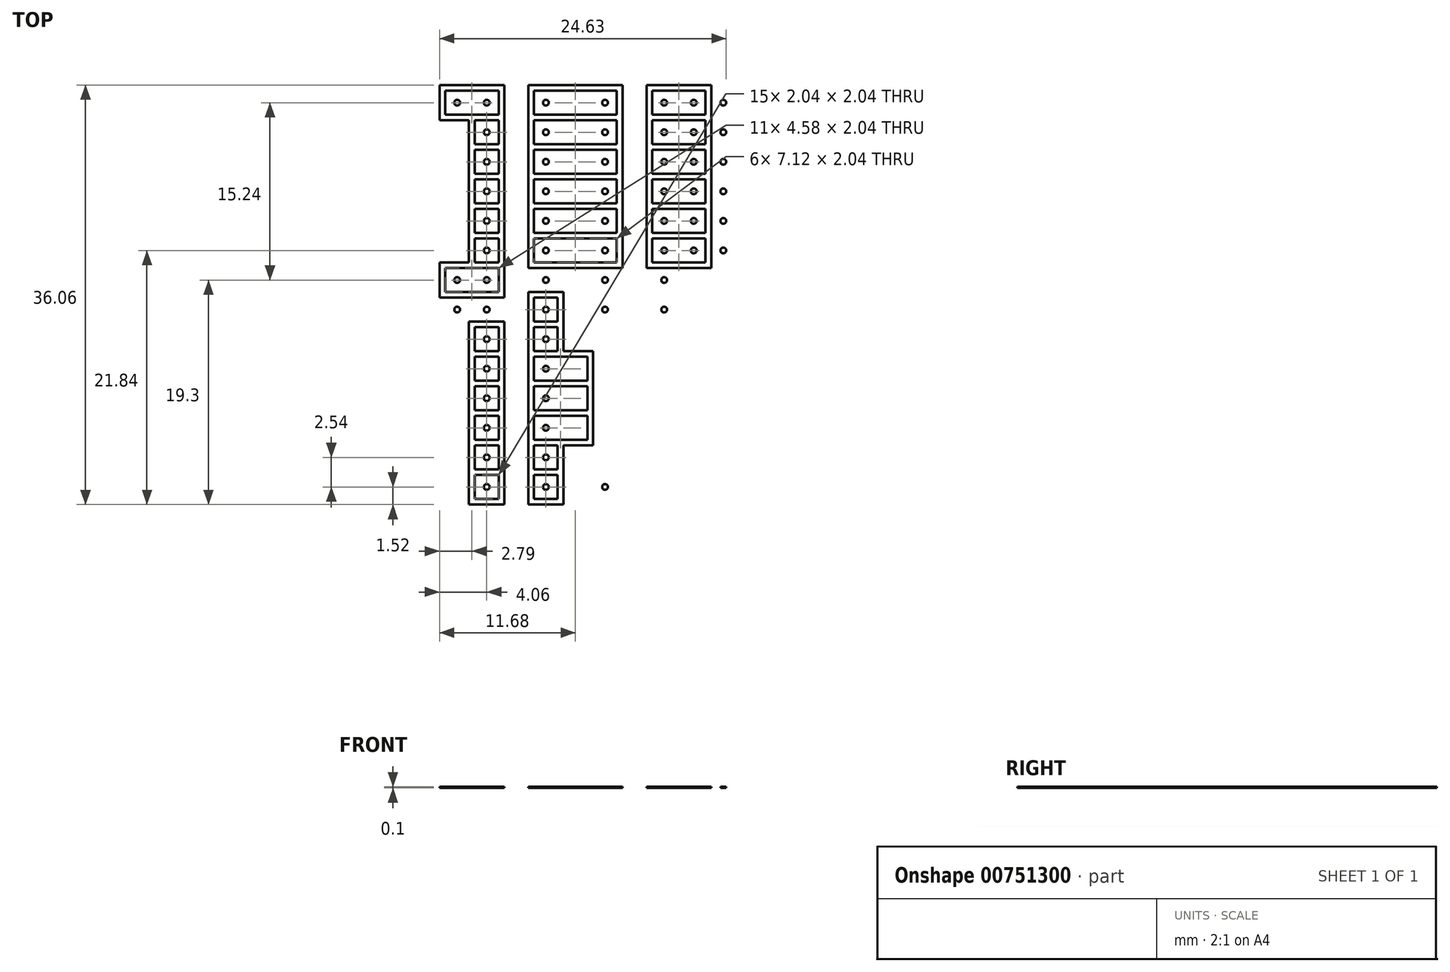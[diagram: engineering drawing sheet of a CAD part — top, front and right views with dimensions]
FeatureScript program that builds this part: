
annotation { "Feature Type Name" : "Feature", "Feature Type Description" : "" }
export const myFeature = defineFeature(function(context is Context, id is Id, definition is map)
    precondition{}
    {
        {
            var Q0;
            Q0=qCreatedBy(makeId("Top.planeOp"),FACE);
            var sketch = newSketch(context, id + "F0", { "sketchPlane" : qUnion([Q0])});
            skLineSegment(sketch, "E0.bottom", {"start": v(0, 0) * mm, "end": v(70, 0) * mm});
            skLineSegment(sketch, "E0.top", {"start": v(0, 100) * mm, "end": v(70, 100) * mm});
            skLineSegment(sketch, "E0.left", {"start": v(0, 0) * mm, "end": v(0, 100) * mm});
            skLineSegment(sketch, "E0.right", {"start": v(70, 0) * mm, "end": v(70, 100) * mm});
            skLineSegment(sketch, "E1", {"start": v(0.46, 100) * mm, "end": v(0.46, 0) * mm});
            skLineSegment(sketch, "E2", {"start": v(0.96, 100) * mm, "end": v(0.96, 0) * mm});
            skLineSegment(sketch, "E3.1.0.0", {"start": v(3, 100) * mm, "end": v(3, 0) * mm});
            skLineSegment(sketch, "E3.1.0.1", {"start": v(3.5, 100) * mm, "end": v(3.5, 0) * mm});
            skLineSegment(sketch, "E3.2.0.0", {"start": v(5.54, 100) * mm, "end": v(5.54, 0) * mm});
            skLineSegment(sketch, "E3.2.0.1", {"start": v(6.04, 100) * mm, "end": v(6.04, 0) * mm});
            skLineSegment(sketch, "E3.3.0.0", {"start": v(8.08, 100) * mm, "end": v(8.08, 0) * mm});
            skLineSegment(sketch, "E3.3.0.1", {"start": v(8.58, 100) * mm, "end": v(8.58, 0) * mm});
            skLineSegment(sketch, "E3.4.0.0", {"start": v(10.62, 100) * mm, "end": v(10.62, 0) * mm});
            skLineSegment(sketch, "E3.4.0.1", {"start": v(11.12, 100) * mm, "end": v(11.12, 0) * mm});
            skLineSegment(sketch, "E3.5.0.0", {"start": v(13.16, 100) * mm, "end": v(13.16, 0) * mm});
            skLineSegment(sketch, "E3.5.0.1", {"start": v(13.66, 100) * mm, "end": v(13.66, 0) * mm});
            skLineSegment(sketch, "E3.6.0.0", {"start": v(15.7, 100) * mm, "end": v(15.7, 0) * mm});
            skLineSegment(sketch, "E3.6.0.1", {"start": v(16.2, 100) * mm, "end": v(16.2, 0) * mm});
            skLineSegment(sketch, "E3.7.0.0", {"start": v(18.24, 100) * mm, "end": v(18.24, 0) * mm});
            skLineSegment(sketch, "E3.7.0.1", {"start": v(18.74, 100) * mm, "end": v(18.74, 0) * mm});
            skLineSegment(sketch, "E3.8.0.0", {"start": v(20.78, 100) * mm, "end": v(20.78, 0) * mm});
            skLineSegment(sketch, "E3.8.0.1", {"start": v(21.28, 100) * mm, "end": v(21.28, 0) * mm});
            skLineSegment(sketch, "E3.9.0.0", {"start": v(23.32, 100) * mm, "end": v(23.32, 0) * mm});
            skLineSegment(sketch, "E3.9.0.1", {"start": v(23.82, 100) * mm, "end": v(23.82, 0) * mm});
            skLineSegment(sketch, "E3.10.0.0", {"start": v(25.86, 100) * mm, "end": v(25.86, 0) * mm});
            skLineSegment(sketch, "E3.10.0.1", {"start": v(26.36, 100) * mm, "end": v(26.36, 0) * mm});
            skLineSegment(sketch, "E3.11.0.0", {"start": v(28.4, 100) * mm, "end": v(28.4, 0) * mm});
            skLineSegment(sketch, "E3.11.0.1", {"start": v(28.9, 100) * mm, "end": v(28.9, 0) * mm});
            skLineSegment(sketch, "E3.12.0.0", {"start": v(30.94, 100) * mm, "end": v(30.94, 0) * mm});
            skLineSegment(sketch, "E3.12.0.1", {"start": v(31.44, 100) * mm, "end": v(31.44, 0) * mm});
            skLineSegment(sketch, "E3.13.0.0", {"start": v(33.48, 100) * mm, "end": v(33.48, 0) * mm});
            skLineSegment(sketch, "E3.13.0.1", {"start": v(33.98, 100) * mm, "end": v(33.98, 0) * mm});
            skLineSegment(sketch, "E3.14.0.0", {"start": v(36.02, 100) * mm, "end": v(36.02, 0) * mm});
            skLineSegment(sketch, "E3.14.0.1", {"start": v(36.52, 100) * mm, "end": v(36.52, 0) * mm});
            skLineSegment(sketch, "E3.15.0.0", {"start": v(38.56, 100) * mm, "end": v(38.56, 0) * mm});
            skLineSegment(sketch, "E3.15.0.1", {"start": v(39.06, 100) * mm, "end": v(39.06, 0) * mm});
            skLineSegment(sketch, "E3.16.0.0", {"start": v(41.1, 100) * mm, "end": v(41.1, 0) * mm});
            skLineSegment(sketch, "E3.16.0.1", {"start": v(41.6, 100) * mm, "end": v(41.6, 0) * mm});
            skLineSegment(sketch, "E3.17.0.0", {"start": v(43.64, 100) * mm, "end": v(43.64, 0) * mm});
            skLineSegment(sketch, "E3.17.0.1", {"start": v(44.14, 100) * mm, "end": v(44.14, 0) * mm});
            skLineSegment(sketch, "E3.18.0.0", {"start": v(46.18, 100) * mm, "end": v(46.18, 0) * mm});
            skLineSegment(sketch, "E3.18.0.1", {"start": v(46.68, 100) * mm, "end": v(46.68, 0) * mm});
            skLineSegment(sketch, "E3.19.0.0", {"start": v(48.72, 100) * mm, "end": v(48.72, 0) * mm});
            skLineSegment(sketch, "E3.19.0.1", {"start": v(49.22, 100) * mm, "end": v(49.22, 0) * mm});
            skLineSegment(sketch, "E3.20.0.0", {"start": v(51.26, 100) * mm, "end": v(51.26, 0) * mm});
            skLineSegment(sketch, "E3.20.0.1", {"start": v(51.76, 100) * mm, "end": v(51.76, 0) * mm});
            skLineSegment(sketch, "E3.21.0.0", {"start": v(53.8, 100) * mm, "end": v(53.8, 0) * mm});
            skLineSegment(sketch, "E3.21.0.1", {"start": v(54.3, 100) * mm, "end": v(54.3, 0) * mm});
            skLineSegment(sketch, "E3.22.0.0", {"start": v(56.34, 100) * mm, "end": v(56.34, 0) * mm});
            skLineSegment(sketch, "E3.22.0.1", {"start": v(56.84, 100) * mm, "end": v(56.84, 0) * mm});
            skLineSegment(sketch, "E3.23.0.0", {"start": v(58.88, 100) * mm, "end": v(58.88, 0) * mm});
            skLineSegment(sketch, "E3.23.0.1", {"start": v(59.38, 100) * mm, "end": v(59.38, 0) * mm});
            skLineSegment(sketch, "E3.24.0.0", {"start": v(61.42, 100) * mm, "end": v(61.42, 0) * mm});
            skLineSegment(sketch, "E3.24.0.1", {"start": v(61.92, 100) * mm, "end": v(61.92, 0) * mm});
            skLineSegment(sketch, "E3.25.0.0", {"start": v(63.96, 100) * mm, "end": v(63.96, 0) * mm});
            skLineSegment(sketch, "E3.25.0.1", {"start": v(64.46, 100) * mm, "end": v(64.46, 0) * mm});
            skLineSegment(sketch, "E3.26.0.0", {"start": v(66.5, 100) * mm, "end": v(66.5, 0) * mm});
            skLineSegment(sketch, "E3.26.0.1", {"start": v(67, 100) * mm, "end": v(67, 0) * mm});
            skLineSegment(sketch, "E3.27.0.0", {"start": v(69.04, 100) * mm, "end": v(69.04, 0) * mm});
            skLineSegment(sketch, "E3.27.0.1", {"start": v(69.54, 100) * mm, "end": v(69.54, 0) * mm});
            skLineSegment(sketch, "E3.direction1", {"start": v(0.46, 0) * mm, "end": v(3, 0) * mm, "construction": true});
            skLineSegment(sketch, "E4", {"start": v(0, 50) * mm, "end": v(0.46, 50) * mm, "construction": true});
            skLineSegment(sketch, "E5", {"start": v(69.54, 50) * mm, "end": v(70, 50) * mm, "construction": true});
            skLineSegment(sketch, "E6", {"start": v(0, 99.28) * mm, "end": v(70, 99.28) * mm});
            skLineSegment(sketch, "E7", {"start": v(70, 99.28) * mm, "end": v(70, 99.78) * mm});
            skLineSegment(sketch, "E8", {"start": v(70, 99.78) * mm, "end": v(0, 99.78) * mm});
            skLineSegment(sketch, "E9.1.0.0", {"start": v(70, 97.24) * mm, "end": v(0, 97.24) * mm});
            skLineSegment(sketch, "E9.1.0.1", {"start": v(0, 96.74) * mm, "end": v(70, 96.74) * mm});
            skLineSegment(sketch, "E9.2.0.0", {"start": v(70, 94.7) * mm, "end": v(0, 94.7) * mm});
            skLineSegment(sketch, "E9.2.0.1", {"start": v(0, 94.2) * mm, "end": v(70, 94.2) * mm});
            skLineSegment(sketch, "E9.direction1", {"start": v(0, 99.28) * mm, "end": v(0, 96.74) * mm, "construction": true});
            skLineSegment(sketch, "E10.0.3.0", {"start": v(70, 92.16) * mm, "end": v(0, 92.16) * mm});
            skLineSegment(sketch, "E10.3.3.0", {"start": v(0, 91.66) * mm, "end": v(70, 91.66) * mm});
            skLineSegment(sketch, "E10.0.4.0", {"start": v(70, 89.62) * mm, "end": v(0, 89.62) * mm});
            skLineSegment(sketch, "E10.3.4.0", {"start": v(0, 89.12) * mm, "end": v(70, 89.12) * mm});
            skLineSegment(sketch, "E10.0.5.0", {"start": v(70, 87.08) * mm, "end": v(0, 87.08) * mm});
            skLineSegment(sketch, "E10.3.5.0", {"start": v(0, 86.58) * mm, "end": v(70, 86.58) * mm});
            skLineSegment(sketch, "E10.0.6.0", {"start": v(70, 84.54) * mm, "end": v(0, 84.54) * mm});
            skLineSegment(sketch, "E10.3.6.0", {"start": v(0, 84.04) * mm, "end": v(70, 84.04) * mm});
            skLineSegment(sketch, "E10.0.7.0", {"start": v(70, 82) * mm, "end": v(0, 82) * mm});
            skLineSegment(sketch, "E10.3.7.0", {"start": v(0, 81.5) * mm, "end": v(70, 81.5) * mm});
            skLineSegment(sketch, "E10.0.8.0", {"start": v(70, 79.46) * mm, "end": v(0, 79.46) * mm});
            skLineSegment(sketch, "E10.3.8.0", {"start": v(0, 78.96) * mm, "end": v(70, 78.96) * mm});
            skLineSegment(sketch, "E10.0.9.0", {"start": v(70, 76.92) * mm, "end": v(0, 76.92) * mm});
            skLineSegment(sketch, "E10.3.9.0", {"start": v(0, 76.42) * mm, "end": v(70, 76.42) * mm});
            skLineSegment(sketch, "E10.0.10.0", {"start": v(70, 74.38) * mm, "end": v(0, 74.38) * mm});
            skLineSegment(sketch, "E10.3.10.0", {"start": v(0, 73.88) * mm, "end": v(70, 73.88) * mm});
            skLineSegment(sketch, "E10.0.11.0", {"start": v(70, 71.84) * mm, "end": v(0, 71.84) * mm});
            skLineSegment(sketch, "E10.3.11.0", {"start": v(0, 71.34) * mm, "end": v(70, 71.34) * mm});
            skLineSegment(sketch, "E10.0.12.0", {"start": v(70, 69.3) * mm, "end": v(0, 69.3) * mm});
            skLineSegment(sketch, "E10.3.12.0", {"start": v(0, 68.8) * mm, "end": v(70, 68.8) * mm});
            skLineSegment(sketch, "E10.0.13.0", {"start": v(70, 66.76) * mm, "end": v(0, 66.76) * mm});
            skLineSegment(sketch, "E10.3.13.0", {"start": v(0, 66.26) * mm, "end": v(70, 66.26) * mm});
            skLineSegment(sketch, "E10.0.14.0", {"start": v(70, 64.22) * mm, "end": v(0, 64.22) * mm});
            skLineSegment(sketch, "E10.3.14.0", {"start": v(0, 63.72) * mm, "end": v(70, 63.72) * mm});
            skLineSegment(sketch, "E10.0.15.0", {"start": v(70, 61.68) * mm, "end": v(0, 61.68) * mm});
            skLineSegment(sketch, "E10.3.15.0", {"start": v(0, 61.18) * mm, "end": v(70, 61.18) * mm});
            skLineSegment(sketch, "E10.0.16.0", {"start": v(70, 59.14) * mm, "end": v(0, 59.14) * mm});
            skLineSegment(sketch, "E10.3.16.0", {"start": v(0, 58.64) * mm, "end": v(70, 58.64) * mm});
            skLineSegment(sketch, "E10.0.17.0", {"start": v(70, 56.6) * mm, "end": v(0, 56.6) * mm});
            skLineSegment(sketch, "E10.3.17.0", {"start": v(0, 56.1) * mm, "end": v(70, 56.1) * mm});
            skLineSegment(sketch, "E10.0.18.0", {"start": v(70, 54.06) * mm, "end": v(0, 54.06) * mm});
            skLineSegment(sketch, "E10.3.18.0", {"start": v(0, 53.56) * mm, "end": v(70, 53.56) * mm});
            skLineSegment(sketch, "E10.0.19.0", {"start": v(70, 51.52) * mm, "end": v(0, 51.52) * mm});
            skLineSegment(sketch, "E10.3.19.0", {"start": v(0, 51.02) * mm, "end": v(70, 51.02) * mm});
            skLineSegment(sketch, "E10.0.20.0", {"start": v(70, 48.98) * mm, "end": v(0, 48.98) * mm});
            skLineSegment(sketch, "E10.3.20.0", {"start": v(0, 48.48) * mm, "end": v(70, 48.48) * mm});
            skLineSegment(sketch, "E10.0.21.0", {"start": v(70, 46.44) * mm, "end": v(0, 46.44) * mm});
            skLineSegment(sketch, "E10.3.21.0", {"start": v(0, 45.94) * mm, "end": v(70, 45.94) * mm});
            skLineSegment(sketch, "E10.0.22.0", {"start": v(70, 43.9) * mm, "end": v(0, 43.9) * mm});
            skLineSegment(sketch, "E10.3.22.0", {"start": v(0, 43.4) * mm, "end": v(70, 43.4) * mm});
            skLineSegment(sketch, "E10.0.23.0", {"start": v(70, 41.36) * mm, "end": v(0, 41.36) * mm});
            skLineSegment(sketch, "E10.3.23.0", {"start": v(0, 40.86) * mm, "end": v(70, 40.86) * mm});
            skLineSegment(sketch, "E10.0.24.0", {"start": v(70, 38.82) * mm, "end": v(0, 38.82) * mm});
            skLineSegment(sketch, "E10.3.24.0", {"start": v(0, 38.32) * mm, "end": v(70, 38.32) * mm});
            skLineSegment(sketch, "E10.0.25.0", {"start": v(70, 36.28) * mm, "end": v(0, 36.28) * mm});
            skLineSegment(sketch, "E10.3.25.0", {"start": v(0, 35.78) * mm, "end": v(70, 35.78) * mm});
            skLineSegment(sketch, "E10.0.26.0", {"start": v(70, 33.74) * mm, "end": v(0, 33.74) * mm});
            skLineSegment(sketch, "E10.3.26.0", {"start": v(0, 33.24) * mm, "end": v(70, 33.24) * mm});
            skLineSegment(sketch, "E10.0.27.0", {"start": v(70, 31.2) * mm, "end": v(0, 31.2) * mm});
            skLineSegment(sketch, "E10.3.27.0", {"start": v(0, 30.7) * mm, "end": v(70, 30.7) * mm});
            skLineSegment(sketch, "E10.0.28.0", {"start": v(70, 28.66) * mm, "end": v(0, 28.66) * mm});
            skLineSegment(sketch, "E10.3.28.0", {"start": v(0, 28.16) * mm, "end": v(70, 28.16) * mm});
            skLineSegment(sketch, "E10.0.29.0", {"start": v(70, 26.12) * mm, "end": v(0, 26.12) * mm});
            skLineSegment(sketch, "E10.3.29.0", {"start": v(0, 25.62) * mm, "end": v(70, 25.62) * mm});
            skLineSegment(sketch, "E10.0.30.0", {"start": v(70, 23.58) * mm, "end": v(0, 23.58) * mm});
            skLineSegment(sketch, "E10.3.30.0", {"start": v(0, 23.08) * mm, "end": v(70, 23.08) * mm});
            skLineSegment(sketch, "E10.0.31.0", {"start": v(70, 21.04) * mm, "end": v(0, 21.04) * mm});
            skLineSegment(sketch, "E10.3.31.0", {"start": v(0, 20.54) * mm, "end": v(70, 20.54) * mm});
            skLineSegment(sketch, "E10.0.32.0", {"start": v(70, 18.5) * mm, "end": v(0, 18.5) * mm});
            skLineSegment(sketch, "E10.3.32.0", {"start": v(0, 18) * mm, "end": v(70, 18) * mm});
            skLineSegment(sketch, "E10.0.33.0", {"start": v(70, 15.96) * mm, "end": v(0, 15.96) * mm});
            skLineSegment(sketch, "E10.3.33.0", {"start": v(0, 15.46) * mm, "end": v(70, 15.46) * mm});
            skLineSegment(sketch, "E10.0.34.0", {"start": v(70, 13.42) * mm, "end": v(0, 13.42) * mm});
            skLineSegment(sketch, "E10.3.34.0", {"start": v(0, 12.92) * mm, "end": v(70, 12.92) * mm});
            skLineSegment(sketch, "E10.0.35.0", {"start": v(70, 10.88) * mm, "end": v(0, 10.88) * mm});
            skLineSegment(sketch, "E10.3.35.0", {"start": v(0, 10.38) * mm, "end": v(70, 10.38) * mm});
            skLineSegment(sketch, "E10.0.36.0", {"start": v(70, 8.34) * mm, "end": v(0, 8.34) * mm});
            skLineSegment(sketch, "E10.3.36.0", {"start": v(0, 7.84) * mm, "end": v(70, 7.84) * mm});
            skLineSegment(sketch, "E10.0.37.0", {"start": v(70, 5.8) * mm, "end": v(0, 5.8) * mm});
            skLineSegment(sketch, "E10.3.37.0", {"start": v(0, 5.3) * mm, "end": v(70, 5.3) * mm});
            skLineSegment(sketch, "E10.0.38.0", {"start": v(70, 3.26) * mm, "end": v(0, 3.26) * mm});
            skLineSegment(sketch, "E10.3.38.0", {"start": v(0, 2.76) * mm, "end": v(70, 2.76) * mm});
            skLineSegment(sketch, "E10.0.39.0", {"start": v(70, 0.72) * mm, "end": v(0, 0.72) * mm});
            skLineSegment(sketch, "E10.3.39.0", {"start": v(0, 0.22) * mm, "end": v(70, 0.22) * mm});
            skLineSegment(sketch, "E11", {"start": v(35, 100) * mm, "end": v(35, 99.78) * mm, "construction": true});
            skLineSegment(sketch, "E12", {"start": v(35, 0) * mm, "end": v(35, 0.22) * mm, "construction": true});
            skCircle(sketch, "E13", {"center": v(1.98, 1.74) * mm, "radius": 0.25 * mm});
            skLineSegment(sketch, "E14", {"start": v(1.98, 2.76) * mm, "end": v(1.98, 0.72) * mm, "construction": true});
            skLineSegment(sketch, "E15", {"start": v(3, 1.74) * mm, "end": v(0.96, 1.74) * mm, "construction": true});
            skCircle(sketch, "E16.1.0.0", {"center": v(4.52, 1.74) * mm, "radius": 0.25 * mm});
            skCircle(sketch, "E16.2.0.0", {"center": v(7.06, 1.74) * mm, "radius": 0.25 * mm});
            skCircle(sketch, "E16.3.0.0", {"center": v(9.6, 1.74) * mm, "radius": 0.25 * mm});
            skCircle(sketch, "E16.4.0.0", {"center": v(12.14, 1.74) * mm, "radius": 0.25 * mm});
            skCircle(sketch, "E16.5.0.0", {"center": v(14.68, 1.74) * mm, "radius": 0.25 * mm});
            skCircle(sketch, "E16.6.0.0", {"center": v(17.22, 1.74) * mm, "radius": 0.25 * mm});
            skCircle(sketch, "E16.7.0.0", {"center": v(19.76, 1.74) * mm, "radius": 0.25 * mm});
            skCircle(sketch, "E16.8.0.0", {"center": v(22.3, 1.74) * mm, "radius": 0.25 * mm});
            skCircle(sketch, "E16.9.0.0", {"center": v(24.84, 1.74) * mm, "radius": 0.25 * mm});
            skCircle(sketch, "E16.10.0.0", {"center": v(27.38, 1.74) * mm, "radius": 0.25 * mm});
            skCircle(sketch, "E16.11.0.0", {"center": v(29.92, 1.74) * mm, "radius": 0.25 * mm});
            skCircle(sketch, "E16.12.0.0", {"center": v(32.46, 1.74) * mm, "radius": 0.25 * mm});
            skCircle(sketch, "E16.13.0.0", {"center": v(35, 1.74) * mm, "radius": 0.25 * mm});
            skCircle(sketch, "E16.14.0.0", {"center": v(37.54, 1.74) * mm, "radius": 0.25 * mm});
            skCircle(sketch, "E16.15.0.0", {"center": v(40.08, 1.74) * mm, "radius": 0.25 * mm});
            skCircle(sketch, "E16.16.0.0", {"center": v(42.62, 1.74) * mm, "radius": 0.25 * mm});
            skCircle(sketch, "E16.17.0.0", {"center": v(45.16, 1.74) * mm, "radius": 0.25 * mm});
            skCircle(sketch, "E16.18.0.0", {"center": v(47.7, 1.74) * mm, "radius": 0.25 * mm});
            skCircle(sketch, "E16.19.0.0", {"center": v(50.24, 1.74) * mm, "radius": 0.25 * mm});
            skCircle(sketch, "E16.20.0.0", {"center": v(52.78, 1.74) * mm, "radius": 0.25 * mm});
            skCircle(sketch, "E16.21.0.0", {"center": v(55.32, 1.74) * mm, "radius": 0.25 * mm});
            skCircle(sketch, "E16.22.0.0", {"center": v(57.86, 1.74) * mm, "radius": 0.25 * mm});
            skCircle(sketch, "E16.23.0.0", {"center": v(60.4, 1.74) * mm, "radius": 0.25 * mm});
            skCircle(sketch, "E16.24.0.0", {"center": v(62.94, 1.74) * mm, "radius": 0.25 * mm});
            skCircle(sketch, "E16.25.0.0", {"center": v(65.48, 1.74) * mm, "radius": 0.25 * mm});
            skCircle(sketch, "E16.26.0.0", {"center": v(68.02, 1.74) * mm, "radius": 0.25 * mm});
            skLineSegment(sketch, "E16.direction1", {"start": v(1.98, 1.74) * mm, "end": v(4.52, 1.74) * mm, "construction": true});
            skCircle(sketch, "E17.1.0.0", {"center": v(1.98, 4.28) * mm, "radius": 0.25 * mm});
            skCircle(sketch, "E17.1.0.1", {"center": v(4.52, 4.28) * mm, "radius": 0.25 * mm});
            skCircle(sketch, "E17.1.0.2", {"center": v(7.06, 4.28) * mm, "radius": 0.25 * mm});
            skCircle(sketch, "E17.1.0.3", {"center": v(9.6, 4.28) * mm, "radius": 0.25 * mm});
            skCircle(sketch, "E17.1.0.4", {"center": v(12.14, 4.28) * mm, "radius": 0.25 * mm});
            skCircle(sketch, "E17.1.0.5", {"center": v(14.68, 4.28) * mm, "radius": 0.25 * mm});
            skCircle(sketch, "E17.1.0.6", {"center": v(17.22, 4.28) * mm, "radius": 0.25 * mm});
            skCircle(sketch, "E17.1.0.7", {"center": v(19.76, 4.28) * mm, "radius": 0.25 * mm});
            skCircle(sketch, "E17.1.0.8", {"center": v(22.3, 4.28) * mm, "radius": 0.25 * mm});
            skCircle(sketch, "E17.1.0.9", {"center": v(24.84, 4.28) * mm, "radius": 0.25 * mm});
            skCircle(sketch, "E17.1.0.10", {"center": v(27.38, 4.28) * mm, "radius": 0.25 * mm});
            skCircle(sketch, "E17.1.0.11", {"center": v(29.92, 4.28) * mm, "radius": 0.25 * mm});
            skCircle(sketch, "E17.1.0.12", {"center": v(32.46, 4.28) * mm, "radius": 0.25 * mm});
            skCircle(sketch, "E17.1.0.13", {"center": v(35, 4.28) * mm, "radius": 0.25 * mm});
            skCircle(sketch, "E17.1.0.14", {"center": v(37.54, 4.28) * mm, "radius": 0.25 * mm});
            skCircle(sketch, "E17.1.0.15", {"center": v(40.08, 4.28) * mm, "radius": 0.25 * mm});
            skCircle(sketch, "E17.1.0.16", {"center": v(42.62, 4.28) * mm, "radius": 0.25 * mm});
            skCircle(sketch, "E17.1.0.17", {"center": v(45.16, 4.28) * mm, "radius": 0.25 * mm});
            skCircle(sketch, "E17.1.0.18", {"center": v(47.7, 4.28) * mm, "radius": 0.25 * mm});
            skCircle(sketch, "E17.1.0.19", {"center": v(50.24, 4.28) * mm, "radius": 0.25 * mm});
            skCircle(sketch, "E17.1.0.20", {"center": v(52.78, 4.28) * mm, "radius": 0.25 * mm});
            skCircle(sketch, "E17.1.0.21", {"center": v(55.32, 4.28) * mm, "radius": 0.25 * mm});
            skCircle(sketch, "E17.1.0.22", {"center": v(57.86, 4.28) * mm, "radius": 0.25 * mm});
            skCircle(sketch, "E17.1.0.23", {"center": v(60.4, 4.28) * mm, "radius": 0.25 * mm});
            skCircle(sketch, "E17.1.0.24", {"center": v(62.94, 4.28) * mm, "radius": 0.25 * mm});
            skCircle(sketch, "E17.1.0.25", {"center": v(65.48, 4.28) * mm, "radius": 0.25 * mm});
            skCircle(sketch, "E17.1.0.26", {"center": v(68.02, 4.28) * mm, "radius": 0.25 * mm});
            skCircle(sketch, "E17.2.0.0", {"center": v(1.98, 6.82) * mm, "radius": 0.25 * mm});
            skCircle(sketch, "E17.2.0.1", {"center": v(4.52, 6.82) * mm, "radius": 0.25 * mm});
            skCircle(sketch, "E17.2.0.2", {"center": v(7.06, 6.82) * mm, "radius": 0.25 * mm});
            skCircle(sketch, "E17.2.0.3", {"center": v(9.6, 6.82) * mm, "radius": 0.25 * mm});
            skCircle(sketch, "E17.2.0.4", {"center": v(12.14, 6.82) * mm, "radius": 0.25 * mm});
            skCircle(sketch, "E17.2.0.5", {"center": v(14.68, 6.82) * mm, "radius": 0.25 * mm});
            skCircle(sketch, "E17.2.0.6", {"center": v(17.22, 6.82) * mm, "radius": 0.25 * mm});
            skCircle(sketch, "E17.2.0.7", {"center": v(19.76, 6.82) * mm, "radius": 0.25 * mm});
            skCircle(sketch, "E17.2.0.8", {"center": v(22.3, 6.82) * mm, "radius": 0.25 * mm});
            skCircle(sketch, "E17.2.0.9", {"center": v(24.84, 6.82) * mm, "radius": 0.25 * mm});
            skCircle(sketch, "E17.2.0.10", {"center": v(27.38, 6.82) * mm, "radius": 0.25 * mm});
            skCircle(sketch, "E17.2.0.11", {"center": v(29.92, 6.82) * mm, "radius": 0.25 * mm});
            skCircle(sketch, "E17.2.0.12", {"center": v(32.46, 6.82) * mm, "radius": 0.25 * mm});
            skCircle(sketch, "E17.2.0.13", {"center": v(35, 6.82) * mm, "radius": 0.25 * mm});
            skCircle(sketch, "E17.2.0.14", {"center": v(37.54, 6.82) * mm, "radius": 0.25 * mm});
            skCircle(sketch, "E17.2.0.15", {"center": v(40.08, 6.82) * mm, "radius": 0.25 * mm});
            skCircle(sketch, "E17.2.0.16", {"center": v(42.62, 6.82) * mm, "radius": 0.25 * mm});
            skCircle(sketch, "E17.2.0.17", {"center": v(45.16, 6.82) * mm, "radius": 0.25 * mm});
            skCircle(sketch, "E17.2.0.18", {"center": v(47.7, 6.82) * mm, "radius": 0.25 * mm});
            skCircle(sketch, "E17.2.0.19", {"center": v(50.24, 6.82) * mm, "radius": 0.25 * mm});
            skCircle(sketch, "E17.2.0.20", {"center": v(52.78, 6.82) * mm, "radius": 0.25 * mm});
            skCircle(sketch, "E17.2.0.21", {"center": v(55.32, 6.82) * mm, "radius": 0.25 * mm});
            skCircle(sketch, "E17.2.0.22", {"center": v(57.86, 6.82) * mm, "radius": 0.25 * mm});
            skCircle(sketch, "E17.2.0.23", {"center": v(60.4, 6.82) * mm, "radius": 0.25 * mm});
            skCircle(sketch, "E17.2.0.24", {"center": v(62.94, 6.82) * mm, "radius": 0.25 * mm});
            skCircle(sketch, "E17.2.0.25", {"center": v(65.48, 6.82) * mm, "radius": 0.25 * mm});
            skCircle(sketch, "E17.2.0.26", {"center": v(68.02, 6.82) * mm, "radius": 0.25 * mm});
            skLineSegment(sketch, "E17.direction1", {"start": v(1.98, 1.74) * mm, "end": v(1.98, 4.28) * mm, "construction": true});
            skCircle(sketch, "E18.0.3.0", {"center": v(1.98, 9.36) * mm, "radius": 0.25 * mm});
            skCircle(sketch, "E18.2.3.0", {"center": v(4.52, 9.36) * mm, "radius": 0.25 * mm});
            skCircle(sketch, "E18.4.3.0", {"center": v(7.06, 9.36) * mm, "radius": 0.25 * mm});
            skCircle(sketch, "E18.6.3.0", {"center": v(9.6, 9.36) * mm, "radius": 0.25 * mm});
            skCircle(sketch, "E18.8.3.0", {"center": v(12.14, 9.36) * mm, "radius": 0.25 * mm});
            skCircle(sketch, "E18.10.3.0", {"center": v(14.68, 9.36) * mm, "radius": 0.25 * mm});
            skCircle(sketch, "E18.12.3.0", {"center": v(17.22, 9.36) * mm, "radius": 0.25 * mm});
            skCircle(sketch, "E18.14.3.0", {"center": v(19.76, 9.36) * mm, "radius": 0.25 * mm});
            skCircle(sketch, "E18.16.3.0", {"center": v(22.3, 9.36) * mm, "radius": 0.25 * mm});
            skCircle(sketch, "E18.18.3.0", {"center": v(24.84, 9.36) * mm, "radius": 0.25 * mm});
            skCircle(sketch, "E18.20.3.0", {"center": v(27.38, 9.36) * mm, "radius": 0.25 * mm});
            skCircle(sketch, "E18.22.3.0", {"center": v(29.92, 9.36) * mm, "radius": 0.25 * mm});
            skCircle(sketch, "E18.24.3.0", {"center": v(32.46, 9.36) * mm, "radius": 0.25 * mm});
            skCircle(sketch, "E18.26.3.0", {"center": v(35, 9.36) * mm, "radius": 0.25 * mm});
            skCircle(sketch, "E18.28.3.0", {"center": v(37.54, 9.36) * mm, "radius": 0.25 * mm});
            skCircle(sketch, "E18.30.3.0", {"center": v(40.08, 9.36) * mm, "radius": 0.25 * mm});
            skCircle(sketch, "E18.32.3.0", {"center": v(42.62, 9.36) * mm, "radius": 0.25 * mm});
            skCircle(sketch, "E18.34.3.0", {"center": v(45.16, 9.36) * mm, "radius": 0.25 * mm});
            skCircle(sketch, "E18.36.3.0", {"center": v(47.7, 9.36) * mm, "radius": 0.25 * mm});
            skCircle(sketch, "E18.38.3.0", {"center": v(50.24, 9.36) * mm, "radius": 0.25 * mm});
            skCircle(sketch, "E18.40.3.0", {"center": v(52.78, 9.36) * mm, "radius": 0.25 * mm});
            skCircle(sketch, "E18.42.3.0", {"center": v(55.32, 9.36) * mm, "radius": 0.25 * mm});
            skCircle(sketch, "E18.44.3.0", {"center": v(57.86, 9.36) * mm, "radius": 0.25 * mm});
            skCircle(sketch, "E18.46.3.0", {"center": v(60.4, 9.36) * mm, "radius": 0.25 * mm});
            skCircle(sketch, "E18.48.3.0", {"center": v(62.94, 9.36) * mm, "radius": 0.25 * mm});
            skCircle(sketch, "E18.50.3.0", {"center": v(65.48, 9.36) * mm, "radius": 0.25 * mm});
            skCircle(sketch, "E18.52.3.0", {"center": v(68.02, 9.36) * mm, "radius": 0.25 * mm});
            skCircle(sketch, "E18.0.4.0", {"center": v(1.98, 11.9) * mm, "radius": 0.25 * mm});
            skCircle(sketch, "E18.2.4.0", {"center": v(4.52, 11.9) * mm, "radius": 0.25 * mm});
            skCircle(sketch, "E18.4.4.0", {"center": v(7.06, 11.9) * mm, "radius": 0.25 * mm});
            skCircle(sketch, "E18.6.4.0", {"center": v(9.6, 11.9) * mm, "radius": 0.25 * mm});
            skCircle(sketch, "E18.8.4.0", {"center": v(12.14, 11.9) * mm, "radius": 0.25 * mm});
            skCircle(sketch, "E18.10.4.0", {"center": v(14.68, 11.9) * mm, "radius": 0.25 * mm});
            skCircle(sketch, "E18.12.4.0", {"center": v(17.22, 11.9) * mm, "radius": 0.25 * mm});
            skCircle(sketch, "E18.14.4.0", {"center": v(19.76, 11.9) * mm, "radius": 0.25 * mm});
            skCircle(sketch, "E18.16.4.0", {"center": v(22.3, 11.9) * mm, "radius": 0.25 * mm});
            skCircle(sketch, "E18.18.4.0", {"center": v(24.84, 11.9) * mm, "radius": 0.25 * mm});
            skCircle(sketch, "E18.20.4.0", {"center": v(27.38, 11.9) * mm, "radius": 0.25 * mm});
            skCircle(sketch, "E18.22.4.0", {"center": v(29.92, 11.9) * mm, "radius": 0.25 * mm});
            skCircle(sketch, "E18.24.4.0", {"center": v(32.46, 11.9) * mm, "radius": 0.25 * mm});
            skCircle(sketch, "E18.26.4.0", {"center": v(35, 11.9) * mm, "radius": 0.25 * mm});
            skCircle(sketch, "E18.28.4.0", {"center": v(37.54, 11.9) * mm, "radius": 0.25 * mm});
            skCircle(sketch, "E18.30.4.0", {"center": v(40.08, 11.9) * mm, "radius": 0.25 * mm});
            skCircle(sketch, "E18.32.4.0", {"center": v(42.62, 11.9) * mm, "radius": 0.25 * mm});
            skCircle(sketch, "E18.34.4.0", {"center": v(45.16, 11.9) * mm, "radius": 0.25 * mm});
            skCircle(sketch, "E18.36.4.0", {"center": v(47.7, 11.9) * mm, "radius": 0.25 * mm});
            skCircle(sketch, "E18.38.4.0", {"center": v(50.24, 11.9) * mm, "radius": 0.25 * mm});
            skCircle(sketch, "E18.40.4.0", {"center": v(52.78, 11.9) * mm, "radius": 0.25 * mm});
            skCircle(sketch, "E18.42.4.0", {"center": v(55.32, 11.9) * mm, "radius": 0.25 * mm});
            skCircle(sketch, "E18.44.4.0", {"center": v(57.86, 11.9) * mm, "radius": 0.25 * mm});
            skCircle(sketch, "E18.46.4.0", {"center": v(60.4, 11.9) * mm, "radius": 0.25 * mm});
            skCircle(sketch, "E18.48.4.0", {"center": v(62.94, 11.9) * mm, "radius": 0.25 * mm});
            skCircle(sketch, "E18.50.4.0", {"center": v(65.48, 11.9) * mm, "radius": 0.25 * mm});
            skCircle(sketch, "E18.52.4.0", {"center": v(68.02, 11.9) * mm, "radius": 0.25 * mm});
            skCircle(sketch, "E18.0.5.0", {"center": v(1.98, 14.44) * mm, "radius": 0.25 * mm});
            skCircle(sketch, "E18.2.5.0", {"center": v(4.52, 14.44) * mm, "radius": 0.25 * mm});
            skCircle(sketch, "E18.4.5.0", {"center": v(7.06, 14.44) * mm, "radius": 0.25 * mm});
            skCircle(sketch, "E18.6.5.0", {"center": v(9.6, 14.44) * mm, "radius": 0.25 * mm});
            skCircle(sketch, "E18.8.5.0", {"center": v(12.14, 14.44) * mm, "radius": 0.25 * mm});
            skCircle(sketch, "E18.10.5.0", {"center": v(14.68, 14.44) * mm, "radius": 0.25 * mm});
            skCircle(sketch, "E18.12.5.0", {"center": v(17.22, 14.44) * mm, "radius": 0.25 * mm});
            skCircle(sketch, "E18.14.5.0", {"center": v(19.76, 14.44) * mm, "radius": 0.25 * mm});
            skCircle(sketch, "E18.16.5.0", {"center": v(22.3, 14.44) * mm, "radius": 0.25 * mm});
            skCircle(sketch, "E18.18.5.0", {"center": v(24.84, 14.44) * mm, "radius": 0.25 * mm});
            skCircle(sketch, "E18.20.5.0", {"center": v(27.38, 14.44) * mm, "radius": 0.25 * mm});
            skCircle(sketch, "E18.22.5.0", {"center": v(29.92, 14.44) * mm, "radius": 0.25 * mm});
            skCircle(sketch, "E18.24.5.0", {"center": v(32.46, 14.44) * mm, "radius": 0.25 * mm});
            skCircle(sketch, "E18.26.5.0", {"center": v(35, 14.44) * mm, "radius": 0.25 * mm});
            skCircle(sketch, "E18.28.5.0", {"center": v(37.54, 14.44) * mm, "radius": 0.25 * mm});
            skCircle(sketch, "E18.30.5.0", {"center": v(40.08, 14.44) * mm, "radius": 0.25 * mm});
            skCircle(sketch, "E18.32.5.0", {"center": v(42.62, 14.44) * mm, "radius": 0.25 * mm});
            skCircle(sketch, "E18.34.5.0", {"center": v(45.16, 14.44) * mm, "radius": 0.25 * mm});
            skCircle(sketch, "E18.36.5.0", {"center": v(47.7, 14.44) * mm, "radius": 0.25 * mm});
            skCircle(sketch, "E18.38.5.0", {"center": v(50.24, 14.44) * mm, "radius": 0.25 * mm});
            skCircle(sketch, "E18.40.5.0", {"center": v(52.78, 14.44) * mm, "radius": 0.25 * mm});
            skCircle(sketch, "E18.42.5.0", {"center": v(55.32, 14.44) * mm, "radius": 0.25 * mm});
            skCircle(sketch, "E18.44.5.0", {"center": v(57.86, 14.44) * mm, "radius": 0.25 * mm});
            skCircle(sketch, "E18.46.5.0", {"center": v(60.4, 14.44) * mm, "radius": 0.25 * mm});
            skCircle(sketch, "E18.48.5.0", {"center": v(62.94, 14.44) * mm, "radius": 0.25 * mm});
            skCircle(sketch, "E18.50.5.0", {"center": v(65.48, 14.44) * mm, "radius": 0.25 * mm});
            skCircle(sketch, "E18.52.5.0", {"center": v(68.02, 14.44) * mm, "radius": 0.25 * mm});
            skCircle(sketch, "E18.0.6.0", {"center": v(1.98, 16.98) * mm, "radius": 0.25 * mm});
            skCircle(sketch, "E18.2.6.0", {"center": v(4.52, 16.98) * mm, "radius": 0.25 * mm});
            skCircle(sketch, "E18.4.6.0", {"center": v(7.06, 16.98) * mm, "radius": 0.25 * mm});
            skCircle(sketch, "E18.6.6.0", {"center": v(9.6, 16.98) * mm, "radius": 0.25 * mm});
            skCircle(sketch, "E18.8.6.0", {"center": v(12.14, 16.98) * mm, "radius": 0.25 * mm});
            skCircle(sketch, "E18.10.6.0", {"center": v(14.68, 16.98) * mm, "radius": 0.25 * mm});
            skCircle(sketch, "E18.12.6.0", {"center": v(17.22, 16.98) * mm, "radius": 0.25 * mm});
            skCircle(sketch, "E18.14.6.0", {"center": v(19.76, 16.98) * mm, "radius": 0.25 * mm});
            skCircle(sketch, "E18.16.6.0", {"center": v(22.3, 16.98) * mm, "radius": 0.25 * mm});
            skCircle(sketch, "E18.18.6.0", {"center": v(24.84, 16.98) * mm, "radius": 0.25 * mm});
            skCircle(sketch, "E18.20.6.0", {"center": v(27.38, 16.98) * mm, "radius": 0.25 * mm});
            skCircle(sketch, "E18.22.6.0", {"center": v(29.92, 16.98) * mm, "radius": 0.25 * mm});
            skCircle(sketch, "E18.24.6.0", {"center": v(32.46, 16.98) * mm, "radius": 0.25 * mm});
            skCircle(sketch, "E18.26.6.0", {"center": v(35, 16.98) * mm, "radius": 0.25 * mm});
            skCircle(sketch, "E18.28.6.0", {"center": v(37.54, 16.98) * mm, "radius": 0.25 * mm});
            skCircle(sketch, "E18.30.6.0", {"center": v(40.08, 16.98) * mm, "radius": 0.25 * mm});
            skCircle(sketch, "E18.32.6.0", {"center": v(42.62, 16.98) * mm, "radius": 0.25 * mm});
            skCircle(sketch, "E18.34.6.0", {"center": v(45.16, 16.98) * mm, "radius": 0.25 * mm});
            skCircle(sketch, "E18.36.6.0", {"center": v(47.7, 16.98) * mm, "radius": 0.25 * mm});
            skCircle(sketch, "E18.38.6.0", {"center": v(50.24, 16.98) * mm, "radius": 0.25 * mm});
            skCircle(sketch, "E18.40.6.0", {"center": v(52.78, 16.98) * mm, "radius": 0.25 * mm});
            skCircle(sketch, "E18.42.6.0", {"center": v(55.32, 16.98) * mm, "radius": 0.25 * mm});
            skCircle(sketch, "E18.44.6.0", {"center": v(57.86, 16.98) * mm, "radius": 0.25 * mm});
            skCircle(sketch, "E18.46.6.0", {"center": v(60.4, 16.98) * mm, "radius": 0.25 * mm});
            skCircle(sketch, "E18.48.6.0", {"center": v(62.94, 16.98) * mm, "radius": 0.25 * mm});
            skCircle(sketch, "E18.50.6.0", {"center": v(65.48, 16.98) * mm, "radius": 0.25 * mm});
            skCircle(sketch, "E18.52.6.0", {"center": v(68.02, 16.98) * mm, "radius": 0.25 * mm});
            skCircle(sketch, "E18.0.7.0", {"center": v(1.98, 19.52) * mm, "radius": 0.25 * mm});
            skCircle(sketch, "E18.2.7.0", {"center": v(4.52, 19.52) * mm, "radius": 0.25 * mm});
            skCircle(sketch, "E18.4.7.0", {"center": v(7.06, 19.52) * mm, "radius": 0.25 * mm});
            skCircle(sketch, "E18.6.7.0", {"center": v(9.6, 19.52) * mm, "radius": 0.25 * mm});
            skCircle(sketch, "E18.8.7.0", {"center": v(12.14, 19.52) * mm, "radius": 0.25 * mm});
            skCircle(sketch, "E18.10.7.0", {"center": v(14.68, 19.52) * mm, "radius": 0.25 * mm});
            skCircle(sketch, "E18.12.7.0", {"center": v(17.22, 19.52) * mm, "radius": 0.25 * mm});
            skCircle(sketch, "E18.14.7.0", {"center": v(19.76, 19.52) * mm, "radius": 0.25 * mm});
            skCircle(sketch, "E18.16.7.0", {"center": v(22.3, 19.52) * mm, "radius": 0.25 * mm});
            skCircle(sketch, "E18.18.7.0", {"center": v(24.84, 19.52) * mm, "radius": 0.25 * mm});
            skCircle(sketch, "E18.20.7.0", {"center": v(27.38, 19.52) * mm, "radius": 0.25 * mm});
            skCircle(sketch, "E18.22.7.0", {"center": v(29.92, 19.52) * mm, "radius": 0.25 * mm});
            skCircle(sketch, "E18.24.7.0", {"center": v(32.46, 19.52) * mm, "radius": 0.25 * mm});
            skCircle(sketch, "E18.26.7.0", {"center": v(35, 19.52) * mm, "radius": 0.25 * mm});
            skCircle(sketch, "E18.28.7.0", {"center": v(37.54, 19.52) * mm, "radius": 0.25 * mm});
            skCircle(sketch, "E18.30.7.0", {"center": v(40.08, 19.52) * mm, "radius": 0.25 * mm});
            skCircle(sketch, "E18.32.7.0", {"center": v(42.62, 19.52) * mm, "radius": 0.25 * mm});
            skCircle(sketch, "E18.34.7.0", {"center": v(45.16, 19.52) * mm, "radius": 0.25 * mm});
            skCircle(sketch, "E18.36.7.0", {"center": v(47.7, 19.52) * mm, "radius": 0.25 * mm});
            skCircle(sketch, "E18.38.7.0", {"center": v(50.24, 19.52) * mm, "radius": 0.25 * mm});
            skCircle(sketch, "E18.40.7.0", {"center": v(52.78, 19.52) * mm, "radius": 0.25 * mm});
            skCircle(sketch, "E18.42.7.0", {"center": v(55.32, 19.52) * mm, "radius": 0.25 * mm});
            skCircle(sketch, "E18.44.7.0", {"center": v(57.86, 19.52) * mm, "radius": 0.25 * mm});
            skCircle(sketch, "E18.46.7.0", {"center": v(60.4, 19.52) * mm, "radius": 0.25 * mm});
            skCircle(sketch, "E18.48.7.0", {"center": v(62.94, 19.52) * mm, "radius": 0.25 * mm});
            skCircle(sketch, "E18.50.7.0", {"center": v(65.48, 19.52) * mm, "radius": 0.25 * mm});
            skCircle(sketch, "E18.52.7.0", {"center": v(68.02, 19.52) * mm, "radius": 0.25 * mm});
            skCircle(sketch, "E18.0.8.0", {"center": v(1.98, 22.06) * mm, "radius": 0.25 * mm});
            skCircle(sketch, "E18.2.8.0", {"center": v(4.52, 22.06) * mm, "radius": 0.25 * mm});
            skCircle(sketch, "E18.4.8.0", {"center": v(7.06, 22.06) * mm, "radius": 0.25 * mm});
            skCircle(sketch, "E18.6.8.0", {"center": v(9.6, 22.06) * mm, "radius": 0.25 * mm});
            skCircle(sketch, "E18.8.8.0", {"center": v(12.14, 22.06) * mm, "radius": 0.25 * mm});
            skCircle(sketch, "E18.10.8.0", {"center": v(14.68, 22.06) * mm, "radius": 0.25 * mm});
            skCircle(sketch, "E18.12.8.0", {"center": v(17.22, 22.06) * mm, "radius": 0.25 * mm});
            skCircle(sketch, "E18.14.8.0", {"center": v(19.76, 22.06) * mm, "radius": 0.25 * mm});
            skCircle(sketch, "E18.16.8.0", {"center": v(22.3, 22.06) * mm, "radius": 0.25 * mm});
            skCircle(sketch, "E18.18.8.0", {"center": v(24.84, 22.06) * mm, "radius": 0.25 * mm});
            skCircle(sketch, "E18.20.8.0", {"center": v(27.38, 22.06) * mm, "radius": 0.25 * mm});
            skCircle(sketch, "E18.22.8.0", {"center": v(29.92, 22.06) * mm, "radius": 0.25 * mm});
            skCircle(sketch, "E18.24.8.0", {"center": v(32.46, 22.06) * mm, "radius": 0.25 * mm});
            skCircle(sketch, "E18.26.8.0", {"center": v(35, 22.06) * mm, "radius": 0.25 * mm});
            skCircle(sketch, "E18.28.8.0", {"center": v(37.54, 22.06) * mm, "radius": 0.25 * mm});
            skCircle(sketch, "E18.30.8.0", {"center": v(40.08, 22.06) * mm, "radius": 0.25 * mm});
            skCircle(sketch, "E18.32.8.0", {"center": v(42.62, 22.06) * mm, "radius": 0.25 * mm});
            skCircle(sketch, "E18.34.8.0", {"center": v(45.16, 22.06) * mm, "radius": 0.25 * mm});
            skCircle(sketch, "E18.36.8.0", {"center": v(47.7, 22.06) * mm, "radius": 0.25 * mm});
            skCircle(sketch, "E18.38.8.0", {"center": v(50.24, 22.06) * mm, "radius": 0.25 * mm});
            skCircle(sketch, "E18.40.8.0", {"center": v(52.78, 22.06) * mm, "radius": 0.25 * mm});
            skCircle(sketch, "E18.42.8.0", {"center": v(55.32, 22.06) * mm, "radius": 0.25 * mm});
            skCircle(sketch, "E18.44.8.0", {"center": v(57.86, 22.06) * mm, "radius": 0.25 * mm});
            skCircle(sketch, "E18.46.8.0", {"center": v(60.4, 22.06) * mm, "radius": 0.25 * mm});
            skCircle(sketch, "E18.48.8.0", {"center": v(62.94, 22.06) * mm, "radius": 0.25 * mm});
            skCircle(sketch, "E18.50.8.0", {"center": v(65.48, 22.06) * mm, "radius": 0.25 * mm});
            skCircle(sketch, "E18.52.8.0", {"center": v(68.02, 22.06) * mm, "radius": 0.25 * mm});
            skCircle(sketch, "E18.0.9.0", {"center": v(1.98, 24.6) * mm, "radius": 0.25 * mm});
            skCircle(sketch, "E18.2.9.0", {"center": v(4.52, 24.6) * mm, "radius": 0.25 * mm});
            skCircle(sketch, "E18.4.9.0", {"center": v(7.06, 24.6) * mm, "radius": 0.25 * mm});
            skCircle(sketch, "E18.6.9.0", {"center": v(9.6, 24.6) * mm, "radius": 0.25 * mm});
            skCircle(sketch, "E18.8.9.0", {"center": v(12.14, 24.6) * mm, "radius": 0.25 * mm});
            skCircle(sketch, "E18.10.9.0", {"center": v(14.68, 24.6) * mm, "radius": 0.25 * mm});
            skCircle(sketch, "E18.12.9.0", {"center": v(17.22, 24.6) * mm, "radius": 0.25 * mm});
            skCircle(sketch, "E18.14.9.0", {"center": v(19.76, 24.6) * mm, "radius": 0.25 * mm});
            skCircle(sketch, "E18.16.9.0", {"center": v(22.3, 24.6) * mm, "radius": 0.25 * mm});
            skCircle(sketch, "E18.18.9.0", {"center": v(24.84, 24.6) * mm, "radius": 0.25 * mm});
            skCircle(sketch, "E18.20.9.0", {"center": v(27.38, 24.6) * mm, "radius": 0.25 * mm});
            skCircle(sketch, "E18.22.9.0", {"center": v(29.92, 24.6) * mm, "radius": 0.25 * mm});
            skCircle(sketch, "E18.24.9.0", {"center": v(32.46, 24.6) * mm, "radius": 0.25 * mm});
            skCircle(sketch, "E18.26.9.0", {"center": v(35, 24.6) * mm, "radius": 0.25 * mm});
            skCircle(sketch, "E18.28.9.0", {"center": v(37.54, 24.6) * mm, "radius": 0.25 * mm});
            skCircle(sketch, "E18.30.9.0", {"center": v(40.08, 24.6) * mm, "radius": 0.25 * mm});
            skCircle(sketch, "E18.32.9.0", {"center": v(42.62, 24.6) * mm, "radius": 0.25 * mm});
            skCircle(sketch, "E18.34.9.0", {"center": v(45.16, 24.6) * mm, "radius": 0.25 * mm});
            skCircle(sketch, "E18.36.9.0", {"center": v(47.7, 24.6) * mm, "radius": 0.25 * mm});
            skCircle(sketch, "E18.38.9.0", {"center": v(50.24, 24.6) * mm, "radius": 0.25 * mm});
            skCircle(sketch, "E18.40.9.0", {"center": v(52.78, 24.6) * mm, "radius": 0.25 * mm});
            skCircle(sketch, "E18.42.9.0", {"center": v(55.32, 24.6) * mm, "radius": 0.25 * mm});
            skCircle(sketch, "E18.44.9.0", {"center": v(57.86, 24.6) * mm, "radius": 0.25 * mm});
            skCircle(sketch, "E18.46.9.0", {"center": v(60.4, 24.6) * mm, "radius": 0.25 * mm});
            skCircle(sketch, "E18.48.9.0", {"center": v(62.94, 24.6) * mm, "radius": 0.25 * mm});
            skCircle(sketch, "E18.50.9.0", {"center": v(65.48, 24.6) * mm, "radius": 0.25 * mm});
            skCircle(sketch, "E18.52.9.0", {"center": v(68.02, 24.6) * mm, "radius": 0.25 * mm});
            skCircle(sketch, "E18.0.10.0", {"center": v(1.98, 27.14) * mm, "radius": 0.25 * mm});
            skCircle(sketch, "E18.2.10.0", {"center": v(4.52, 27.14) * mm, "radius": 0.25 * mm});
            skCircle(sketch, "E18.4.10.0", {"center": v(7.06, 27.14) * mm, "radius": 0.25 * mm});
            skCircle(sketch, "E18.6.10.0", {"center": v(9.6, 27.14) * mm, "radius": 0.25 * mm});
            skCircle(sketch, "E18.8.10.0", {"center": v(12.14, 27.14) * mm, "radius": 0.25 * mm});
            skCircle(sketch, "E18.10.10.0", {"center": v(14.68, 27.14) * mm, "radius": 0.25 * mm});
            skCircle(sketch, "E18.12.10.0", {"center": v(17.22, 27.14) * mm, "radius": 0.25 * mm});
            skCircle(sketch, "E18.14.10.0", {"center": v(19.76, 27.14) * mm, "radius": 0.25 * mm});
            skCircle(sketch, "E18.16.10.0", {"center": v(22.3, 27.14) * mm, "radius": 0.25 * mm});
            skCircle(sketch, "E18.18.10.0", {"center": v(24.84, 27.14) * mm, "radius": 0.25 * mm});
            skCircle(sketch, "E18.20.10.0", {"center": v(27.38, 27.14) * mm, "radius": 0.25 * mm});
            skCircle(sketch, "E18.22.10.0", {"center": v(29.92, 27.14) * mm, "radius": 0.25 * mm});
            skCircle(sketch, "E18.24.10.0", {"center": v(32.46, 27.14) * mm, "radius": 0.25 * mm});
            skCircle(sketch, "E18.26.10.0", {"center": v(35, 27.14) * mm, "radius": 0.25 * mm});
            skCircle(sketch, "E18.28.10.0", {"center": v(37.54, 27.14) * mm, "radius": 0.25 * mm});
            skCircle(sketch, "E18.30.10.0", {"center": v(40.08, 27.14) * mm, "radius": 0.25 * mm});
            skCircle(sketch, "E18.32.10.0", {"center": v(42.62, 27.14) * mm, "radius": 0.25 * mm});
            skCircle(sketch, "E18.34.10.0", {"center": v(45.16, 27.14) * mm, "radius": 0.25 * mm});
            skCircle(sketch, "E18.36.10.0", {"center": v(47.7, 27.14) * mm, "radius": 0.25 * mm});
            skCircle(sketch, "E18.38.10.0", {"center": v(50.24, 27.14) * mm, "radius": 0.25 * mm});
            skCircle(sketch, "E18.40.10.0", {"center": v(52.78, 27.14) * mm, "radius": 0.25 * mm});
            skCircle(sketch, "E18.42.10.0", {"center": v(55.32, 27.14) * mm, "radius": 0.25 * mm});
            skCircle(sketch, "E18.44.10.0", {"center": v(57.86, 27.14) * mm, "radius": 0.25 * mm});
            skCircle(sketch, "E18.46.10.0", {"center": v(60.4, 27.14) * mm, "radius": 0.25 * mm});
            skCircle(sketch, "E18.48.10.0", {"center": v(62.94, 27.14) * mm, "radius": 0.25 * mm});
            skCircle(sketch, "E18.50.10.0", {"center": v(65.48, 27.14) * mm, "radius": 0.25 * mm});
            skCircle(sketch, "E18.52.10.0", {"center": v(68.02, 27.14) * mm, "radius": 0.25 * mm});
            skCircle(sketch, "E18.0.11.0", {"center": v(1.98, 29.68) * mm, "radius": 0.25 * mm});
            skCircle(sketch, "E18.2.11.0", {"center": v(4.52, 29.68) * mm, "radius": 0.25 * mm});
            skCircle(sketch, "E18.4.11.0", {"center": v(7.06, 29.68) * mm, "radius": 0.25 * mm});
            skCircle(sketch, "E18.6.11.0", {"center": v(9.6, 29.68) * mm, "radius": 0.25 * mm});
            skCircle(sketch, "E18.8.11.0", {"center": v(12.14, 29.68) * mm, "radius": 0.25 * mm});
            skCircle(sketch, "E18.10.11.0", {"center": v(14.68, 29.68) * mm, "radius": 0.25 * mm});
            skCircle(sketch, "E18.12.11.0", {"center": v(17.22, 29.68) * mm, "radius": 0.25 * mm});
            skCircle(sketch, "E18.14.11.0", {"center": v(19.76, 29.68) * mm, "radius": 0.25 * mm});
            skCircle(sketch, "E18.16.11.0", {"center": v(22.3, 29.68) * mm, "radius": 0.25 * mm});
            skCircle(sketch, "E18.18.11.0", {"center": v(24.84, 29.68) * mm, "radius": 0.25 * mm});
            skCircle(sketch, "E18.20.11.0", {"center": v(27.38, 29.68) * mm, "radius": 0.25 * mm});
            skCircle(sketch, "E18.22.11.0", {"center": v(29.92, 29.68) * mm, "radius": 0.25 * mm});
            skCircle(sketch, "E18.24.11.0", {"center": v(32.46, 29.68) * mm, "radius": 0.25 * mm});
            skCircle(sketch, "E18.26.11.0", {"center": v(35, 29.68) * mm, "radius": 0.25 * mm});
            skCircle(sketch, "E18.28.11.0", {"center": v(37.54, 29.68) * mm, "radius": 0.25 * mm});
            skCircle(sketch, "E18.30.11.0", {"center": v(40.08, 29.68) * mm, "radius": 0.25 * mm});
            skCircle(sketch, "E18.32.11.0", {"center": v(42.62, 29.68) * mm, "radius": 0.25 * mm});
            skCircle(sketch, "E18.34.11.0", {"center": v(45.16, 29.68) * mm, "radius": 0.25 * mm});
            skCircle(sketch, "E18.36.11.0", {"center": v(47.7, 29.68) * mm, "radius": 0.25 * mm});
            skCircle(sketch, "E18.38.11.0", {"center": v(50.24, 29.68) * mm, "radius": 0.25 * mm});
            skCircle(sketch, "E18.40.11.0", {"center": v(52.78, 29.68) * mm, "radius": 0.25 * mm});
            skCircle(sketch, "E18.42.11.0", {"center": v(55.32, 29.68) * mm, "radius": 0.25 * mm});
            skCircle(sketch, "E18.44.11.0", {"center": v(57.86, 29.68) * mm, "radius": 0.25 * mm});
            skCircle(sketch, "E18.46.11.0", {"center": v(60.4, 29.68) * mm, "radius": 0.25 * mm});
            skCircle(sketch, "E18.48.11.0", {"center": v(62.94, 29.68) * mm, "radius": 0.25 * mm});
            skCircle(sketch, "E18.50.11.0", {"center": v(65.48, 29.68) * mm, "radius": 0.25 * mm});
            skCircle(sketch, "E18.52.11.0", {"center": v(68.02, 29.68) * mm, "radius": 0.25 * mm});
            skCircle(sketch, "E18.0.12.0", {"center": v(1.98, 32.22) * mm, "radius": 0.25 * mm});
            skCircle(sketch, "E18.2.12.0", {"center": v(4.52, 32.22) * mm, "radius": 0.25 * mm});
            skCircle(sketch, "E18.4.12.0", {"center": v(7.06, 32.22) * mm, "radius": 0.25 * mm});
            skCircle(sketch, "E18.6.12.0", {"center": v(9.6, 32.22) * mm, "radius": 0.25 * mm});
            skCircle(sketch, "E18.8.12.0", {"center": v(12.14, 32.22) * mm, "radius": 0.25 * mm});
            skCircle(sketch, "E18.10.12.0", {"center": v(14.68, 32.22) * mm, "radius": 0.25 * mm});
            skCircle(sketch, "E18.12.12.0", {"center": v(17.22, 32.22) * mm, "radius": 0.25 * mm});
            skCircle(sketch, "E18.14.12.0", {"center": v(19.76, 32.22) * mm, "radius": 0.25 * mm});
            skCircle(sketch, "E18.16.12.0", {"center": v(22.3, 32.22) * mm, "radius": 0.25 * mm});
            skCircle(sketch, "E18.18.12.0", {"center": v(24.84, 32.22) * mm, "radius": 0.25 * mm});
            skCircle(sketch, "E18.20.12.0", {"center": v(27.38, 32.22) * mm, "radius": 0.25 * mm});
            skCircle(sketch, "E18.22.12.0", {"center": v(29.92, 32.22) * mm, "radius": 0.25 * mm});
            skCircle(sketch, "E18.24.12.0", {"center": v(32.46, 32.22) * mm, "radius": 0.25 * mm});
            skCircle(sketch, "E18.26.12.0", {"center": v(35, 32.22) * mm, "radius": 0.25 * mm});
            skCircle(sketch, "E18.28.12.0", {"center": v(37.54, 32.22) * mm, "radius": 0.25 * mm});
            skCircle(sketch, "E18.30.12.0", {"center": v(40.08, 32.22) * mm, "radius": 0.25 * mm});
            skCircle(sketch, "E18.32.12.0", {"center": v(42.62, 32.22) * mm, "radius": 0.25 * mm});
            skCircle(sketch, "E18.34.12.0", {"center": v(45.16, 32.22) * mm, "radius": 0.25 * mm});
            skCircle(sketch, "E18.36.12.0", {"center": v(47.7, 32.22) * mm, "radius": 0.25 * mm});
            skCircle(sketch, "E18.38.12.0", {"center": v(50.24, 32.22) * mm, "radius": 0.25 * mm});
            skCircle(sketch, "E18.40.12.0", {"center": v(52.78, 32.22) * mm, "radius": 0.25 * mm});
            skCircle(sketch, "E18.42.12.0", {"center": v(55.32, 32.22) * mm, "radius": 0.25 * mm});
            skCircle(sketch, "E18.44.12.0", {"center": v(57.86, 32.22) * mm, "radius": 0.25 * mm});
            skCircle(sketch, "E18.46.12.0", {"center": v(60.4, 32.22) * mm, "radius": 0.25 * mm});
            skCircle(sketch, "E18.48.12.0", {"center": v(62.94, 32.22) * mm, "radius": 0.25 * mm});
            skCircle(sketch, "E18.50.12.0", {"center": v(65.48, 32.22) * mm, "radius": 0.25 * mm});
            skCircle(sketch, "E18.52.12.0", {"center": v(68.02, 32.22) * mm, "radius": 0.25 * mm});
            skCircle(sketch, "E18.0.13.0", {"center": v(1.98, 34.76) * mm, "radius": 0.25 * mm});
            skCircle(sketch, "E18.2.13.0", {"center": v(4.52, 34.76) * mm, "radius": 0.25 * mm});
            skCircle(sketch, "E18.4.13.0", {"center": v(7.06, 34.76) * mm, "radius": 0.25 * mm});
            skCircle(sketch, "E18.6.13.0", {"center": v(9.6, 34.76) * mm, "radius": 0.25 * mm});
            skCircle(sketch, "E18.8.13.0", {"center": v(12.14, 34.76) * mm, "radius": 0.25 * mm});
            skCircle(sketch, "E18.10.13.0", {"center": v(14.68, 34.76) * mm, "radius": 0.25 * mm});
            skCircle(sketch, "E18.12.13.0", {"center": v(17.22, 34.76) * mm, "radius": 0.25 * mm});
            skCircle(sketch, "E18.14.13.0", {"center": v(19.76, 34.76) * mm, "radius": 0.25 * mm});
            skCircle(sketch, "E18.16.13.0", {"center": v(22.3, 34.76) * mm, "radius": 0.25 * mm});
            skCircle(sketch, "E18.18.13.0", {"center": v(24.84, 34.76) * mm, "radius": 0.25 * mm});
            skCircle(sketch, "E18.20.13.0", {"center": v(27.38, 34.76) * mm, "radius": 0.25 * mm});
            skCircle(sketch, "E18.22.13.0", {"center": v(29.92, 34.76) * mm, "radius": 0.25 * mm});
            skCircle(sketch, "E18.24.13.0", {"center": v(32.46, 34.76) * mm, "radius": 0.25 * mm});
            skCircle(sketch, "E18.26.13.0", {"center": v(35, 34.76) * mm, "radius": 0.25 * mm});
            skCircle(sketch, "E18.28.13.0", {"center": v(37.54, 34.76) * mm, "radius": 0.25 * mm});
            skCircle(sketch, "E18.30.13.0", {"center": v(40.08, 34.76) * mm, "radius": 0.25 * mm});
            skCircle(sketch, "E18.32.13.0", {"center": v(42.62, 34.76) * mm, "radius": 0.25 * mm});
            skCircle(sketch, "E18.34.13.0", {"center": v(45.16, 34.76) * mm, "radius": 0.25 * mm});
            skCircle(sketch, "E18.36.13.0", {"center": v(47.7, 34.76) * mm, "radius": 0.25 * mm});
            skCircle(sketch, "E18.38.13.0", {"center": v(50.24, 34.76) * mm, "radius": 0.25 * mm});
            skCircle(sketch, "E18.40.13.0", {"center": v(52.78, 34.76) * mm, "radius": 0.25 * mm});
            skCircle(sketch, "E18.42.13.0", {"center": v(55.32, 34.76) * mm, "radius": 0.25 * mm});
            skCircle(sketch, "E18.44.13.0", {"center": v(57.86, 34.76) * mm, "radius": 0.25 * mm});
            skCircle(sketch, "E18.46.13.0", {"center": v(60.4, 34.76) * mm, "radius": 0.25 * mm});
            skCircle(sketch, "E18.48.13.0", {"center": v(62.94, 34.76) * mm, "radius": 0.25 * mm});
            skCircle(sketch, "E18.50.13.0", {"center": v(65.48, 34.76) * mm, "radius": 0.25 * mm});
            skCircle(sketch, "E18.52.13.0", {"center": v(68.02, 34.76) * mm, "radius": 0.25 * mm});
            skCircle(sketch, "E18.0.14.0", {"center": v(1.98, 37.3) * mm, "radius": 0.25 * mm});
            skCircle(sketch, "E18.2.14.0", {"center": v(4.52, 37.3) * mm, "radius": 0.25 * mm});
            skCircle(sketch, "E18.4.14.0", {"center": v(7.06, 37.3) * mm, "radius": 0.25 * mm});
            skCircle(sketch, "E18.6.14.0", {"center": v(9.6, 37.3) * mm, "radius": 0.25 * mm});
            skCircle(sketch, "E18.8.14.0", {"center": v(12.14, 37.3) * mm, "radius": 0.25 * mm});
            skCircle(sketch, "E18.10.14.0", {"center": v(14.68, 37.3) * mm, "radius": 0.25 * mm});
            skCircle(sketch, "E18.12.14.0", {"center": v(17.22, 37.3) * mm, "radius": 0.25 * mm});
            skCircle(sketch, "E18.14.14.0", {"center": v(19.76, 37.3) * mm, "radius": 0.25 * mm});
            skCircle(sketch, "E18.16.14.0", {"center": v(22.3, 37.3) * mm, "radius": 0.25 * mm});
            skCircle(sketch, "E18.18.14.0", {"center": v(24.84, 37.3) * mm, "radius": 0.25 * mm});
            skCircle(sketch, "E18.20.14.0", {"center": v(27.38, 37.3) * mm, "radius": 0.25 * mm});
            skCircle(sketch, "E18.22.14.0", {"center": v(29.92, 37.3) * mm, "radius": 0.25 * mm});
            skCircle(sketch, "E18.24.14.0", {"center": v(32.46, 37.3) * mm, "radius": 0.25 * mm});
            skCircle(sketch, "E18.26.14.0", {"center": v(35, 37.3) * mm, "radius": 0.25 * mm});
            skCircle(sketch, "E18.28.14.0", {"center": v(37.54, 37.3) * mm, "radius": 0.25 * mm});
            skCircle(sketch, "E18.30.14.0", {"center": v(40.08, 37.3) * mm, "radius": 0.25 * mm});
            skCircle(sketch, "E18.32.14.0", {"center": v(42.62, 37.3) * mm, "radius": 0.25 * mm});
            skCircle(sketch, "E18.34.14.0", {"center": v(45.16, 37.3) * mm, "radius": 0.25 * mm});
            skCircle(sketch, "E18.36.14.0", {"center": v(47.7, 37.3) * mm, "radius": 0.25 * mm});
            skCircle(sketch, "E18.38.14.0", {"center": v(50.24, 37.3) * mm, "radius": 0.25 * mm});
            skCircle(sketch, "E18.40.14.0", {"center": v(52.78, 37.3) * mm, "radius": 0.25 * mm});
            skCircle(sketch, "E18.42.14.0", {"center": v(55.32, 37.3) * mm, "radius": 0.25 * mm});
            skCircle(sketch, "E18.44.14.0", {"center": v(57.86, 37.3) * mm, "radius": 0.25 * mm});
            skCircle(sketch, "E18.46.14.0", {"center": v(60.4, 37.3) * mm, "radius": 0.25 * mm});
            skCircle(sketch, "E18.48.14.0", {"center": v(62.94, 37.3) * mm, "radius": 0.25 * mm});
            skCircle(sketch, "E18.50.14.0", {"center": v(65.48, 37.3) * mm, "radius": 0.25 * mm});
            skCircle(sketch, "E18.52.14.0", {"center": v(68.02, 37.3) * mm, "radius": 0.25 * mm});
            skCircle(sketch, "E18.0.15.0", {"center": v(1.98, 39.84) * mm, "radius": 0.25 * mm});
            skCircle(sketch, "E18.2.15.0", {"center": v(4.52, 39.84) * mm, "radius": 0.25 * mm});
            skCircle(sketch, "E18.4.15.0", {"center": v(7.06, 39.84) * mm, "radius": 0.25 * mm});
            skCircle(sketch, "E18.6.15.0", {"center": v(9.6, 39.84) * mm, "radius": 0.25 * mm});
            skCircle(sketch, "E18.8.15.0", {"center": v(12.14, 39.84) * mm, "radius": 0.25 * mm});
            skCircle(sketch, "E18.10.15.0", {"center": v(14.68, 39.84) * mm, "radius": 0.25 * mm});
            skCircle(sketch, "E18.12.15.0", {"center": v(17.22, 39.84) * mm, "radius": 0.25 * mm});
            skCircle(sketch, "E18.14.15.0", {"center": v(19.76, 39.84) * mm, "radius": 0.25 * mm});
            skCircle(sketch, "E18.16.15.0", {"center": v(22.3, 39.84) * mm, "radius": 0.25 * mm});
            skCircle(sketch, "E18.18.15.0", {"center": v(24.84, 39.84) * mm, "radius": 0.25 * mm});
            skCircle(sketch, "E18.20.15.0", {"center": v(27.38, 39.84) * mm, "radius": 0.25 * mm});
            skCircle(sketch, "E18.22.15.0", {"center": v(29.92, 39.84) * mm, "radius": 0.25 * mm});
            skCircle(sketch, "E18.24.15.0", {"center": v(32.46, 39.84) * mm, "radius": 0.25 * mm});
            skCircle(sketch, "E18.26.15.0", {"center": v(35, 39.84) * mm, "radius": 0.25 * mm});
            skCircle(sketch, "E18.28.15.0", {"center": v(37.54, 39.84) * mm, "radius": 0.25 * mm});
            skCircle(sketch, "E18.30.15.0", {"center": v(40.08, 39.84) * mm, "radius": 0.25 * mm});
            skCircle(sketch, "E18.32.15.0", {"center": v(42.62, 39.84) * mm, "radius": 0.25 * mm});
            skCircle(sketch, "E18.34.15.0", {"center": v(45.16, 39.84) * mm, "radius": 0.25 * mm});
            skCircle(sketch, "E18.36.15.0", {"center": v(47.7, 39.84) * mm, "radius": 0.25 * mm});
            skCircle(sketch, "E18.38.15.0", {"center": v(50.24, 39.84) * mm, "radius": 0.25 * mm});
            skCircle(sketch, "E18.40.15.0", {"center": v(52.78, 39.84) * mm, "radius": 0.25 * mm});
            skCircle(sketch, "E18.42.15.0", {"center": v(55.32, 39.84) * mm, "radius": 0.25 * mm});
            skCircle(sketch, "E18.44.15.0", {"center": v(57.86, 39.84) * mm, "radius": 0.25 * mm});
            skCircle(sketch, "E18.46.15.0", {"center": v(60.4, 39.84) * mm, "radius": 0.25 * mm});
            skCircle(sketch, "E18.48.15.0", {"center": v(62.94, 39.84) * mm, "radius": 0.25 * mm});
            skCircle(sketch, "E18.50.15.0", {"center": v(65.48, 39.84) * mm, "radius": 0.25 * mm});
            skCircle(sketch, "E18.52.15.0", {"center": v(68.02, 39.84) * mm, "radius": 0.25 * mm});
            skCircle(sketch, "E18.0.16.0", {"center": v(1.98, 42.38) * mm, "radius": 0.25 * mm});
            skCircle(sketch, "E18.2.16.0", {"center": v(4.52, 42.38) * mm, "radius": 0.25 * mm});
            skCircle(sketch, "E18.4.16.0", {"center": v(7.06, 42.38) * mm, "radius": 0.25 * mm});
            skCircle(sketch, "E18.6.16.0", {"center": v(9.6, 42.38) * mm, "radius": 0.25 * mm});
            skCircle(sketch, "E18.8.16.0", {"center": v(12.14, 42.38) * mm, "radius": 0.25 * mm});
            skCircle(sketch, "E18.10.16.0", {"center": v(14.68, 42.38) * mm, "radius": 0.25 * mm});
            skCircle(sketch, "E18.12.16.0", {"center": v(17.22, 42.38) * mm, "radius": 0.25 * mm});
            skCircle(sketch, "E18.14.16.0", {"center": v(19.76, 42.38) * mm, "radius": 0.25 * mm});
            skCircle(sketch, "E18.16.16.0", {"center": v(22.3, 42.38) * mm, "radius": 0.25 * mm});
            skCircle(sketch, "E18.18.16.0", {"center": v(24.84, 42.38) * mm, "radius": 0.25 * mm});
            skCircle(sketch, "E18.20.16.0", {"center": v(27.38, 42.38) * mm, "radius": 0.25 * mm});
            skCircle(sketch, "E18.22.16.0", {"center": v(29.92, 42.38) * mm, "radius": 0.25 * mm});
            skCircle(sketch, "E18.24.16.0", {"center": v(32.46, 42.38) * mm, "radius": 0.25 * mm});
            skCircle(sketch, "E18.26.16.0", {"center": v(35, 42.38) * mm, "radius": 0.25 * mm});
            skCircle(sketch, "E18.28.16.0", {"center": v(37.54, 42.38) * mm, "radius": 0.25 * mm});
            skCircle(sketch, "E18.30.16.0", {"center": v(40.08, 42.38) * mm, "radius": 0.25 * mm});
            skCircle(sketch, "E18.32.16.0", {"center": v(42.62, 42.38) * mm, "radius": 0.25 * mm});
            skCircle(sketch, "E18.34.16.0", {"center": v(45.16, 42.38) * mm, "radius": 0.25 * mm});
            skCircle(sketch, "E18.36.16.0", {"center": v(47.7, 42.38) * mm, "radius": 0.25 * mm});
            skCircle(sketch, "E18.38.16.0", {"center": v(50.24, 42.38) * mm, "radius": 0.25 * mm});
            skCircle(sketch, "E18.40.16.0", {"center": v(52.78, 42.38) * mm, "radius": 0.25 * mm});
            skCircle(sketch, "E18.42.16.0", {"center": v(55.32, 42.38) * mm, "radius": 0.25 * mm});
            skCircle(sketch, "E18.44.16.0", {"center": v(57.86, 42.38) * mm, "radius": 0.25 * mm});
            skCircle(sketch, "E18.46.16.0", {"center": v(60.4, 42.38) * mm, "radius": 0.25 * mm});
            skCircle(sketch, "E18.48.16.0", {"center": v(62.94, 42.38) * mm, "radius": 0.25 * mm});
            skCircle(sketch, "E18.50.16.0", {"center": v(65.48, 42.38) * mm, "radius": 0.25 * mm});
            skCircle(sketch, "E18.52.16.0", {"center": v(68.02, 42.38) * mm, "radius": 0.25 * mm});
            skCircle(sketch, "E18.0.17.0", {"center": v(1.98, 44.92) * mm, "radius": 0.25 * mm});
            skCircle(sketch, "E18.2.17.0", {"center": v(4.52, 44.92) * mm, "radius": 0.25 * mm});
            skCircle(sketch, "E18.4.17.0", {"center": v(7.06, 44.92) * mm, "radius": 0.25 * mm});
            skCircle(sketch, "E18.6.17.0", {"center": v(9.6, 44.92) * mm, "radius": 0.25 * mm});
            skCircle(sketch, "E18.8.17.0", {"center": v(12.14, 44.92) * mm, "radius": 0.25 * mm});
            skCircle(sketch, "E18.10.17.0", {"center": v(14.68, 44.92) * mm, "radius": 0.25 * mm});
            skCircle(sketch, "E18.12.17.0", {"center": v(17.22, 44.92) * mm, "radius": 0.25 * mm});
            skCircle(sketch, "E18.14.17.0", {"center": v(19.76, 44.92) * mm, "radius": 0.25 * mm});
            skCircle(sketch, "E18.16.17.0", {"center": v(22.3, 44.92) * mm, "radius": 0.25 * mm});
            skCircle(sketch, "E18.18.17.0", {"center": v(24.84, 44.92) * mm, "radius": 0.25 * mm});
            skCircle(sketch, "E18.20.17.0", {"center": v(27.38, 44.92) * mm, "radius": 0.25 * mm});
            skCircle(sketch, "E18.22.17.0", {"center": v(29.92, 44.92) * mm, "radius": 0.25 * mm});
            skCircle(sketch, "E18.24.17.0", {"center": v(32.46, 44.92) * mm, "radius": 0.25 * mm});
            skCircle(sketch, "E18.26.17.0", {"center": v(35, 44.92) * mm, "radius": 0.25 * mm});
            skCircle(sketch, "E18.28.17.0", {"center": v(37.54, 44.92) * mm, "radius": 0.25 * mm});
            skCircle(sketch, "E18.30.17.0", {"center": v(40.08, 44.92) * mm, "radius": 0.25 * mm});
            skCircle(sketch, "E18.32.17.0", {"center": v(42.62, 44.92) * mm, "radius": 0.25 * mm});
            skCircle(sketch, "E18.34.17.0", {"center": v(45.16, 44.92) * mm, "radius": 0.25 * mm});
            skCircle(sketch, "E18.36.17.0", {"center": v(47.7, 44.92) * mm, "radius": 0.25 * mm});
            skCircle(sketch, "E18.38.17.0", {"center": v(50.24, 44.92) * mm, "radius": 0.25 * mm});
            skCircle(sketch, "E18.40.17.0", {"center": v(52.78, 44.92) * mm, "radius": 0.25 * mm});
            skCircle(sketch, "E18.42.17.0", {"center": v(55.32, 44.92) * mm, "radius": 0.25 * mm});
            skCircle(sketch, "E18.44.17.0", {"center": v(57.86, 44.92) * mm, "radius": 0.25 * mm});
            skCircle(sketch, "E18.46.17.0", {"center": v(60.4, 44.92) * mm, "radius": 0.25 * mm});
            skCircle(sketch, "E18.48.17.0", {"center": v(62.94, 44.92) * mm, "radius": 0.25 * mm});
            skCircle(sketch, "E18.50.17.0", {"center": v(65.48, 44.92) * mm, "radius": 0.25 * mm});
            skCircle(sketch, "E18.52.17.0", {"center": v(68.02, 44.92) * mm, "radius": 0.25 * mm});
            skCircle(sketch, "E18.0.18.0", {"center": v(1.98, 47.46) * mm, "radius": 0.25 * mm});
            skCircle(sketch, "E18.2.18.0", {"center": v(4.52, 47.46) * mm, "radius": 0.25 * mm});
            skCircle(sketch, "E18.4.18.0", {"center": v(7.06, 47.46) * mm, "radius": 0.25 * mm});
            skCircle(sketch, "E18.6.18.0", {"center": v(9.6, 47.46) * mm, "radius": 0.25 * mm});
            skCircle(sketch, "E18.8.18.0", {"center": v(12.14, 47.46) * mm, "radius": 0.25 * mm});
            skCircle(sketch, "E18.10.18.0", {"center": v(14.68, 47.46) * mm, "radius": 0.25 * mm});
            skCircle(sketch, "E18.12.18.0", {"center": v(17.22, 47.46) * mm, "radius": 0.25 * mm});
            skCircle(sketch, "E18.14.18.0", {"center": v(19.76, 47.46) * mm, "radius": 0.25 * mm});
            skCircle(sketch, "E18.16.18.0", {"center": v(22.3, 47.46) * mm, "radius": 0.25 * mm});
            skCircle(sketch, "E18.18.18.0", {"center": v(24.84, 47.46) * mm, "radius": 0.25 * mm});
            skCircle(sketch, "E18.20.18.0", {"center": v(27.38, 47.46) * mm, "radius": 0.25 * mm});
            skCircle(sketch, "E18.22.18.0", {"center": v(29.92, 47.46) * mm, "radius": 0.25 * mm});
            skCircle(sketch, "E18.24.18.0", {"center": v(32.46, 47.46) * mm, "radius": 0.25 * mm});
            skCircle(sketch, "E18.26.18.0", {"center": v(35, 47.46) * mm, "radius": 0.25 * mm});
            skCircle(sketch, "E18.28.18.0", {"center": v(37.54, 47.46) * mm, "radius": 0.25 * mm});
            skCircle(sketch, "E18.30.18.0", {"center": v(40.08, 47.46) * mm, "radius": 0.25 * mm});
            skCircle(sketch, "E18.32.18.0", {"center": v(42.62, 47.46) * mm, "radius": 0.25 * mm});
            skCircle(sketch, "E18.34.18.0", {"center": v(45.16, 47.46) * mm, "radius": 0.25 * mm});
            skCircle(sketch, "E18.36.18.0", {"center": v(47.7, 47.46) * mm, "radius": 0.25 * mm});
            skCircle(sketch, "E18.38.18.0", {"center": v(50.24, 47.46) * mm, "radius": 0.25 * mm});
            skCircle(sketch, "E18.40.18.0", {"center": v(52.78, 47.46) * mm, "radius": 0.25 * mm});
            skCircle(sketch, "E18.42.18.0", {"center": v(55.32, 47.46) * mm, "radius": 0.25 * mm});
            skCircle(sketch, "E18.44.18.0", {"center": v(57.86, 47.46) * mm, "radius": 0.25 * mm});
            skCircle(sketch, "E18.46.18.0", {"center": v(60.4, 47.46) * mm, "radius": 0.25 * mm});
            skCircle(sketch, "E18.48.18.0", {"center": v(62.94, 47.46) * mm, "radius": 0.25 * mm});
            skCircle(sketch, "E18.50.18.0", {"center": v(65.48, 47.46) * mm, "radius": 0.25 * mm});
            skCircle(sketch, "E18.52.18.0", {"center": v(68.02, 47.46) * mm, "radius": 0.25 * mm});
            skCircle(sketch, "E18.0.19.0", {"center": v(1.98, 50) * mm, "radius": 0.25 * mm});
            skCircle(sketch, "E18.2.19.0", {"center": v(4.52, 50) * mm, "radius": 0.25 * mm});
            skCircle(sketch, "E18.4.19.0", {"center": v(7.06, 50) * mm, "radius": 0.25 * mm});
            skCircle(sketch, "E18.6.19.0", {"center": v(9.6, 50) * mm, "radius": 0.25 * mm});
            skCircle(sketch, "E18.8.19.0", {"center": v(12.14, 50) * mm, "radius": 0.25 * mm});
            skCircle(sketch, "E18.10.19.0", {"center": v(14.68, 50) * mm, "radius": 0.25 * mm});
            skCircle(sketch, "E18.12.19.0", {"center": v(17.22, 50) * mm, "radius": 0.25 * mm});
            skCircle(sketch, "E18.14.19.0", {"center": v(19.76, 50) * mm, "radius": 0.25 * mm});
            skCircle(sketch, "E18.16.19.0", {"center": v(22.3, 50) * mm, "radius": 0.25 * mm});
            skCircle(sketch, "E18.18.19.0", {"center": v(24.84, 50) * mm, "radius": 0.25 * mm});
            skCircle(sketch, "E18.20.19.0", {"center": v(27.38, 50) * mm, "radius": 0.25 * mm});
            skCircle(sketch, "E18.22.19.0", {"center": v(29.92, 50) * mm, "radius": 0.25 * mm});
            skCircle(sketch, "E18.24.19.0", {"center": v(32.46, 50) * mm, "radius": 0.25 * mm});
            skCircle(sketch, "E18.26.19.0", {"center": v(35, 50) * mm, "radius": 0.25 * mm});
            skCircle(sketch, "E18.28.19.0", {"center": v(37.54, 50) * mm, "radius": 0.25 * mm});
            skCircle(sketch, "E18.30.19.0", {"center": v(40.08, 50) * mm, "radius": 0.25 * mm});
            skCircle(sketch, "E18.32.19.0", {"center": v(42.62, 50) * mm, "radius": 0.25 * mm});
            skCircle(sketch, "E18.34.19.0", {"center": v(45.16, 50) * mm, "radius": 0.25 * mm});
            skCircle(sketch, "E18.36.19.0", {"center": v(47.7, 50) * mm, "radius": 0.25 * mm});
            skCircle(sketch, "E18.38.19.0", {"center": v(50.24, 50) * mm, "radius": 0.25 * mm});
            skCircle(sketch, "E18.40.19.0", {"center": v(52.78, 50) * mm, "radius": 0.25 * mm});
            skCircle(sketch, "E18.42.19.0", {"center": v(55.32, 50) * mm, "radius": 0.25 * mm});
            skCircle(sketch, "E18.44.19.0", {"center": v(57.86, 50) * mm, "radius": 0.25 * mm});
            skCircle(sketch, "E18.46.19.0", {"center": v(60.4, 50) * mm, "radius": 0.25 * mm});
            skCircle(sketch, "E18.48.19.0", {"center": v(62.94, 50) * mm, "radius": 0.25 * mm});
            skCircle(sketch, "E18.50.19.0", {"center": v(65.48, 50) * mm, "radius": 0.25 * mm});
            skCircle(sketch, "E18.52.19.0", {"center": v(68.02, 50) * mm, "radius": 0.25 * mm});
            skCircle(sketch, "E18.0.20.0", {"center": v(1.98, 52.54) * mm, "radius": 0.25 * mm});
            skCircle(sketch, "E18.2.20.0", {"center": v(4.52, 52.54) * mm, "radius": 0.25 * mm});
            skCircle(sketch, "E18.4.20.0", {"center": v(7.06, 52.54) * mm, "radius": 0.25 * mm});
            skCircle(sketch, "E18.6.20.0", {"center": v(9.6, 52.54) * mm, "radius": 0.25 * mm});
            skCircle(sketch, "E18.8.20.0", {"center": v(12.14, 52.54) * mm, "radius": 0.25 * mm});
            skCircle(sketch, "E18.10.20.0", {"center": v(14.68, 52.54) * mm, "radius": 0.25 * mm});
            skCircle(sketch, "E18.12.20.0", {"center": v(17.22, 52.54) * mm, "radius": 0.25 * mm});
            skCircle(sketch, "E18.14.20.0", {"center": v(19.76, 52.54) * mm, "radius": 0.25 * mm});
            skCircle(sketch, "E18.16.20.0", {"center": v(22.3, 52.54) * mm, "radius": 0.25 * mm});
            skCircle(sketch, "E18.18.20.0", {"center": v(24.84, 52.54) * mm, "radius": 0.25 * mm});
            skCircle(sketch, "E18.20.20.0", {"center": v(27.38, 52.54) * mm, "radius": 0.25 * mm});
            skCircle(sketch, "E18.22.20.0", {"center": v(29.92, 52.54) * mm, "radius": 0.25 * mm});
            skCircle(sketch, "E18.24.20.0", {"center": v(32.46, 52.54) * mm, "radius": 0.25 * mm});
            skCircle(sketch, "E18.26.20.0", {"center": v(35, 52.54) * mm, "radius": 0.25 * mm});
            skCircle(sketch, "E18.28.20.0", {"center": v(37.54, 52.54) * mm, "radius": 0.25 * mm});
            skCircle(sketch, "E18.30.20.0", {"center": v(40.08, 52.54) * mm, "radius": 0.25 * mm});
            skCircle(sketch, "E18.32.20.0", {"center": v(42.62, 52.54) * mm, "radius": 0.25 * mm});
            skCircle(sketch, "E18.34.20.0", {"center": v(45.16, 52.54) * mm, "radius": 0.25 * mm});
            skCircle(sketch, "E18.36.20.0", {"center": v(47.7, 52.54) * mm, "radius": 0.25 * mm});
            skCircle(sketch, "E18.38.20.0", {"center": v(50.24, 52.54) * mm, "radius": 0.25 * mm});
            skCircle(sketch, "E18.40.20.0", {"center": v(52.78, 52.54) * mm, "radius": 0.25 * mm});
            skCircle(sketch, "E18.42.20.0", {"center": v(55.32, 52.54) * mm, "radius": 0.25 * mm});
            skCircle(sketch, "E18.44.20.0", {"center": v(57.86, 52.54) * mm, "radius": 0.25 * mm});
            skCircle(sketch, "E18.46.20.0", {"center": v(60.4, 52.54) * mm, "radius": 0.25 * mm});
            skCircle(sketch, "E18.48.20.0", {"center": v(62.94, 52.54) * mm, "radius": 0.25 * mm});
            skCircle(sketch, "E18.50.20.0", {"center": v(65.48, 52.54) * mm, "radius": 0.25 * mm});
            skCircle(sketch, "E18.52.20.0", {"center": v(68.02, 52.54) * mm, "radius": 0.25 * mm});
            skCircle(sketch, "E18.0.21.0", {"center": v(1.98, 55.08) * mm, "radius": 0.25 * mm});
            skCircle(sketch, "E18.2.21.0", {"center": v(4.52, 55.08) * mm, "radius": 0.25 * mm});
            skCircle(sketch, "E18.4.21.0", {"center": v(7.06, 55.08) * mm, "radius": 0.25 * mm});
            skCircle(sketch, "E18.6.21.0", {"center": v(9.6, 55.08) * mm, "radius": 0.25 * mm});
            skCircle(sketch, "E18.8.21.0", {"center": v(12.14, 55.08) * mm, "radius": 0.25 * mm});
            skCircle(sketch, "E18.10.21.0", {"center": v(14.68, 55.08) * mm, "radius": 0.25 * mm});
            skCircle(sketch, "E18.12.21.0", {"center": v(17.22, 55.08) * mm, "radius": 0.25 * mm});
            skCircle(sketch, "E18.14.21.0", {"center": v(19.76, 55.08) * mm, "radius": 0.25 * mm});
            skCircle(sketch, "E18.16.21.0", {"center": v(22.3, 55.08) * mm, "radius": 0.25 * mm});
            skCircle(sketch, "E18.18.21.0", {"center": v(24.84, 55.08) * mm, "radius": 0.25 * mm});
            skCircle(sketch, "E18.20.21.0", {"center": v(27.38, 55.08) * mm, "radius": 0.25 * mm});
            skCircle(sketch, "E18.22.21.0", {"center": v(29.92, 55.08) * mm, "radius": 0.25 * mm});
            skCircle(sketch, "E18.24.21.0", {"center": v(32.46, 55.08) * mm, "radius": 0.25 * mm});
            skCircle(sketch, "E18.26.21.0", {"center": v(35, 55.08) * mm, "radius": 0.25 * mm});
            skCircle(sketch, "E18.28.21.0", {"center": v(37.54, 55.08) * mm, "radius": 0.25 * mm});
            skCircle(sketch, "E18.30.21.0", {"center": v(40.08, 55.08) * mm, "radius": 0.25 * mm});
            skCircle(sketch, "E18.32.21.0", {"center": v(42.62, 55.08) * mm, "radius": 0.25 * mm});
            skCircle(sketch, "E18.34.21.0", {"center": v(45.16, 55.08) * mm, "radius": 0.25 * mm});
            skCircle(sketch, "E18.36.21.0", {"center": v(47.7, 55.08) * mm, "radius": 0.25 * mm});
            skCircle(sketch, "E18.38.21.0", {"center": v(50.24, 55.08) * mm, "radius": 0.25 * mm});
            skCircle(sketch, "E18.40.21.0", {"center": v(52.78, 55.08) * mm, "radius": 0.25 * mm});
            skCircle(sketch, "E18.42.21.0", {"center": v(55.32, 55.08) * mm, "radius": 0.25 * mm});
            skCircle(sketch, "E18.44.21.0", {"center": v(57.86, 55.08) * mm, "radius": 0.25 * mm});
            skCircle(sketch, "E18.46.21.0", {"center": v(60.4, 55.08) * mm, "radius": 0.25 * mm});
            skCircle(sketch, "E18.48.21.0", {"center": v(62.94, 55.08) * mm, "radius": 0.25 * mm});
            skCircle(sketch, "E18.50.21.0", {"center": v(65.48, 55.08) * mm, "radius": 0.25 * mm});
            skCircle(sketch, "E18.52.21.0", {"center": v(68.02, 55.08) * mm, "radius": 0.25 * mm});
            skCircle(sketch, "E18.0.22.0", {"center": v(1.98, 57.62) * mm, "radius": 0.25 * mm});
            skCircle(sketch, "E18.2.22.0", {"center": v(4.52, 57.62) * mm, "radius": 0.25 * mm});
            skCircle(sketch, "E18.4.22.0", {"center": v(7.06, 57.62) * mm, "radius": 0.25 * mm});
            skCircle(sketch, "E18.6.22.0", {"center": v(9.6, 57.62) * mm, "radius": 0.25 * mm});
            skCircle(sketch, "E18.8.22.0", {"center": v(12.14, 57.62) * mm, "radius": 0.25 * mm});
            skCircle(sketch, "E18.10.22.0", {"center": v(14.68, 57.62) * mm, "radius": 0.25 * mm});
            skCircle(sketch, "E18.12.22.0", {"center": v(17.22, 57.62) * mm, "radius": 0.25 * mm});
            skCircle(sketch, "E18.14.22.0", {"center": v(19.76, 57.62) * mm, "radius": 0.25 * mm});
            skCircle(sketch, "E18.16.22.0", {"center": v(22.3, 57.62) * mm, "radius": 0.25 * mm});
            skCircle(sketch, "E18.18.22.0", {"center": v(24.84, 57.62) * mm, "radius": 0.25 * mm});
            skCircle(sketch, "E18.20.22.0", {"center": v(27.38, 57.62) * mm, "radius": 0.25 * mm});
            skCircle(sketch, "E18.22.22.0", {"center": v(29.92, 57.62) * mm, "radius": 0.25 * mm});
            skCircle(sketch, "E18.24.22.0", {"center": v(32.46, 57.62) * mm, "radius": 0.25 * mm});
            skCircle(sketch, "E18.26.22.0", {"center": v(35, 57.62) * mm, "radius": 0.25 * mm});
            skCircle(sketch, "E18.28.22.0", {"center": v(37.54, 57.62) * mm, "radius": 0.25 * mm});
            skCircle(sketch, "E18.30.22.0", {"center": v(40.08, 57.62) * mm, "radius": 0.25 * mm});
            skCircle(sketch, "E18.32.22.0", {"center": v(42.62, 57.62) * mm, "radius": 0.25 * mm});
            skCircle(sketch, "E18.34.22.0", {"center": v(45.16, 57.62) * mm, "radius": 0.25 * mm});
            skCircle(sketch, "E18.36.22.0", {"center": v(47.7, 57.62) * mm, "radius": 0.25 * mm});
            skCircle(sketch, "E18.38.22.0", {"center": v(50.24, 57.62) * mm, "radius": 0.25 * mm});
            skCircle(sketch, "E18.40.22.0", {"center": v(52.78, 57.62) * mm, "radius": 0.25 * mm});
            skCircle(sketch, "E18.42.22.0", {"center": v(55.32, 57.62) * mm, "radius": 0.25 * mm});
            skCircle(sketch, "E18.44.22.0", {"center": v(57.86, 57.62) * mm, "radius": 0.25 * mm});
            skCircle(sketch, "E18.46.22.0", {"center": v(60.4, 57.62) * mm, "radius": 0.25 * mm});
            skCircle(sketch, "E18.48.22.0", {"center": v(62.94, 57.62) * mm, "radius": 0.25 * mm});
            skCircle(sketch, "E18.50.22.0", {"center": v(65.48, 57.62) * mm, "radius": 0.25 * mm});
            skCircle(sketch, "E18.52.22.0", {"center": v(68.02, 57.62) * mm, "radius": 0.25 * mm});
            skCircle(sketch, "E18.0.23.0", {"center": v(1.98, 60.16) * mm, "radius": 0.25 * mm});
            skCircle(sketch, "E18.2.23.0", {"center": v(4.52, 60.16) * mm, "radius": 0.25 * mm});
            skCircle(sketch, "E18.4.23.0", {"center": v(7.06, 60.16) * mm, "radius": 0.25 * mm});
            skCircle(sketch, "E18.6.23.0", {"center": v(9.6, 60.16) * mm, "radius": 0.25 * mm});
            skCircle(sketch, "E18.8.23.0", {"center": v(12.14, 60.16) * mm, "radius": 0.25 * mm});
            skCircle(sketch, "E18.10.23.0", {"center": v(14.68, 60.16) * mm, "radius": 0.25 * mm});
            skCircle(sketch, "E18.12.23.0", {"center": v(17.22, 60.16) * mm, "radius": 0.25 * mm});
            skCircle(sketch, "E18.14.23.0", {"center": v(19.76, 60.16) * mm, "radius": 0.25 * mm});
            skCircle(sketch, "E18.16.23.0", {"center": v(22.3, 60.16) * mm, "radius": 0.25 * mm});
            skCircle(sketch, "E18.18.23.0", {"center": v(24.84, 60.16) * mm, "radius": 0.25 * mm});
            skCircle(sketch, "E18.20.23.0", {"center": v(27.38, 60.16) * mm, "radius": 0.25 * mm});
            skCircle(sketch, "E18.22.23.0", {"center": v(29.92, 60.16) * mm, "radius": 0.25 * mm});
            skCircle(sketch, "E18.24.23.0", {"center": v(32.46, 60.16) * mm, "radius": 0.25 * mm});
            skCircle(sketch, "E18.26.23.0", {"center": v(35, 60.16) * mm, "radius": 0.25 * mm});
            skCircle(sketch, "E18.28.23.0", {"center": v(37.54, 60.16) * mm, "radius": 0.25 * mm});
            skCircle(sketch, "E18.30.23.0", {"center": v(40.08, 60.16) * mm, "radius": 0.25 * mm});
            skCircle(sketch, "E18.32.23.0", {"center": v(42.62, 60.16) * mm, "radius": 0.25 * mm});
            skCircle(sketch, "E18.34.23.0", {"center": v(45.16, 60.16) * mm, "radius": 0.25 * mm});
            skCircle(sketch, "E18.36.23.0", {"center": v(47.7, 60.16) * mm, "radius": 0.25 * mm});
            skCircle(sketch, "E18.38.23.0", {"center": v(50.24, 60.16) * mm, "radius": 0.25 * mm});
            skCircle(sketch, "E18.40.23.0", {"center": v(52.78, 60.16) * mm, "radius": 0.25 * mm});
            skCircle(sketch, "E18.42.23.0", {"center": v(55.32, 60.16) * mm, "radius": 0.25 * mm});
            skCircle(sketch, "E18.44.23.0", {"center": v(57.86, 60.16) * mm, "radius": 0.25 * mm});
            skCircle(sketch, "E18.46.23.0", {"center": v(60.4, 60.16) * mm, "radius": 0.25 * mm});
            skCircle(sketch, "E18.48.23.0", {"center": v(62.94, 60.16) * mm, "radius": 0.25 * mm});
            skCircle(sketch, "E18.50.23.0", {"center": v(65.48, 60.16) * mm, "radius": 0.25 * mm});
            skCircle(sketch, "E18.52.23.0", {"center": v(68.02, 60.16) * mm, "radius": 0.25 * mm});
            skCircle(sketch, "E18.0.24.0", {"center": v(1.98, 62.7) * mm, "radius": 0.25 * mm});
            skCircle(sketch, "E18.2.24.0", {"center": v(4.52, 62.7) * mm, "radius": 0.25 * mm});
            skCircle(sketch, "E18.4.24.0", {"center": v(7.06, 62.7) * mm, "radius": 0.25 * mm});
            skCircle(sketch, "E18.6.24.0", {"center": v(9.6, 62.7) * mm, "radius": 0.25 * mm});
            skCircle(sketch, "E18.8.24.0", {"center": v(12.14, 62.7) * mm, "radius": 0.25 * mm});
            skCircle(sketch, "E18.10.24.0", {"center": v(14.68, 62.7) * mm, "radius": 0.25 * mm});
            skCircle(sketch, "E18.12.24.0", {"center": v(17.22, 62.7) * mm, "radius": 0.25 * mm});
            skCircle(sketch, "E18.14.24.0", {"center": v(19.76, 62.7) * mm, "radius": 0.25 * mm});
            skCircle(sketch, "E18.16.24.0", {"center": v(22.3, 62.7) * mm, "radius": 0.25 * mm});
            skCircle(sketch, "E18.18.24.0", {"center": v(24.84, 62.7) * mm, "radius": 0.25 * mm});
            skCircle(sketch, "E18.20.24.0", {"center": v(27.38, 62.7) * mm, "radius": 0.25 * mm});
            skCircle(sketch, "E18.22.24.0", {"center": v(29.92, 62.7) * mm, "radius": 0.25 * mm});
            skCircle(sketch, "E18.24.24.0", {"center": v(32.46, 62.7) * mm, "radius": 0.25 * mm});
            skCircle(sketch, "E18.26.24.0", {"center": v(35, 62.7) * mm, "radius": 0.25 * mm});
            skCircle(sketch, "E18.28.24.0", {"center": v(37.54, 62.7) * mm, "radius": 0.25 * mm});
            skCircle(sketch, "E18.30.24.0", {"center": v(40.08, 62.7) * mm, "radius": 0.25 * mm});
            skCircle(sketch, "E18.32.24.0", {"center": v(42.62, 62.7) * mm, "radius": 0.25 * mm});
            skCircle(sketch, "E18.34.24.0", {"center": v(45.16, 62.7) * mm, "radius": 0.25 * mm});
            skCircle(sketch, "E18.36.24.0", {"center": v(47.7, 62.7) * mm, "radius": 0.25 * mm});
            skCircle(sketch, "E18.38.24.0", {"center": v(50.24, 62.7) * mm, "radius": 0.25 * mm});
            skCircle(sketch, "E18.40.24.0", {"center": v(52.78, 62.7) * mm, "radius": 0.25 * mm});
            skCircle(sketch, "E18.42.24.0", {"center": v(55.32, 62.7) * mm, "radius": 0.25 * mm});
            skCircle(sketch, "E18.44.24.0", {"center": v(57.86, 62.7) * mm, "radius": 0.25 * mm});
            skCircle(sketch, "E18.46.24.0", {"center": v(60.4, 62.7) * mm, "radius": 0.25 * mm});
            skCircle(sketch, "E18.48.24.0", {"center": v(62.94, 62.7) * mm, "radius": 0.25 * mm});
            skCircle(sketch, "E18.50.24.0", {"center": v(65.48, 62.7) * mm, "radius": 0.25 * mm});
            skCircle(sketch, "E18.52.24.0", {"center": v(68.02, 62.7) * mm, "radius": 0.25 * mm});
            skCircle(sketch, "E18.0.25.0", {"center": v(1.98, 65.24) * mm, "radius": 0.25 * mm});
            skCircle(sketch, "E18.2.25.0", {"center": v(4.52, 65.24) * mm, "radius": 0.25 * mm});
            skCircle(sketch, "E18.4.25.0", {"center": v(7.06, 65.24) * mm, "radius": 0.25 * mm});
            skCircle(sketch, "E18.6.25.0", {"center": v(9.6, 65.24) * mm, "radius": 0.25 * mm});
            skCircle(sketch, "E18.8.25.0", {"center": v(12.14, 65.24) * mm, "radius": 0.25 * mm});
            skCircle(sketch, "E18.10.25.0", {"center": v(14.68, 65.24) * mm, "radius": 0.25 * mm});
            skCircle(sketch, "E18.12.25.0", {"center": v(17.22, 65.24) * mm, "radius": 0.25 * mm});
            skCircle(sketch, "E18.14.25.0", {"center": v(19.76, 65.24) * mm, "radius": 0.25 * mm});
            skCircle(sketch, "E18.16.25.0", {"center": v(22.3, 65.24) * mm, "radius": 0.25 * mm});
            skCircle(sketch, "E18.18.25.0", {"center": v(24.84, 65.24) * mm, "radius": 0.25 * mm});
            skCircle(sketch, "E18.20.25.0", {"center": v(27.38, 65.24) * mm, "radius": 0.25 * mm});
            skCircle(sketch, "E18.22.25.0", {"center": v(29.92, 65.24) * mm, "radius": 0.25 * mm});
            skCircle(sketch, "E18.24.25.0", {"center": v(32.46, 65.24) * mm, "radius": 0.25 * mm});
            skCircle(sketch, "E18.26.25.0", {"center": v(35, 65.24) * mm, "radius": 0.25 * mm});
            skCircle(sketch, "E18.28.25.0", {"center": v(37.54, 65.24) * mm, "radius": 0.25 * mm});
            skCircle(sketch, "E18.30.25.0", {"center": v(40.08, 65.24) * mm, "radius": 0.25 * mm});
            skCircle(sketch, "E18.32.25.0", {"center": v(42.62, 65.24) * mm, "radius": 0.25 * mm});
            skCircle(sketch, "E18.34.25.0", {"center": v(45.16, 65.24) * mm, "radius": 0.25 * mm});
            skCircle(sketch, "E18.36.25.0", {"center": v(47.7, 65.24) * mm, "radius": 0.25 * mm});
            skCircle(sketch, "E18.38.25.0", {"center": v(50.24, 65.24) * mm, "radius": 0.25 * mm});
            skCircle(sketch, "E18.40.25.0", {"center": v(52.78, 65.24) * mm, "radius": 0.25 * mm});
            skCircle(sketch, "E18.42.25.0", {"center": v(55.32, 65.24) * mm, "radius": 0.25 * mm});
            skCircle(sketch, "E18.44.25.0", {"center": v(57.86, 65.24) * mm, "radius": 0.25 * mm});
            skCircle(sketch, "E18.46.25.0", {"center": v(60.4, 65.24) * mm, "radius": 0.25 * mm});
            skCircle(sketch, "E18.48.25.0", {"center": v(62.94, 65.24) * mm, "radius": 0.25 * mm});
            skCircle(sketch, "E18.50.25.0", {"center": v(65.48, 65.24) * mm, "radius": 0.25 * mm});
            skCircle(sketch, "E18.52.25.0", {"center": v(68.02, 65.24) * mm, "radius": 0.25 * mm});
            skCircle(sketch, "E18.0.26.0", {"center": v(1.98, 67.78) * mm, "radius": 0.25 * mm});
            skCircle(sketch, "E18.2.26.0", {"center": v(4.52, 67.78) * mm, "radius": 0.25 * mm});
            skCircle(sketch, "E18.4.26.0", {"center": v(7.06, 67.78) * mm, "radius": 0.25 * mm});
            skCircle(sketch, "E18.6.26.0", {"center": v(9.6, 67.78) * mm, "radius": 0.25 * mm});
            skCircle(sketch, "E18.8.26.0", {"center": v(12.14, 67.78) * mm, "radius": 0.25 * mm});
            skCircle(sketch, "E18.10.26.0", {"center": v(14.68, 67.78) * mm, "radius": 0.25 * mm});
            skCircle(sketch, "E18.12.26.0", {"center": v(17.22, 67.78) * mm, "radius": 0.25 * mm});
            skCircle(sketch, "E18.14.26.0", {"center": v(19.76, 67.78) * mm, "radius": 0.25 * mm});
            skCircle(sketch, "E18.16.26.0", {"center": v(22.3, 67.78) * mm, "radius": 0.25 * mm});
            skCircle(sketch, "E18.18.26.0", {"center": v(24.84, 67.78) * mm, "radius": 0.25 * mm});
            skCircle(sketch, "E18.20.26.0", {"center": v(27.38, 67.78) * mm, "radius": 0.25 * mm});
            skCircle(sketch, "E18.22.26.0", {"center": v(29.92, 67.78) * mm, "radius": 0.25 * mm});
            skCircle(sketch, "E18.24.26.0", {"center": v(32.46, 67.78) * mm, "radius": 0.25 * mm});
            skCircle(sketch, "E18.26.26.0", {"center": v(35, 67.78) * mm, "radius": 0.25 * mm});
            skCircle(sketch, "E18.28.26.0", {"center": v(37.54, 67.78) * mm, "radius": 0.25 * mm});
            skCircle(sketch, "E18.30.26.0", {"center": v(40.08, 67.78) * mm, "radius": 0.25 * mm});
            skCircle(sketch, "E18.32.26.0", {"center": v(42.62, 67.78) * mm, "radius": 0.25 * mm});
            skCircle(sketch, "E18.34.26.0", {"center": v(45.16, 67.78) * mm, "radius": 0.25 * mm});
            skCircle(sketch, "E18.36.26.0", {"center": v(47.7, 67.78) * mm, "radius": 0.25 * mm});
            skCircle(sketch, "E18.38.26.0", {"center": v(50.24, 67.78) * mm, "radius": 0.25 * mm});
            skCircle(sketch, "E18.40.26.0", {"center": v(52.78, 67.78) * mm, "radius": 0.25 * mm});
            skCircle(sketch, "E18.42.26.0", {"center": v(55.32, 67.78) * mm, "radius": 0.25 * mm});
            skCircle(sketch, "E18.44.26.0", {"center": v(57.86, 67.78) * mm, "radius": 0.25 * mm});
            skCircle(sketch, "E18.46.26.0", {"center": v(60.4, 67.78) * mm, "radius": 0.25 * mm});
            skCircle(sketch, "E18.48.26.0", {"center": v(62.94, 67.78) * mm, "radius": 0.25 * mm});
            skCircle(sketch, "E18.50.26.0", {"center": v(65.48, 67.78) * mm, "radius": 0.25 * mm});
            skCircle(sketch, "E18.52.26.0", {"center": v(68.02, 67.78) * mm, "radius": 0.25 * mm});
            skCircle(sketch, "E18.0.27.0", {"center": v(1.98, 70.32) * mm, "radius": 0.25 * mm});
            skCircle(sketch, "E18.2.27.0", {"center": v(4.52, 70.32) * mm, "radius": 0.25 * mm});
            skCircle(sketch, "E18.4.27.0", {"center": v(7.06, 70.32) * mm, "radius": 0.25 * mm});
            skCircle(sketch, "E18.6.27.0", {"center": v(9.6, 70.32) * mm, "radius": 0.25 * mm});
            skCircle(sketch, "E18.8.27.0", {"center": v(12.14, 70.32) * mm, "radius": 0.25 * mm});
            skCircle(sketch, "E18.10.27.0", {"center": v(14.68, 70.32) * mm, "radius": 0.25 * mm});
            skCircle(sketch, "E18.12.27.0", {"center": v(17.22, 70.32) * mm, "radius": 0.25 * mm});
            skCircle(sketch, "E18.14.27.0", {"center": v(19.76, 70.32) * mm, "radius": 0.25 * mm});
            skCircle(sketch, "E18.16.27.0", {"center": v(22.3, 70.32) * mm, "radius": 0.25 * mm});
            skCircle(sketch, "E18.18.27.0", {"center": v(24.84, 70.32) * mm, "radius": 0.25 * mm});
            skCircle(sketch, "E18.20.27.0", {"center": v(27.38, 70.32) * mm, "radius": 0.25 * mm});
            skCircle(sketch, "E18.22.27.0", {"center": v(29.92, 70.32) * mm, "radius": 0.25 * mm});
            skCircle(sketch, "E18.24.27.0", {"center": v(32.46, 70.32) * mm, "radius": 0.25 * mm});
            skCircle(sketch, "E18.26.27.0", {"center": v(35, 70.32) * mm, "radius": 0.25 * mm});
            skCircle(sketch, "E18.28.27.0", {"center": v(37.54, 70.32) * mm, "radius": 0.25 * mm});
            skCircle(sketch, "E18.30.27.0", {"center": v(40.08, 70.32) * mm, "radius": 0.25 * mm});
            skCircle(sketch, "E18.32.27.0", {"center": v(42.62, 70.32) * mm, "radius": 0.25 * mm});
            skCircle(sketch, "E18.34.27.0", {"center": v(45.16, 70.32) * mm, "radius": 0.25 * mm});
            skCircle(sketch, "E18.36.27.0", {"center": v(47.7, 70.32) * mm, "radius": 0.25 * mm});
            skCircle(sketch, "E18.38.27.0", {"center": v(50.24, 70.32) * mm, "radius": 0.25 * mm});
            skCircle(sketch, "E18.40.27.0", {"center": v(52.78, 70.32) * mm, "radius": 0.25 * mm});
            skCircle(sketch, "E18.42.27.0", {"center": v(55.32, 70.32) * mm, "radius": 0.25 * mm});
            skCircle(sketch, "E18.44.27.0", {"center": v(57.86, 70.32) * mm, "radius": 0.25 * mm});
            skCircle(sketch, "E18.46.27.0", {"center": v(60.4, 70.32) * mm, "radius": 0.25 * mm});
            skCircle(sketch, "E18.48.27.0", {"center": v(62.94, 70.32) * mm, "radius": 0.25 * mm});
            skCircle(sketch, "E18.50.27.0", {"center": v(65.48, 70.32) * mm, "radius": 0.25 * mm});
            skCircle(sketch, "E18.52.27.0", {"center": v(68.02, 70.32) * mm, "radius": 0.25 * mm});
            skCircle(sketch, "E18.0.28.0", {"center": v(1.98, 72.86) * mm, "radius": 0.25 * mm});
            skCircle(sketch, "E18.2.28.0", {"center": v(4.52, 72.86) * mm, "radius": 0.25 * mm});
            skCircle(sketch, "E18.4.28.0", {"center": v(7.06, 72.86) * mm, "radius": 0.25 * mm});
            skCircle(sketch, "E18.6.28.0", {"center": v(9.6, 72.86) * mm, "radius": 0.25 * mm});
            skCircle(sketch, "E18.8.28.0", {"center": v(12.14, 72.86) * mm, "radius": 0.25 * mm});
            skCircle(sketch, "E18.10.28.0", {"center": v(14.68, 72.86) * mm, "radius": 0.25 * mm});
            skCircle(sketch, "E18.12.28.0", {"center": v(17.22, 72.86) * mm, "radius": 0.25 * mm});
            skCircle(sketch, "E18.14.28.0", {"center": v(19.76, 72.86) * mm, "radius": 0.25 * mm});
            skCircle(sketch, "E18.16.28.0", {"center": v(22.3, 72.86) * mm, "radius": 0.25 * mm});
            skCircle(sketch, "E18.18.28.0", {"center": v(24.84, 72.86) * mm, "radius": 0.25 * mm});
            skCircle(sketch, "E18.20.28.0", {"center": v(27.38, 72.86) * mm, "radius": 0.25 * mm});
            skCircle(sketch, "E18.22.28.0", {"center": v(29.92, 72.86) * mm, "radius": 0.25 * mm});
            skCircle(sketch, "E18.24.28.0", {"center": v(32.46, 72.86) * mm, "radius": 0.25 * mm});
            skCircle(sketch, "E18.26.28.0", {"center": v(35, 72.86) * mm, "radius": 0.25 * mm});
            skCircle(sketch, "E18.28.28.0", {"center": v(37.54, 72.86) * mm, "radius": 0.25 * mm});
            skCircle(sketch, "E18.30.28.0", {"center": v(40.08, 72.86) * mm, "radius": 0.25 * mm});
            skCircle(sketch, "E18.32.28.0", {"center": v(42.62, 72.86) * mm, "radius": 0.25 * mm});
            skCircle(sketch, "E18.34.28.0", {"center": v(45.16, 72.86) * mm, "radius": 0.25 * mm});
            skCircle(sketch, "E18.36.28.0", {"center": v(47.7, 72.86) * mm, "radius": 0.25 * mm});
            skCircle(sketch, "E18.38.28.0", {"center": v(50.24, 72.86) * mm, "radius": 0.25 * mm});
            skCircle(sketch, "E18.40.28.0", {"center": v(52.78, 72.86) * mm, "radius": 0.25 * mm});
            skCircle(sketch, "E18.42.28.0", {"center": v(55.32, 72.86) * mm, "radius": 0.25 * mm});
            skCircle(sketch, "E18.44.28.0", {"center": v(57.86, 72.86) * mm, "radius": 0.25 * mm});
            skCircle(sketch, "E18.46.28.0", {"center": v(60.4, 72.86) * mm, "radius": 0.25 * mm});
            skCircle(sketch, "E18.48.28.0", {"center": v(62.94, 72.86) * mm, "radius": 0.25 * mm});
            skCircle(sketch, "E18.50.28.0", {"center": v(65.48, 72.86) * mm, "radius": 0.25 * mm});
            skCircle(sketch, "E18.52.28.0", {"center": v(68.02, 72.86) * mm, "radius": 0.25 * mm});
            skCircle(sketch, "E18.0.29.0", {"center": v(1.98, 75.4) * mm, "radius": 0.25 * mm});
            skCircle(sketch, "E18.2.29.0", {"center": v(4.52, 75.4) * mm, "radius": 0.25 * mm});
            skCircle(sketch, "E18.4.29.0", {"center": v(7.06, 75.4) * mm, "radius": 0.25 * mm});
            skCircle(sketch, "E18.6.29.0", {"center": v(9.6, 75.4) * mm, "radius": 0.25 * mm});
            skCircle(sketch, "E18.8.29.0", {"center": v(12.14, 75.4) * mm, "radius": 0.25 * mm});
            skCircle(sketch, "E18.10.29.0", {"center": v(14.68, 75.4) * mm, "radius": 0.25 * mm});
            skCircle(sketch, "E18.12.29.0", {"center": v(17.22, 75.4) * mm, "radius": 0.25 * mm});
            skCircle(sketch, "E18.14.29.0", {"center": v(19.76, 75.4) * mm, "radius": 0.25 * mm});
            skCircle(sketch, "E18.16.29.0", {"center": v(22.3, 75.4) * mm, "radius": 0.25 * mm});
            skCircle(sketch, "E18.18.29.0", {"center": v(24.84, 75.4) * mm, "radius": 0.25 * mm});
            skCircle(sketch, "E18.20.29.0", {"center": v(27.38, 75.4) * mm, "radius": 0.25 * mm});
            skCircle(sketch, "E18.22.29.0", {"center": v(29.92, 75.4) * mm, "radius": 0.25 * mm});
            skCircle(sketch, "E18.24.29.0", {"center": v(32.46, 75.4) * mm, "radius": 0.25 * mm});
            skCircle(sketch, "E18.26.29.0", {"center": v(35, 75.4) * mm, "radius": 0.25 * mm});
            skCircle(sketch, "E18.28.29.0", {"center": v(37.54, 75.4) * mm, "radius": 0.25 * mm});
            skCircle(sketch, "E18.30.29.0", {"center": v(40.08, 75.4) * mm, "radius": 0.25 * mm});
            skCircle(sketch, "E18.32.29.0", {"center": v(42.62, 75.4) * mm, "radius": 0.25 * mm});
            skCircle(sketch, "E18.34.29.0", {"center": v(45.16, 75.4) * mm, "radius": 0.25 * mm});
            skCircle(sketch, "E18.36.29.0", {"center": v(47.7, 75.4) * mm, "radius": 0.25 * mm});
            skCircle(sketch, "E18.38.29.0", {"center": v(50.24, 75.4) * mm, "radius": 0.25 * mm});
            skCircle(sketch, "E18.40.29.0", {"center": v(52.78, 75.4) * mm, "radius": 0.25 * mm});
            skCircle(sketch, "E18.42.29.0", {"center": v(55.32, 75.4) * mm, "radius": 0.25 * mm});
            skCircle(sketch, "E18.44.29.0", {"center": v(57.86, 75.4) * mm, "radius": 0.25 * mm});
            skCircle(sketch, "E18.46.29.0", {"center": v(60.4, 75.4) * mm, "radius": 0.25 * mm});
            skCircle(sketch, "E18.48.29.0", {"center": v(62.94, 75.4) * mm, "radius": 0.25 * mm});
            skCircle(sketch, "E18.50.29.0", {"center": v(65.48, 75.4) * mm, "radius": 0.25 * mm});
            skCircle(sketch, "E18.52.29.0", {"center": v(68.02, 75.4) * mm, "radius": 0.25 * mm});
            skCircle(sketch, "E18.0.30.0", {"center": v(1.98, 77.94) * mm, "radius": 0.25 * mm});
            skCircle(sketch, "E18.2.30.0", {"center": v(4.52, 77.94) * mm, "radius": 0.25 * mm});
            skCircle(sketch, "E18.4.30.0", {"center": v(7.06, 77.94) * mm, "radius": 0.25 * mm});
            skCircle(sketch, "E18.6.30.0", {"center": v(9.6, 77.94) * mm, "radius": 0.25 * mm});
            skCircle(sketch, "E18.8.30.0", {"center": v(12.14, 77.94) * mm, "radius": 0.25 * mm});
            skCircle(sketch, "E18.10.30.0", {"center": v(14.68, 77.94) * mm, "radius": 0.25 * mm});
            skCircle(sketch, "E18.12.30.0", {"center": v(17.22, 77.94) * mm, "radius": 0.25 * mm});
            skCircle(sketch, "E18.14.30.0", {"center": v(19.76, 77.94) * mm, "radius": 0.25 * mm});
            skCircle(sketch, "E18.16.30.0", {"center": v(22.3, 77.94) * mm, "radius": 0.25 * mm});
            skCircle(sketch, "E18.18.30.0", {"center": v(24.84, 77.94) * mm, "radius": 0.25 * mm});
            skCircle(sketch, "E18.20.30.0", {"center": v(27.38, 77.94) * mm, "radius": 0.25 * mm});
            skCircle(sketch, "E18.22.30.0", {"center": v(29.92, 77.94) * mm, "radius": 0.25 * mm});
            skCircle(sketch, "E18.24.30.0", {"center": v(32.46, 77.94) * mm, "radius": 0.25 * mm});
            skCircle(sketch, "E18.26.30.0", {"center": v(35, 77.94) * mm, "radius": 0.25 * mm});
            skCircle(sketch, "E18.28.30.0", {"center": v(37.54, 77.94) * mm, "radius": 0.25 * mm});
            skCircle(sketch, "E18.30.30.0", {"center": v(40.08, 77.94) * mm, "radius": 0.25 * mm});
            skCircle(sketch, "E18.32.30.0", {"center": v(42.62, 77.94) * mm, "radius": 0.25 * mm});
            skCircle(sketch, "E18.34.30.0", {"center": v(45.16, 77.94) * mm, "radius": 0.25 * mm});
            skCircle(sketch, "E18.36.30.0", {"center": v(47.7, 77.94) * mm, "radius": 0.25 * mm});
            skCircle(sketch, "E18.38.30.0", {"center": v(50.24, 77.94) * mm, "radius": 0.25 * mm});
            skCircle(sketch, "E18.40.30.0", {"center": v(52.78, 77.94) * mm, "radius": 0.25 * mm});
            skCircle(sketch, "E18.42.30.0", {"center": v(55.32, 77.94) * mm, "radius": 0.25 * mm});
            skCircle(sketch, "E18.44.30.0", {"center": v(57.86, 77.94) * mm, "radius": 0.25 * mm});
            skCircle(sketch, "E18.46.30.0", {"center": v(60.4, 77.94) * mm, "radius": 0.25 * mm});
            skCircle(sketch, "E18.48.30.0", {"center": v(62.94, 77.94) * mm, "radius": 0.25 * mm});
            skCircle(sketch, "E18.50.30.0", {"center": v(65.48, 77.94) * mm, "radius": 0.25 * mm});
            skCircle(sketch, "E18.52.30.0", {"center": v(68.02, 77.94) * mm, "radius": 0.25 * mm});
            skCircle(sketch, "E18.0.31.0", {"center": v(1.98, 80.48) * mm, "radius": 0.25 * mm});
            skCircle(sketch, "E18.2.31.0", {"center": v(4.52, 80.48) * mm, "radius": 0.25 * mm});
            skCircle(sketch, "E18.4.31.0", {"center": v(7.06, 80.48) * mm, "radius": 0.25 * mm});
            skCircle(sketch, "E18.6.31.0", {"center": v(9.6, 80.48) * mm, "radius": 0.25 * mm});
            skCircle(sketch, "E18.8.31.0", {"center": v(12.14, 80.48) * mm, "radius": 0.25 * mm});
            skCircle(sketch, "E18.10.31.0", {"center": v(14.68, 80.48) * mm, "radius": 0.25 * mm});
            skCircle(sketch, "E18.12.31.0", {"center": v(17.22, 80.48) * mm, "radius": 0.25 * mm});
            skCircle(sketch, "E18.14.31.0", {"center": v(19.76, 80.48) * mm, "radius": 0.25 * mm});
            skCircle(sketch, "E18.16.31.0", {"center": v(22.3, 80.48) * mm, "radius": 0.25 * mm});
            skCircle(sketch, "E18.18.31.0", {"center": v(24.84, 80.48) * mm, "radius": 0.25 * mm});
            skCircle(sketch, "E18.20.31.0", {"center": v(27.38, 80.48) * mm, "radius": 0.25 * mm});
            skCircle(sketch, "E18.22.31.0", {"center": v(29.92, 80.48) * mm, "radius": 0.25 * mm});
            skCircle(sketch, "E18.24.31.0", {"center": v(32.46, 80.48) * mm, "radius": 0.25 * mm});
            skCircle(sketch, "E18.26.31.0", {"center": v(35, 80.48) * mm, "radius": 0.25 * mm});
            skCircle(sketch, "E18.28.31.0", {"center": v(37.54, 80.48) * mm, "radius": 0.25 * mm});
            skCircle(sketch, "E18.30.31.0", {"center": v(40.08, 80.48) * mm, "radius": 0.25 * mm});
            skCircle(sketch, "E18.32.31.0", {"center": v(42.62, 80.48) * mm, "radius": 0.25 * mm});
            skCircle(sketch, "E18.34.31.0", {"center": v(45.16, 80.48) * mm, "radius": 0.25 * mm});
            skCircle(sketch, "E18.36.31.0", {"center": v(47.7, 80.48) * mm, "radius": 0.25 * mm});
            skCircle(sketch, "E18.38.31.0", {"center": v(50.24, 80.48) * mm, "radius": 0.25 * mm});
            skCircle(sketch, "E18.40.31.0", {"center": v(52.78, 80.48) * mm, "radius": 0.25 * mm});
            skCircle(sketch, "E18.42.31.0", {"center": v(55.32, 80.48) * mm, "radius": 0.25 * mm});
            skCircle(sketch, "E18.44.31.0", {"center": v(57.86, 80.48) * mm, "radius": 0.25 * mm});
            skCircle(sketch, "E18.46.31.0", {"center": v(60.4, 80.48) * mm, "radius": 0.25 * mm});
            skCircle(sketch, "E18.48.31.0", {"center": v(62.94, 80.48) * mm, "radius": 0.25 * mm});
            skCircle(sketch, "E18.50.31.0", {"center": v(65.48, 80.48) * mm, "radius": 0.25 * mm});
            skCircle(sketch, "E18.52.31.0", {"center": v(68.02, 80.48) * mm, "radius": 0.25 * mm});
            skCircle(sketch, "E18.0.32.0", {"center": v(1.98, 83.02) * mm, "radius": 0.25 * mm});
            skCircle(sketch, "E18.2.32.0", {"center": v(4.52, 83.02) * mm, "radius": 0.25 * mm});
            skCircle(sketch, "E18.4.32.0", {"center": v(7.06, 83.02) * mm, "radius": 0.25 * mm});
            skCircle(sketch, "E18.6.32.0", {"center": v(9.6, 83.02) * mm, "radius": 0.25 * mm});
            skCircle(sketch, "E18.8.32.0", {"center": v(12.14, 83.02) * mm, "radius": 0.25 * mm});
            skCircle(sketch, "E18.10.32.0", {"center": v(14.68, 83.02) * mm, "radius": 0.25 * mm});
            skCircle(sketch, "E18.12.32.0", {"center": v(17.22, 83.02) * mm, "radius": 0.25 * mm});
            skCircle(sketch, "E18.14.32.0", {"center": v(19.76, 83.02) * mm, "radius": 0.25 * mm});
            skCircle(sketch, "E18.16.32.0", {"center": v(22.3, 83.02) * mm, "radius": 0.25 * mm});
            skCircle(sketch, "E18.18.32.0", {"center": v(24.84, 83.02) * mm, "radius": 0.25 * mm});
            skCircle(sketch, "E18.20.32.0", {"center": v(27.38, 83.02) * mm, "radius": 0.25 * mm});
            skCircle(sketch, "E18.22.32.0", {"center": v(29.92, 83.02) * mm, "radius": 0.25 * mm});
            skCircle(sketch, "E18.24.32.0", {"center": v(32.46, 83.02) * mm, "radius": 0.25 * mm});
            skCircle(sketch, "E18.26.32.0", {"center": v(35, 83.02) * mm, "radius": 0.25 * mm});
            skCircle(sketch, "E18.28.32.0", {"center": v(37.54, 83.02) * mm, "radius": 0.25 * mm});
            skCircle(sketch, "E18.30.32.0", {"center": v(40.08, 83.02) * mm, "radius": 0.25 * mm});
            skCircle(sketch, "E18.32.32.0", {"center": v(42.62, 83.02) * mm, "radius": 0.25 * mm});
            skCircle(sketch, "E18.34.32.0", {"center": v(45.16, 83.02) * mm, "radius": 0.25 * mm});
            skCircle(sketch, "E18.36.32.0", {"center": v(47.7, 83.02) * mm, "radius": 0.25 * mm});
            skCircle(sketch, "E18.38.32.0", {"center": v(50.24, 83.02) * mm, "radius": 0.25 * mm});
            skCircle(sketch, "E18.40.32.0", {"center": v(52.78, 83.02) * mm, "radius": 0.25 * mm});
            skCircle(sketch, "E18.42.32.0", {"center": v(55.32, 83.02) * mm, "radius": 0.25 * mm});
            skCircle(sketch, "E18.44.32.0", {"center": v(57.86, 83.02) * mm, "radius": 0.25 * mm});
            skCircle(sketch, "E18.46.32.0", {"center": v(60.4, 83.02) * mm, "radius": 0.25 * mm});
            skCircle(sketch, "E18.48.32.0", {"center": v(62.94, 83.02) * mm, "radius": 0.25 * mm});
            skCircle(sketch, "E18.50.32.0", {"center": v(65.48, 83.02) * mm, "radius": 0.25 * mm});
            skCircle(sketch, "E18.52.32.0", {"center": v(68.02, 83.02) * mm, "radius": 0.25 * mm});
            skCircle(sketch, "E18.0.33.0", {"center": v(1.98, 85.56) * mm, "radius": 0.25 * mm});
            skCircle(sketch, "E18.2.33.0", {"center": v(4.52, 85.56) * mm, "radius": 0.25 * mm});
            skCircle(sketch, "E18.4.33.0", {"center": v(7.06, 85.56) * mm, "radius": 0.25 * mm});
            skCircle(sketch, "E18.6.33.0", {"center": v(9.6, 85.56) * mm, "radius": 0.25 * mm});
            skCircle(sketch, "E18.8.33.0", {"center": v(12.14, 85.56) * mm, "radius": 0.25 * mm});
            skCircle(sketch, "E18.10.33.0", {"center": v(14.68, 85.56) * mm, "radius": 0.25 * mm});
            skCircle(sketch, "E18.12.33.0", {"center": v(17.22, 85.56) * mm, "radius": 0.25 * mm});
            skCircle(sketch, "E18.14.33.0", {"center": v(19.76, 85.56) * mm, "radius": 0.25 * mm});
            skCircle(sketch, "E18.16.33.0", {"center": v(22.3, 85.56) * mm, "radius": 0.25 * mm});
            skCircle(sketch, "E18.18.33.0", {"center": v(24.84, 85.56) * mm, "radius": 0.25 * mm});
            skCircle(sketch, "E18.20.33.0", {"center": v(27.38, 85.56) * mm, "radius": 0.25 * mm});
            skCircle(sketch, "E18.22.33.0", {"center": v(29.92, 85.56) * mm, "radius": 0.25 * mm});
            skCircle(sketch, "E18.24.33.0", {"center": v(32.46, 85.56) * mm, "radius": 0.25 * mm});
            skCircle(sketch, "E18.26.33.0", {"center": v(35, 85.56) * mm, "radius": 0.25 * mm});
            skCircle(sketch, "E18.28.33.0", {"center": v(37.54, 85.56) * mm, "radius": 0.25 * mm});
            skCircle(sketch, "E18.30.33.0", {"center": v(40.08, 85.56) * mm, "radius": 0.25 * mm});
            skCircle(sketch, "E18.32.33.0", {"center": v(42.62, 85.56) * mm, "radius": 0.25 * mm});
            skCircle(sketch, "E18.34.33.0", {"center": v(45.16, 85.56) * mm, "radius": 0.25 * mm});
            skCircle(sketch, "E18.36.33.0", {"center": v(47.7, 85.56) * mm, "radius": 0.25 * mm});
            skCircle(sketch, "E18.38.33.0", {"center": v(50.24, 85.56) * mm, "radius": 0.25 * mm});
            skCircle(sketch, "E18.40.33.0", {"center": v(52.78, 85.56) * mm, "radius": 0.25 * mm});
            skCircle(sketch, "E18.42.33.0", {"center": v(55.32, 85.56) * mm, "radius": 0.25 * mm});
            skCircle(sketch, "E18.44.33.0", {"center": v(57.86, 85.56) * mm, "radius": 0.25 * mm});
            skCircle(sketch, "E18.46.33.0", {"center": v(60.4, 85.56) * mm, "radius": 0.25 * mm});
            skCircle(sketch, "E18.48.33.0", {"center": v(62.94, 85.56) * mm, "radius": 0.25 * mm});
            skCircle(sketch, "E18.50.33.0", {"center": v(65.48, 85.56) * mm, "radius": 0.25 * mm});
            skCircle(sketch, "E18.52.33.0", {"center": v(68.02, 85.56) * mm, "radius": 0.25 * mm});
            skCircle(sketch, "E18.0.34.0", {"center": v(1.98, 88.1) * mm, "radius": 0.25 * mm});
            skCircle(sketch, "E18.2.34.0", {"center": v(4.52, 88.1) * mm, "radius": 0.25 * mm});
            skCircle(sketch, "E18.4.34.0", {"center": v(7.06, 88.1) * mm, "radius": 0.25 * mm});
            skCircle(sketch, "E18.6.34.0", {"center": v(9.6, 88.1) * mm, "radius": 0.25 * mm});
            skCircle(sketch, "E18.8.34.0", {"center": v(12.14, 88.1) * mm, "radius": 0.25 * mm});
            skCircle(sketch, "E18.10.34.0", {"center": v(14.68, 88.1) * mm, "radius": 0.25 * mm});
            skCircle(sketch, "E18.12.34.0", {"center": v(17.22, 88.1) * mm, "radius": 0.25 * mm});
            skCircle(sketch, "E18.14.34.0", {"center": v(19.76, 88.1) * mm, "radius": 0.25 * mm});
            skCircle(sketch, "E18.16.34.0", {"center": v(22.3, 88.1) * mm, "radius": 0.25 * mm});
            skCircle(sketch, "E18.18.34.0", {"center": v(24.84, 88.1) * mm, "radius": 0.25 * mm});
            skCircle(sketch, "E18.20.34.0", {"center": v(27.38, 88.1) * mm, "radius": 0.25 * mm});
            skCircle(sketch, "E18.22.34.0", {"center": v(29.92, 88.1) * mm, "radius": 0.25 * mm});
            skCircle(sketch, "E18.24.34.0", {"center": v(32.46, 88.1) * mm, "radius": 0.25 * mm});
            skCircle(sketch, "E18.26.34.0", {"center": v(35, 88.1) * mm, "radius": 0.25 * mm});
            skCircle(sketch, "E18.28.34.0", {"center": v(37.54, 88.1) * mm, "radius": 0.25 * mm});
            skCircle(sketch, "E18.30.34.0", {"center": v(40.08, 88.1) * mm, "radius": 0.25 * mm});
            skCircle(sketch, "E18.32.34.0", {"center": v(42.62, 88.1) * mm, "radius": 0.25 * mm});
            skCircle(sketch, "E18.34.34.0", {"center": v(45.16, 88.1) * mm, "radius": 0.25 * mm});
            skCircle(sketch, "E18.36.34.0", {"center": v(47.7, 88.1) * mm, "radius": 0.25 * mm});
            skCircle(sketch, "E18.38.34.0", {"center": v(50.24, 88.1) * mm, "radius": 0.25 * mm});
            skCircle(sketch, "E18.40.34.0", {"center": v(52.78, 88.1) * mm, "radius": 0.25 * mm});
            skCircle(sketch, "E18.42.34.0", {"center": v(55.32, 88.1) * mm, "radius": 0.25 * mm});
            skCircle(sketch, "E18.44.34.0", {"center": v(57.86, 88.1) * mm, "radius": 0.25 * mm});
            skCircle(sketch, "E18.46.34.0", {"center": v(60.4, 88.1) * mm, "radius": 0.25 * mm});
            skCircle(sketch, "E18.48.34.0", {"center": v(62.94, 88.1) * mm, "radius": 0.25 * mm});
            skCircle(sketch, "E18.50.34.0", {"center": v(65.48, 88.1) * mm, "radius": 0.25 * mm});
            skCircle(sketch, "E18.52.34.0", {"center": v(68.02, 88.1) * mm, "radius": 0.25 * mm});
            skCircle(sketch, "E18.0.35.0", {"center": v(1.98, 90.64) * mm, "radius": 0.25 * mm});
            skCircle(sketch, "E18.2.35.0", {"center": v(4.52, 90.64) * mm, "radius": 0.25 * mm});
            skCircle(sketch, "E18.4.35.0", {"center": v(7.06, 90.64) * mm, "radius": 0.25 * mm});
            skCircle(sketch, "E18.6.35.0", {"center": v(9.6, 90.64) * mm, "radius": 0.25 * mm});
            skCircle(sketch, "E18.8.35.0", {"center": v(12.14, 90.64) * mm, "radius": 0.25 * mm});
            skCircle(sketch, "E18.10.35.0", {"center": v(14.68, 90.64) * mm, "radius": 0.25 * mm});
            skCircle(sketch, "E18.12.35.0", {"center": v(17.22, 90.64) * mm, "radius": 0.25 * mm});
            skCircle(sketch, "E18.14.35.0", {"center": v(19.76, 90.64) * mm, "radius": 0.25 * mm});
            skCircle(sketch, "E18.16.35.0", {"center": v(22.3, 90.64) * mm, "radius": 0.25 * mm});
            skCircle(sketch, "E18.18.35.0", {"center": v(24.84, 90.64) * mm, "radius": 0.25 * mm});
            skCircle(sketch, "E18.20.35.0", {"center": v(27.38, 90.64) * mm, "radius": 0.25 * mm});
            skCircle(sketch, "E18.22.35.0", {"center": v(29.92, 90.64) * mm, "radius": 0.25 * mm});
            skCircle(sketch, "E18.24.35.0", {"center": v(32.46, 90.64) * mm, "radius": 0.25 * mm});
            skCircle(sketch, "E18.26.35.0", {"center": v(35, 90.64) * mm, "radius": 0.25 * mm});
            skCircle(sketch, "E18.28.35.0", {"center": v(37.54, 90.64) * mm, "radius": 0.25 * mm});
            skCircle(sketch, "E18.30.35.0", {"center": v(40.08, 90.64) * mm, "radius": 0.25 * mm});
            skCircle(sketch, "E18.32.35.0", {"center": v(42.62, 90.64) * mm, "radius": 0.25 * mm});
            skCircle(sketch, "E18.34.35.0", {"center": v(45.16, 90.64) * mm, "radius": 0.25 * mm});
            skCircle(sketch, "E18.36.35.0", {"center": v(47.7, 90.64) * mm, "radius": 0.25 * mm});
            skCircle(sketch, "E18.38.35.0", {"center": v(50.24, 90.64) * mm, "radius": 0.25 * mm});
            skCircle(sketch, "E18.40.35.0", {"center": v(52.78, 90.64) * mm, "radius": 0.25 * mm});
            skCircle(sketch, "E18.42.35.0", {"center": v(55.32, 90.64) * mm, "radius": 0.25 * mm});
            skCircle(sketch, "E18.44.35.0", {"center": v(57.86, 90.64) * mm, "radius": 0.25 * mm});
            skCircle(sketch, "E18.46.35.0", {"center": v(60.4, 90.64) * mm, "radius": 0.25 * mm});
            skCircle(sketch, "E18.48.35.0", {"center": v(62.94, 90.64) * mm, "radius": 0.25 * mm});
            skCircle(sketch, "E18.50.35.0", {"center": v(65.48, 90.64) * mm, "radius": 0.25 * mm});
            skCircle(sketch, "E18.52.35.0", {"center": v(68.02, 90.64) * mm, "radius": 0.25 * mm});
            skCircle(sketch, "E18.0.36.0", {"center": v(1.98, 93.18) * mm, "radius": 0.25 * mm});
            skCircle(sketch, "E18.2.36.0", {"center": v(4.52, 93.18) * mm, "radius": 0.25 * mm});
            skCircle(sketch, "E18.4.36.0", {"center": v(7.06, 93.18) * mm, "radius": 0.25 * mm});
            skCircle(sketch, "E18.6.36.0", {"center": v(9.6, 93.18) * mm, "radius": 0.25 * mm});
            skCircle(sketch, "E18.8.36.0", {"center": v(12.14, 93.18) * mm, "radius": 0.25 * mm});
            skCircle(sketch, "E18.10.36.0", {"center": v(14.68, 93.18) * mm, "radius": 0.25 * mm});
            skCircle(sketch, "E18.12.36.0", {"center": v(17.22, 93.18) * mm, "radius": 0.25 * mm});
            skCircle(sketch, "E18.14.36.0", {"center": v(19.76, 93.18) * mm, "radius": 0.25 * mm});
            skCircle(sketch, "E18.16.36.0", {"center": v(22.3, 93.18) * mm, "radius": 0.25 * mm});
            skCircle(sketch, "E18.18.36.0", {"center": v(24.84, 93.18) * mm, "radius": 0.25 * mm});
            skCircle(sketch, "E18.20.36.0", {"center": v(27.38, 93.18) * mm, "radius": 0.25 * mm});
            skCircle(sketch, "E18.22.36.0", {"center": v(29.92, 93.18) * mm, "radius": 0.25 * mm});
            skCircle(sketch, "E18.24.36.0", {"center": v(32.46, 93.18) * mm, "radius": 0.25 * mm});
            skCircle(sketch, "E18.26.36.0", {"center": v(35, 93.18) * mm, "radius": 0.25 * mm});
            skCircle(sketch, "E18.28.36.0", {"center": v(37.54, 93.18) * mm, "radius": 0.25 * mm});
            skCircle(sketch, "E18.30.36.0", {"center": v(40.08, 93.18) * mm, "radius": 0.25 * mm});
            skCircle(sketch, "E18.32.36.0", {"center": v(42.62, 93.18) * mm, "radius": 0.25 * mm});
            skCircle(sketch, "E18.34.36.0", {"center": v(45.16, 93.18) * mm, "radius": 0.25 * mm});
            skCircle(sketch, "E18.36.36.0", {"center": v(47.7, 93.18) * mm, "radius": 0.25 * mm});
            skCircle(sketch, "E18.38.36.0", {"center": v(50.24, 93.18) * mm, "radius": 0.25 * mm});
            skCircle(sketch, "E18.40.36.0", {"center": v(52.78, 93.18) * mm, "radius": 0.25 * mm});
            skCircle(sketch, "E18.42.36.0", {"center": v(55.32, 93.18) * mm, "radius": 0.25 * mm});
            skCircle(sketch, "E18.44.36.0", {"center": v(57.86, 93.18) * mm, "radius": 0.25 * mm});
            skCircle(sketch, "E18.46.36.0", {"center": v(60.4, 93.18) * mm, "radius": 0.25 * mm});
            skCircle(sketch, "E18.48.36.0", {"center": v(62.94, 93.18) * mm, "radius": 0.25 * mm});
            skCircle(sketch, "E18.50.36.0", {"center": v(65.48, 93.18) * mm, "radius": 0.25 * mm});
            skCircle(sketch, "E18.52.36.0", {"center": v(68.02, 93.18) * mm, "radius": 0.25 * mm});
            skCircle(sketch, "E18.0.37.0", {"center": v(1.98, 95.72) * mm, "radius": 0.25 * mm});
            skCircle(sketch, "E18.2.37.0", {"center": v(4.52, 95.72) * mm, "radius": 0.25 * mm});
            skCircle(sketch, "E18.4.37.0", {"center": v(7.06, 95.72) * mm, "radius": 0.25 * mm});
            skCircle(sketch, "E18.6.37.0", {"center": v(9.6, 95.72) * mm, "radius": 0.25 * mm});
            skCircle(sketch, "E18.8.37.0", {"center": v(12.14, 95.72) * mm, "radius": 0.25 * mm});
            skCircle(sketch, "E18.10.37.0", {"center": v(14.68, 95.72) * mm, "radius": 0.25 * mm});
            skCircle(sketch, "E18.12.37.0", {"center": v(17.22, 95.72) * mm, "radius": 0.25 * mm});
            skCircle(sketch, "E18.14.37.0", {"center": v(19.76, 95.72) * mm, "radius": 0.25 * mm});
            skCircle(sketch, "E18.16.37.0", {"center": v(22.3, 95.72) * mm, "radius": 0.25 * mm});
            skCircle(sketch, "E18.18.37.0", {"center": v(24.84, 95.72) * mm, "radius": 0.25 * mm});
            skCircle(sketch, "E18.20.37.0", {"center": v(27.38, 95.72) * mm, "radius": 0.25 * mm});
            skCircle(sketch, "E18.22.37.0", {"center": v(29.92, 95.72) * mm, "radius": 0.25 * mm});
            skCircle(sketch, "E18.24.37.0", {"center": v(32.46, 95.72) * mm, "radius": 0.25 * mm});
            skCircle(sketch, "E18.26.37.0", {"center": v(35, 95.72) * mm, "radius": 0.25 * mm});
            skCircle(sketch, "E18.28.37.0", {"center": v(37.54, 95.72) * mm, "radius": 0.25 * mm});
            skCircle(sketch, "E18.30.37.0", {"center": v(40.08, 95.72) * mm, "radius": 0.25 * mm});
            skCircle(sketch, "E18.32.37.0", {"center": v(42.62, 95.72) * mm, "radius": 0.25 * mm});
            skCircle(sketch, "E18.34.37.0", {"center": v(45.16, 95.72) * mm, "radius": 0.25 * mm});
            skCircle(sketch, "E18.36.37.0", {"center": v(47.7, 95.72) * mm, "radius": 0.25 * mm});
            skCircle(sketch, "E18.38.37.0", {"center": v(50.24, 95.72) * mm, "radius": 0.25 * mm});
            skCircle(sketch, "E18.40.37.0", {"center": v(52.78, 95.72) * mm, "radius": 0.25 * mm});
            skCircle(sketch, "E18.42.37.0", {"center": v(55.32, 95.72) * mm, "radius": 0.25 * mm});
            skCircle(sketch, "E18.44.37.0", {"center": v(57.86, 95.72) * mm, "radius": 0.25 * mm});
            skCircle(sketch, "E18.46.37.0", {"center": v(60.4, 95.72) * mm, "radius": 0.25 * mm});
            skCircle(sketch, "E18.48.37.0", {"center": v(62.94, 95.72) * mm, "radius": 0.25 * mm});
            skCircle(sketch, "E18.50.37.0", {"center": v(65.48, 95.72) * mm, "radius": 0.25 * mm});
            skCircle(sketch, "E18.52.37.0", {"center": v(68.02, 95.72) * mm, "radius": 0.25 * mm});
            skCircle(sketch, "E18.0.38.0", {"center": v(1.98, 98.26) * mm, "radius": 0.25 * mm});
            skCircle(sketch, "E18.2.38.0", {"center": v(4.52, 98.26) * mm, "radius": 0.25 * mm});
            skCircle(sketch, "E18.4.38.0", {"center": v(7.06, 98.26) * mm, "radius": 0.25 * mm});
            skCircle(sketch, "E18.6.38.0", {"center": v(9.6, 98.26) * mm, "radius": 0.25 * mm});
            skCircle(sketch, "E18.8.38.0", {"center": v(12.14, 98.26) * mm, "radius": 0.25 * mm});
            skCircle(sketch, "E18.10.38.0", {"center": v(14.68, 98.26) * mm, "radius": 0.25 * mm});
            skCircle(sketch, "E18.12.38.0", {"center": v(17.22, 98.26) * mm, "radius": 0.25 * mm});
            skCircle(sketch, "E18.14.38.0", {"center": v(19.76, 98.26) * mm, "radius": 0.25 * mm});
            skCircle(sketch, "E18.16.38.0", {"center": v(22.3, 98.26) * mm, "radius": 0.25 * mm});
            skCircle(sketch, "E18.18.38.0", {"center": v(24.84, 98.26) * mm, "radius": 0.25 * mm});
            skCircle(sketch, "E18.20.38.0", {"center": v(27.38, 98.26) * mm, "radius": 0.25 * mm});
            skCircle(sketch, "E18.22.38.0", {"center": v(29.92, 98.26) * mm, "radius": 0.25 * mm});
            skCircle(sketch, "E18.24.38.0", {"center": v(32.46, 98.26) * mm, "radius": 0.25 * mm});
            skCircle(sketch, "E18.26.38.0", {"center": v(35, 98.26) * mm, "radius": 0.25 * mm});
            skCircle(sketch, "E18.28.38.0", {"center": v(37.54, 98.26) * mm, "radius": 0.25 * mm});
            skCircle(sketch, "E18.30.38.0", {"center": v(40.08, 98.26) * mm, "radius": 0.25 * mm});
            skCircle(sketch, "E18.32.38.0", {"center": v(42.62, 98.26) * mm, "radius": 0.25 * mm});
            skCircle(sketch, "E18.34.38.0", {"center": v(45.16, 98.26) * mm, "radius": 0.25 * mm});
            skCircle(sketch, "E18.36.38.0", {"center": v(47.7, 98.26) * mm, "radius": 0.25 * mm});
            skCircle(sketch, "E18.38.38.0", {"center": v(50.24, 98.26) * mm, "radius": 0.25 * mm});
            skCircle(sketch, "E18.40.38.0", {"center": v(52.78, 98.26) * mm, "radius": 0.25 * mm});
            skCircle(sketch, "E18.42.38.0", {"center": v(55.32, 98.26) * mm, "radius": 0.25 * mm});
            skCircle(sketch, "E18.44.38.0", {"center": v(57.86, 98.26) * mm, "radius": 0.25 * mm});
            skCircle(sketch, "E18.46.38.0", {"center": v(60.4, 98.26) * mm, "radius": 0.25 * mm});
            skCircle(sketch, "E18.48.38.0", {"center": v(62.94, 98.26) * mm, "radius": 0.25 * mm});
            skCircle(sketch, "E18.50.38.0", {"center": v(65.48, 98.26) * mm, "radius": 0.25 * mm});
            skCircle(sketch, "E18.52.38.0", {"center": v(68.02, 98.26) * mm, "radius": 0.25 * mm});
            skSolve(sketch);
        }
        {
            var Q0;
            {var subQ0=sQuery(id+"F0.wireOp",EDGE,"E10.0.10.0");var subQ1=sQuery(id+"F0.wireOp",EDGE,"E3.11.0.1");var subQ2=makeQuery(id+"F0.imprint","INTERSECT",VERTEX,{"derivedFrom":[subQ1,subQ0]});Q0=makeQuery(id+"F0.imprint","IMPRINT",FACE,{"disambiguationData":[TD([[makeQuery(id+"F0.imprint","IMPRINT",EDGE,{"disambiguationData":[TD([[subQ2,-1.0]])],"derivedFrom":subQ1}),1.0]])]});}
            var Q1;
            {var subQ0=sQuery(id+"F0.wireOp",EDGE,"E10.0.10.0");var subQ1=sQuery(id+"F0.wireOp",EDGE,"E3.12.0.0");var subQ2=makeQuery(id+"F0.imprint","INTERSECT",VERTEX,{"derivedFrom":[subQ1,subQ0]});Q1=makeQuery(id+"F0.imprint","IMPRINT",FACE,{"disambiguationData":[TD([[makeQuery(id+"F0.imprint","IMPRINT",EDGE,{"disambiguationData":[TD([[subQ2,-1.0]])],"derivedFrom":subQ1}),1.0]])]});}
            var Q2;
            {var subQ0=sQuery(id+"F0.wireOp",EDGE,"E10.0.10.0");var subQ1=sQuery(id+"F0.wireOp",EDGE,"E3.12.0.1");var subQ2=makeQuery(id+"F0.imprint","INTERSECT",VERTEX,{"derivedFrom":[subQ1,subQ0]});Q2=makeQuery(id+"F0.imprint","IMPRINT",FACE,{"disambiguationData":[TD([[makeQuery(id+"F0.imprint","IMPRINT",EDGE,{"disambiguationData":[TD([[subQ2,-1.0]])],"derivedFrom":subQ1}),1.0]])]});}
            var Q3;
            {var subQ0=sQuery(id+"F0.wireOp",EDGE,"E10.0.10.0");var subQ1=sQuery(id+"F0.wireOp",EDGE,"E3.13.0.0");var subQ2=makeQuery(id+"F0.imprint","INTERSECT",VERTEX,{"derivedFrom":[subQ1,subQ0]});Q3=makeQuery(id+"F0.imprint","IMPRINT",FACE,{"disambiguationData":[TD([[makeQuery(id+"F0.imprint","IMPRINT",EDGE,{"disambiguationData":[TD([[subQ2,-1.0]])],"derivedFrom":subQ1}),1.0]])]});}
            var Q4;
            {var subQ0=sQuery(id+"F0.wireOp",EDGE,"E10.3.10.0");var subQ1=sQuery(id+"F0.wireOp",EDGE,"E3.13.0.0");var subQ2=makeQuery(id+"F0.imprint","INTERSECT",VERTEX,{"derivedFrom":[subQ1,subQ0]});Q4=makeQuery(id+"F0.imprint","IMPRINT",FACE,{"disambiguationData":[TD([[makeQuery(id+"F0.imprint","IMPRINT",EDGE,{"disambiguationData":[TD([[subQ2,-1.0]])],"derivedFrom":subQ1}),1.0]])]});}
            var Q5;
            {var subQ0=sQuery(id+"F0.wireOp",EDGE,"E10.0.11.0");var subQ1=sQuery(id+"F0.wireOp",EDGE,"E3.13.0.0");var subQ2=makeQuery(id+"F0.imprint","INTERSECT",VERTEX,{"derivedFrom":[subQ1,subQ0]});Q5=makeQuery(id+"F0.imprint","IMPRINT",FACE,{"disambiguationData":[TD([[makeQuery(id+"F0.imprint","IMPRINT",EDGE,{"disambiguationData":[TD([[subQ2,-1.0]])],"derivedFrom":subQ1}),1.0]])]});}
            var Q6;
            {var subQ0=sQuery(id+"F0.wireOp",EDGE,"E10.0.11.0");var subQ1=sQuery(id+"F0.wireOp",EDGE,"E3.12.0.1");var subQ2=makeQuery(id+"F0.imprint","INTERSECT",VERTEX,{"derivedFrom":[subQ1,subQ0]});Q6=makeQuery(id+"F0.imprint","IMPRINT",FACE,{"disambiguationData":[TD([[makeQuery(id+"F0.imprint","IMPRINT",EDGE,{"disambiguationData":[TD([[subQ2,-1.0]])],"derivedFrom":subQ1}),1.0]])]});}
            var Q7;
            {var subQ0=sQuery(id+"F0.wireOp",EDGE,"E10.0.11.0");var subQ1=sQuery(id+"F0.wireOp",EDGE,"E3.12.0.0");var subQ2=makeQuery(id+"F0.imprint","INTERSECT",VERTEX,{"derivedFrom":[subQ1,subQ0]});Q7=makeQuery(id+"F0.imprint","IMPRINT",FACE,{"disambiguationData":[TD([[makeQuery(id+"F0.imprint","IMPRINT",EDGE,{"disambiguationData":[TD([[subQ2,-1.0]])],"derivedFrom":subQ1}),1.0]])]});}
            var Q8;
            {var subQ0=sQuery(id+"F0.wireOp",EDGE,"E10.0.11.0");var subQ1=sQuery(id+"F0.wireOp",EDGE,"E3.11.0.1");var subQ2=makeQuery(id+"F0.imprint","INTERSECT",VERTEX,{"derivedFrom":[subQ1,subQ0]});Q8=makeQuery(id+"F0.imprint","IMPRINT",FACE,{"disambiguationData":[TD([[makeQuery(id+"F0.imprint","IMPRINT",EDGE,{"disambiguationData":[TD([[subQ2,-1.0]])],"derivedFrom":subQ1}),1.0]])]});}
            var Q9;
            {var subQ0=sQuery(id+"F0.wireOp",EDGE,"E10.0.11.0");var subQ1=sQuery(id+"F0.wireOp",EDGE,"E3.11.0.0");var subQ2=makeQuery(id+"F0.imprint","INTERSECT",VERTEX,{"derivedFrom":[subQ1,subQ0]});Q9=makeQuery(id+"F0.imprint","IMPRINT",FACE,{"disambiguationData":[TD([[makeQuery(id+"F0.imprint","IMPRINT",EDGE,{"disambiguationData":[TD([[subQ2,-1.0]])],"derivedFrom":subQ1}),1.0]])]});}
            var Q10;
            {var subQ0=sQuery(id+"F0.wireOp",EDGE,"E10.3.10.0");var subQ1=sQuery(id+"F0.wireOp",EDGE,"E3.11.0.0");var subQ2=makeQuery(id+"F0.imprint","INTERSECT",VERTEX,{"derivedFrom":[subQ1,subQ0]});Q10=makeQuery(id+"F0.imprint","IMPRINT",FACE,{"disambiguationData":[TD([[makeQuery(id+"F0.imprint","IMPRINT",EDGE,{"disambiguationData":[TD([[subQ2,-1.0]])],"derivedFrom":subQ1}),1.0]])]});}
            var Q11;
            {var subQ0=sQuery(id+"F0.wireOp",EDGE,"E10.0.10.0");var subQ1=sQuery(id+"F0.wireOp",EDGE,"E3.11.0.0");var subQ2=makeQuery(id+"F0.imprint","INTERSECT",VERTEX,{"derivedFrom":[subQ1,subQ0]});Q11=makeQuery(id+"F0.imprint","IMPRINT",FACE,{"disambiguationData":[TD([[makeQuery(id+"F0.imprint","IMPRINT",EDGE,{"disambiguationData":[TD([[subQ2,-1.0]])],"derivedFrom":subQ1}),1.0]])]});}
            var Q12;
            {var subQ0=sQuery(id+"F0.wireOp",EDGE,"E10.0.12.0");var subQ1=sQuery(id+"F0.wireOp",EDGE,"E3.12.0.0");var subQ2=makeQuery(id+"F0.imprint","INTERSECT",VERTEX,{"derivedFrom":[subQ1,subQ0]});Q12=makeQuery(id+"F0.imprint","IMPRINT",FACE,{"disambiguationData":[TD([[makeQuery(id+"F0.imprint","IMPRINT",EDGE,{"disambiguationData":[TD([[subQ2,-1.0]])],"derivedFrom":subQ1}),1.0]])]});}
            var Q13;
            {var subQ0=sQuery(id+"F0.wireOp",EDGE,"E10.3.11.0");var subQ1=sQuery(id+"F0.wireOp",EDGE,"E3.13.0.0");var subQ2=makeQuery(id+"F0.imprint","INTERSECT",VERTEX,{"derivedFrom":[subQ1,subQ0]});Q13=makeQuery(id+"F0.imprint","IMPRINT",FACE,{"disambiguationData":[TD([[makeQuery(id+"F0.imprint","IMPRINT",EDGE,{"disambiguationData":[TD([[subQ2,-1.0]])],"derivedFrom":subQ1}),1.0]])]});}
            var Q14;
            {var subQ0=sQuery(id+"F0.wireOp",EDGE,"E10.0.12.0");var subQ1=sQuery(id+"F0.wireOp",EDGE,"E3.13.0.0");var subQ2=makeQuery(id+"F0.imprint","INTERSECT",VERTEX,{"derivedFrom":[subQ1,subQ0]});Q14=makeQuery(id+"F0.imprint","IMPRINT",FACE,{"disambiguationData":[TD([[makeQuery(id+"F0.imprint","IMPRINT",EDGE,{"disambiguationData":[TD([[subQ2,-1.0]])],"derivedFrom":subQ1}),1.0]])]});}
            var Q15;
            {var subQ0=sQuery(id+"F0.wireOp",EDGE,"E10.0.12.0");var subQ1=sQuery(id+"F0.wireOp",EDGE,"E3.12.0.1");var subQ2=makeQuery(id+"F0.imprint","INTERSECT",VERTEX,{"derivedFrom":[subQ1,subQ0]});Q15=makeQuery(id+"F0.imprint","IMPRINT",FACE,{"disambiguationData":[TD([[makeQuery(id+"F0.imprint","IMPRINT",EDGE,{"disambiguationData":[TD([[subQ2,-1.0]])],"derivedFrom":subQ1}),1.0]])]});}
            var Q16;
            {var subQ0=sQuery(id+"F0.wireOp",EDGE,"E10.3.12.0");var subQ1=sQuery(id+"F0.wireOp",EDGE,"E3.13.0.0");var subQ2=makeQuery(id+"F0.imprint","INTERSECT",VERTEX,{"derivedFrom":[subQ1,subQ0]});Q16=makeQuery(id+"F0.imprint","IMPRINT",FACE,{"disambiguationData":[TD([[makeQuery(id+"F0.imprint","IMPRINT",EDGE,{"disambiguationData":[TD([[subQ2,-1.0]])],"derivedFrom":subQ1}),1.0]])]});}
            var Q17;
            {var subQ0=sQuery(id+"F0.wireOp",EDGE,"E10.0.13.0");var subQ1=sQuery(id+"F0.wireOp",EDGE,"E3.13.0.0");var subQ2=makeQuery(id+"F0.imprint","INTERSECT",VERTEX,{"derivedFrom":[subQ1,subQ0]});Q17=makeQuery(id+"F0.imprint","IMPRINT",FACE,{"disambiguationData":[TD([[makeQuery(id+"F0.imprint","IMPRINT",EDGE,{"disambiguationData":[TD([[subQ2,-1.0]])],"derivedFrom":subQ1}),1.0]])]});}
            var Q18;
            {var subQ0=sQuery(id+"F0.wireOp",EDGE,"E10.0.13.0");var subQ1=sQuery(id+"F0.wireOp",EDGE,"E3.12.0.1");var subQ2=makeQuery(id+"F0.imprint","INTERSECT",VERTEX,{"derivedFrom":[subQ1,subQ0]});Q18=makeQuery(id+"F0.imprint","IMPRINT",FACE,{"disambiguationData":[TD([[makeQuery(id+"F0.imprint","IMPRINT",EDGE,{"disambiguationData":[TD([[subQ2,-1.0]])],"derivedFrom":subQ1}),1.0]])]});}
            var Q19;
            {var subQ0=sQuery(id+"F0.wireOp",EDGE,"E10.0.13.0");var subQ1=sQuery(id+"F0.wireOp",EDGE,"E3.12.0.0");var subQ2=makeQuery(id+"F0.imprint","INTERSECT",VERTEX,{"derivedFrom":[subQ1,subQ0]});Q19=makeQuery(id+"F0.imprint","IMPRINT",FACE,{"disambiguationData":[TD([[makeQuery(id+"F0.imprint","IMPRINT",EDGE,{"disambiguationData":[TD([[subQ2,-1.0]])],"derivedFrom":subQ1}),1.0]])]});}
            var Q20;
            {var subQ0=sQuery(id+"F0.wireOp",EDGE,"E10.3.13.0");var subQ1=sQuery(id+"F0.wireOp",EDGE,"E3.13.0.0");var subQ2=makeQuery(id+"F0.imprint","INTERSECT",VERTEX,{"derivedFrom":[subQ1,subQ0]});Q20=makeQuery(id+"F0.imprint","IMPRINT",FACE,{"disambiguationData":[TD([[makeQuery(id+"F0.imprint","IMPRINT",EDGE,{"disambiguationData":[TD([[subQ2,-1.0]])],"derivedFrom":subQ1}),1.0]])]});}
            var Q21;
            {var subQ0=sQuery(id+"F0.wireOp",EDGE,"E10.0.14.0");var subQ1=sQuery(id+"F0.wireOp",EDGE,"E3.13.0.0");var subQ2=makeQuery(id+"F0.imprint","INTERSECT",VERTEX,{"derivedFrom":[subQ1,subQ0]});Q21=makeQuery(id+"F0.imprint","IMPRINT",FACE,{"disambiguationData":[TD([[makeQuery(id+"F0.imprint","IMPRINT",EDGE,{"disambiguationData":[TD([[subQ2,-1.0]])],"derivedFrom":subQ1}),1.0]])]});}
            var Q22;
            {var subQ0=sQuery(id+"F0.wireOp",EDGE,"E10.0.14.0");var subQ1=sQuery(id+"F0.wireOp",EDGE,"E3.12.0.1");var subQ2=makeQuery(id+"F0.imprint","INTERSECT",VERTEX,{"derivedFrom":[subQ1,subQ0]});Q22=makeQuery(id+"F0.imprint","IMPRINT",FACE,{"disambiguationData":[TD([[makeQuery(id+"F0.imprint","IMPRINT",EDGE,{"disambiguationData":[TD([[subQ2,-1.0]])],"derivedFrom":subQ1}),1.0]])]});}
            var Q23;
            {var subQ0=sQuery(id+"F0.wireOp",EDGE,"E10.0.14.0");var subQ1=sQuery(id+"F0.wireOp",EDGE,"E3.12.0.0");var subQ2=makeQuery(id+"F0.imprint","INTERSECT",VERTEX,{"derivedFrom":[subQ1,subQ0]});Q23=makeQuery(id+"F0.imprint","IMPRINT",FACE,{"disambiguationData":[TD([[makeQuery(id+"F0.imprint","IMPRINT",EDGE,{"disambiguationData":[TD([[subQ2,-1.0]])],"derivedFrom":subQ1}),1.0]])]});}
            var Q24;
            {var subQ0=sQuery(id+"F0.wireOp",EDGE,"E10.0.15.0");var subQ1=sQuery(id+"F0.wireOp",EDGE,"E3.12.0.1");var subQ2=makeQuery(id+"F0.imprint","INTERSECT",VERTEX,{"derivedFrom":[subQ1,subQ0]});Q24=makeQuery(id+"F0.imprint","IMPRINT",FACE,{"disambiguationData":[TD([[makeQuery(id+"F0.imprint","IMPRINT",EDGE,{"disambiguationData":[TD([[subQ2,-1.0]])],"derivedFrom":subQ1}),1.0]])]});}
            var Q25;
            {var subQ0=sQuery(id+"F0.wireOp",EDGE,"E10.3.14.0");var subQ1=sQuery(id+"F0.wireOp",EDGE,"E3.13.0.0");var subQ2=makeQuery(id+"F0.imprint","INTERSECT",VERTEX,{"derivedFrom":[subQ1,subQ0]});Q25=makeQuery(id+"F0.imprint","IMPRINT",FACE,{"disambiguationData":[TD([[makeQuery(id+"F0.imprint","IMPRINT",EDGE,{"disambiguationData":[TD([[subQ2,-1.0]])],"derivedFrom":subQ1}),1.0]])]});}
            var Q26;
            {var subQ0=sQuery(id+"F0.wireOp",EDGE,"E10.0.15.0");var subQ1=sQuery(id+"F0.wireOp",EDGE,"E3.13.0.0");var subQ2=makeQuery(id+"F0.imprint","INTERSECT",VERTEX,{"derivedFrom":[subQ1,subQ0]});Q26=makeQuery(id+"F0.imprint","IMPRINT",FACE,{"disambiguationData":[TD([[makeQuery(id+"F0.imprint","IMPRINT",EDGE,{"disambiguationData":[TD([[subQ2,-1.0]])],"derivedFrom":subQ1}),1.0]])]});}
            var Q27;
            {var subQ0=sQuery(id+"F0.wireOp",EDGE,"E10.3.15.0");var subQ1=sQuery(id+"F0.wireOp",EDGE,"E3.13.0.0");var subQ2=makeQuery(id+"F0.imprint","INTERSECT",VERTEX,{"derivedFrom":[subQ1,subQ0]});Q27=makeQuery(id+"F0.imprint","IMPRINT",FACE,{"disambiguationData":[TD([[makeQuery(id+"F0.imprint","IMPRINT",EDGE,{"disambiguationData":[TD([[subQ2,-1.0]])],"derivedFrom":subQ1}),1.0]])]});}
            var Q28;
            {var subQ0=sQuery(id+"F0.wireOp",EDGE,"E10.0.15.0");var subQ1=sQuery(id+"F0.wireOp",EDGE,"E3.12.0.0");var subQ2=makeQuery(id+"F0.imprint","INTERSECT",VERTEX,{"derivedFrom":[subQ1,subQ0]});Q28=makeQuery(id+"F0.imprint","IMPRINT",FACE,{"disambiguationData":[TD([[makeQuery(id+"F0.imprint","IMPRINT",EDGE,{"disambiguationData":[TD([[subQ2,-1.0]])],"derivedFrom":subQ1}),1.0]])]});}
            var Q29;
            {var subQ0=sQuery(id+"F0.wireOp",EDGE,"E10.0.16.0");var subQ1=sQuery(id+"F0.wireOp",EDGE,"E3.11.0.0");var subQ2=makeQuery(id+"F0.imprint","INTERSECT",VERTEX,{"derivedFrom":[subQ1,subQ0]});Q29=makeQuery(id+"F0.imprint","IMPRINT",FACE,{"disambiguationData":[TD([[makeQuery(id+"F0.imprint","IMPRINT",EDGE,{"disambiguationData":[TD([[subQ2,-1.0]])],"derivedFrom":subQ1}),1.0]])]});}
            var Q30;
            {var subQ0=sQuery(id+"F0.wireOp",EDGE,"E10.0.16.0");var subQ1=sQuery(id+"F0.wireOp",EDGE,"E3.11.0.1");var subQ2=makeQuery(id+"F0.imprint","INTERSECT",VERTEX,{"derivedFrom":[subQ1,subQ0]});Q30=makeQuery(id+"F0.imprint","IMPRINT",FACE,{"disambiguationData":[TD([[makeQuery(id+"F0.imprint","IMPRINT",EDGE,{"disambiguationData":[TD([[subQ2,-1.0]])],"derivedFrom":subQ1}),1.0]])]});}
            var Q31;
            {var subQ0=sQuery(id+"F0.wireOp",EDGE,"E10.0.16.0");var subQ1=sQuery(id+"F0.wireOp",EDGE,"E3.12.0.0");var subQ2=makeQuery(id+"F0.imprint","INTERSECT",VERTEX,{"derivedFrom":[subQ1,subQ0]});Q31=makeQuery(id+"F0.imprint","IMPRINT",FACE,{"disambiguationData":[TD([[makeQuery(id+"F0.imprint","IMPRINT",EDGE,{"disambiguationData":[TD([[subQ2,-1.0]])],"derivedFrom":subQ1}),1.0]])]});}
            var Q32;
            {var subQ0=sQuery(id+"F0.wireOp",EDGE,"E10.0.16.0");var subQ1=sQuery(id+"F0.wireOp",EDGE,"E3.12.0.1");var subQ2=makeQuery(id+"F0.imprint","INTERSECT",VERTEX,{"derivedFrom":[subQ1,subQ0]});Q32=makeQuery(id+"F0.imprint","IMPRINT",FACE,{"disambiguationData":[TD([[makeQuery(id+"F0.imprint","IMPRINT",EDGE,{"disambiguationData":[TD([[subQ2,-1.0]])],"derivedFrom":subQ1}),1.0]])]});}
            var Q33;
            {var subQ0=sQuery(id+"F0.wireOp",EDGE,"E10.0.16.0");var subQ1=sQuery(id+"F0.wireOp",EDGE,"E3.13.0.0");var subQ2=makeQuery(id+"F0.imprint","INTERSECT",VERTEX,{"derivedFrom":[subQ1,subQ0]});Q33=makeQuery(id+"F0.imprint","IMPRINT",FACE,{"disambiguationData":[TD([[makeQuery(id+"F0.imprint","IMPRINT",EDGE,{"disambiguationData":[TD([[subQ2,-1.0]])],"derivedFrom":subQ1}),1.0]])]});}
            var Q34;
            {var subQ0=sQuery(id+"F0.wireOp",EDGE,"E10.3.16.0");var subQ1=sQuery(id+"F0.wireOp",EDGE,"E3.13.0.0");var subQ2=makeQuery(id+"F0.imprint","INTERSECT",VERTEX,{"derivedFrom":[subQ1,subQ0]});Q34=makeQuery(id+"F0.imprint","IMPRINT",FACE,{"disambiguationData":[TD([[makeQuery(id+"F0.imprint","IMPRINT",EDGE,{"disambiguationData":[TD([[subQ2,-1.0]])],"derivedFrom":subQ1}),1.0]])]});}
            var Q35;
            {var subQ0=sQuery(id+"F0.wireOp",EDGE,"E10.0.17.0");var subQ1=sQuery(id+"F0.wireOp",EDGE,"E3.13.0.0");var subQ2=makeQuery(id+"F0.imprint","INTERSECT",VERTEX,{"derivedFrom":[subQ1,subQ0]});Q35=makeQuery(id+"F0.imprint","IMPRINT",FACE,{"disambiguationData":[TD([[makeQuery(id+"F0.imprint","IMPRINT",EDGE,{"disambiguationData":[TD([[subQ2,-1.0]])],"derivedFrom":subQ1}),1.0]])]});}
            var Q36;
            {var subQ0=sQuery(id+"F0.wireOp",EDGE,"E10.0.17.0");var subQ1=sQuery(id+"F0.wireOp",EDGE,"E3.12.0.1");var subQ2=makeQuery(id+"F0.imprint","INTERSECT",VERTEX,{"derivedFrom":[subQ1,subQ0]});Q36=makeQuery(id+"F0.imprint","IMPRINT",FACE,{"disambiguationData":[TD([[makeQuery(id+"F0.imprint","IMPRINT",EDGE,{"disambiguationData":[TD([[subQ2,-1.0]])],"derivedFrom":subQ1}),1.0]])]});}
            var Q37;
            {var subQ0=sQuery(id+"F0.wireOp",EDGE,"E10.0.17.0");var subQ1=sQuery(id+"F0.wireOp",EDGE,"E3.12.0.0");var subQ2=makeQuery(id+"F0.imprint","INTERSECT",VERTEX,{"derivedFrom":[subQ1,subQ0]});Q37=makeQuery(id+"F0.imprint","IMPRINT",FACE,{"disambiguationData":[TD([[makeQuery(id+"F0.imprint","IMPRINT",EDGE,{"disambiguationData":[TD([[subQ2,-1.0]])],"derivedFrom":subQ1}),1.0]])]});}
            var Q38;
            {var subQ0=sQuery(id+"F0.wireOp",EDGE,"E10.0.17.0");var subQ1=sQuery(id+"F0.wireOp",EDGE,"E3.11.0.1");var subQ2=makeQuery(id+"F0.imprint","INTERSECT",VERTEX,{"derivedFrom":[subQ1,subQ0]});Q38=makeQuery(id+"F0.imprint","IMPRINT",FACE,{"disambiguationData":[TD([[makeQuery(id+"F0.imprint","IMPRINT",EDGE,{"disambiguationData":[TD([[subQ2,-1.0]])],"derivedFrom":subQ1}),1.0]])]});}
            var Q39;
            {var subQ0=sQuery(id+"F0.wireOp",EDGE,"E10.0.17.0");var subQ1=sQuery(id+"F0.wireOp",EDGE,"E3.11.0.0");var subQ2=makeQuery(id+"F0.imprint","INTERSECT",VERTEX,{"derivedFrom":[subQ1,subQ0]});Q39=makeQuery(id+"F0.imprint","IMPRINT",FACE,{"disambiguationData":[TD([[makeQuery(id+"F0.imprint","IMPRINT",EDGE,{"disambiguationData":[TD([[subQ2,-1.0]])],"derivedFrom":subQ1}),1.0]])]});}
            var Q40;
            {var subQ0=sQuery(id+"F0.wireOp",EDGE,"E10.3.16.0");var subQ1=sQuery(id+"F0.wireOp",EDGE,"E3.11.0.0");var subQ2=makeQuery(id+"F0.imprint","INTERSECT",VERTEX,{"derivedFrom":[subQ1,subQ0]});Q40=makeQuery(id+"F0.imprint","IMPRINT",FACE,{"disambiguationData":[TD([[makeQuery(id+"F0.imprint","IMPRINT",EDGE,{"disambiguationData":[TD([[subQ2,-1.0]])],"derivedFrom":subQ1}),1.0]])]});}
            var Q41;
            {var subQ0=sQuery(id+"F0.wireOp",EDGE,"E10.0.18.0");var subQ1=sQuery(id+"F0.wireOp",EDGE,"E3.13.0.0");var subQ2=makeQuery(id+"F0.imprint","INTERSECT",VERTEX,{"derivedFrom":[subQ1,subQ0]});Q41=makeQuery(id+"F0.imprint","IMPRINT",FACE,{"disambiguationData":[TD([[makeQuery(id+"F0.imprint","IMPRINT",EDGE,{"disambiguationData":[TD([[subQ2,-1.0]])],"derivedFrom":subQ1}),1.0]])]});}
            var Q42;
            {var subQ0=sQuery(id+"F0.wireOp",EDGE,"E10.0.18.0");var subQ1=sQuery(id+"F0.wireOp",EDGE,"E3.12.0.1");var subQ2=makeQuery(id+"F0.imprint","INTERSECT",VERTEX,{"derivedFrom":[subQ1,subQ0]});Q42=makeQuery(id+"F0.imprint","IMPRINT",FACE,{"disambiguationData":[TD([[makeQuery(id+"F0.imprint","IMPRINT",EDGE,{"disambiguationData":[TD([[subQ2,-1.0]])],"derivedFrom":subQ1}),1.0]])]});}
            var Q43;
            {var subQ0=sQuery(id+"F0.wireOp",EDGE,"E10.0.18.0");var subQ1=sQuery(id+"F0.wireOp",EDGE,"E3.12.0.0");var subQ2=makeQuery(id+"F0.imprint","INTERSECT",VERTEX,{"derivedFrom":[subQ1,subQ0]});Q43=makeQuery(id+"F0.imprint","IMPRINT",FACE,{"disambiguationData":[TD([[makeQuery(id+"F0.imprint","IMPRINT",EDGE,{"disambiguationData":[TD([[subQ2,-1.0]])],"derivedFrom":subQ1}),1.0]])]});}
            var Q44;
            {var subQ0=sQuery(id+"F0.wireOp",EDGE,"E10.3.18.0");var subQ1=sQuery(id+"F0.wireOp",EDGE,"E3.13.0.0");var subQ2=makeQuery(id+"F0.imprint","INTERSECT",VERTEX,{"derivedFrom":[subQ1,subQ0]});Q44=makeQuery(id+"F0.imprint","IMPRINT",FACE,{"disambiguationData":[TD([[makeQuery(id+"F0.imprint","IMPRINT",EDGE,{"disambiguationData":[TD([[subQ2,-1.0]])],"derivedFrom":subQ1}),1.0]])]});}
            var Q45;
            {var subQ0=sQuery(id+"F0.wireOp",EDGE,"E10.0.19.0");var subQ1=sQuery(id+"F0.wireOp",EDGE,"E3.13.0.0");var subQ2=makeQuery(id+"F0.imprint","INTERSECT",VERTEX,{"derivedFrom":[subQ1,subQ0]});Q45=makeQuery(id+"F0.imprint","IMPRINT",FACE,{"disambiguationData":[TD([[makeQuery(id+"F0.imprint","IMPRINT",EDGE,{"disambiguationData":[TD([[subQ2,-1.0]])],"derivedFrom":subQ1}),1.0]])]});}
            var Q46;
            {var subQ0=sQuery(id+"F0.wireOp",EDGE,"E10.3.19.0");var subQ1=sQuery(id+"F0.wireOp",EDGE,"E3.13.0.0");var subQ2=makeQuery(id+"F0.imprint","INTERSECT",VERTEX,{"derivedFrom":[subQ1,subQ0]});Q46=makeQuery(id+"F0.imprint","IMPRINT",FACE,{"disambiguationData":[TD([[makeQuery(id+"F0.imprint","IMPRINT",EDGE,{"disambiguationData":[TD([[subQ2,-1.0]])],"derivedFrom":subQ1}),1.0]])]});}
            var Q47;
            {var subQ0=sQuery(id+"F0.wireOp",EDGE,"E10.0.20.0");var subQ1=sQuery(id+"F0.wireOp",EDGE,"E3.13.0.0");var subQ2=makeQuery(id+"F0.imprint","INTERSECT",VERTEX,{"derivedFrom":[subQ1,subQ0]});Q47=makeQuery(id+"F0.imprint","IMPRINT",FACE,{"disambiguationData":[TD([[makeQuery(id+"F0.imprint","IMPRINT",EDGE,{"disambiguationData":[TD([[subQ2,-1.0]])],"derivedFrom":subQ1}),1.0]])]});}
            var Q48;
            {var subQ0=sQuery(id+"F0.wireOp",EDGE,"E10.3.20.0");var subQ1=sQuery(id+"F0.wireOp",EDGE,"E3.13.0.0");var subQ2=makeQuery(id+"F0.imprint","INTERSECT",VERTEX,{"derivedFrom":[subQ1,subQ0]});Q48=makeQuery(id+"F0.imprint","IMPRINT",FACE,{"disambiguationData":[TD([[makeQuery(id+"F0.imprint","IMPRINT",EDGE,{"disambiguationData":[TD([[subQ2,-1.0]])],"derivedFrom":subQ1}),1.0]])]});}
            var Q49;
            {var subQ0=sQuery(id+"F0.wireOp",EDGE,"E10.0.21.0");var subQ1=sQuery(id+"F0.wireOp",EDGE,"E3.13.0.0");var subQ2=makeQuery(id+"F0.imprint","INTERSECT",VERTEX,{"derivedFrom":[subQ1,subQ0]});Q49=makeQuery(id+"F0.imprint","IMPRINT",FACE,{"disambiguationData":[TD([[makeQuery(id+"F0.imprint","IMPRINT",EDGE,{"disambiguationData":[TD([[subQ2,-1.0]])],"derivedFrom":subQ1}),1.0]])]});}
            var Q50;
            {var subQ0=sQuery(id+"F0.wireOp",EDGE,"E10.3.21.0");var subQ1=sQuery(id+"F0.wireOp",EDGE,"E3.13.0.0");var subQ2=makeQuery(id+"F0.imprint","INTERSECT",VERTEX,{"derivedFrom":[subQ1,subQ0]});Q50=makeQuery(id+"F0.imprint","IMPRINT",FACE,{"disambiguationData":[TD([[makeQuery(id+"F0.imprint","IMPRINT",EDGE,{"disambiguationData":[TD([[subQ2,-1.0]])],"derivedFrom":subQ1}),1.0]])]});}
            var Q51;
            {var subQ0=sQuery(id+"F0.wireOp",EDGE,"E10.0.22.0");var subQ1=sQuery(id+"F0.wireOp",EDGE,"E3.13.0.0");var subQ2=makeQuery(id+"F0.imprint","INTERSECT",VERTEX,{"derivedFrom":[subQ1,subQ0]});Q51=makeQuery(id+"F0.imprint","IMPRINT",FACE,{"disambiguationData":[TD([[makeQuery(id+"F0.imprint","IMPRINT",EDGE,{"disambiguationData":[TD([[subQ2,-1.0]])],"derivedFrom":subQ1}),1.0]])]});}
            var Q52;
            {var subQ0=sQuery(id+"F0.wireOp",EDGE,"E10.3.22.0");var subQ1=sQuery(id+"F0.wireOp",EDGE,"E3.13.0.0");var subQ2=makeQuery(id+"F0.imprint","INTERSECT",VERTEX,{"derivedFrom":[subQ1,subQ0]});Q52=makeQuery(id+"F0.imprint","IMPRINT",FACE,{"disambiguationData":[TD([[makeQuery(id+"F0.imprint","IMPRINT",EDGE,{"disambiguationData":[TD([[subQ2,-1.0]])],"derivedFrom":subQ1}),1.0]])]});}
            var Q53;
            {var subQ0=sQuery(id+"F0.wireOp",EDGE,"E10.0.23.0");var subQ1=sQuery(id+"F0.wireOp",EDGE,"E3.13.0.0");var subQ2=makeQuery(id+"F0.imprint","INTERSECT",VERTEX,{"derivedFrom":[subQ1,subQ0]});Q53=makeQuery(id+"F0.imprint","IMPRINT",FACE,{"disambiguationData":[TD([[makeQuery(id+"F0.imprint","IMPRINT",EDGE,{"disambiguationData":[TD([[subQ2,-1.0]])],"derivedFrom":subQ1}),1.0]])]});}
            var Q54;
            {var subQ0=sQuery(id+"F0.wireOp",EDGE,"E10.3.23.0");var subQ1=sQuery(id+"F0.wireOp",EDGE,"E3.13.0.0");var subQ2=makeQuery(id+"F0.imprint","INTERSECT",VERTEX,{"derivedFrom":[subQ1,subQ0]});Q54=makeQuery(id+"F0.imprint","IMPRINT",FACE,{"disambiguationData":[TD([[makeQuery(id+"F0.imprint","IMPRINT",EDGE,{"disambiguationData":[TD([[subQ2,-1.0]])],"derivedFrom":subQ1}),1.0]])]});}
            var Q55;
            {var subQ0=sQuery(id+"F0.wireOp",EDGE,"E10.0.24.0");var subQ1=sQuery(id+"F0.wireOp",EDGE,"E3.13.0.0");var subQ2=makeQuery(id+"F0.imprint","INTERSECT",VERTEX,{"derivedFrom":[subQ1,subQ0]});Q55=makeQuery(id+"F0.imprint","IMPRINT",FACE,{"disambiguationData":[TD([[makeQuery(id+"F0.imprint","IMPRINT",EDGE,{"disambiguationData":[TD([[subQ2,-1.0]])],"derivedFrom":subQ1}),1.0]])]});}
            var Q56;
            {var subQ0=sQuery(id+"F0.wireOp",EDGE,"E10.0.24.0");var subQ1=sQuery(id+"F0.wireOp",EDGE,"E3.12.0.1");var subQ2=makeQuery(id+"F0.imprint","INTERSECT",VERTEX,{"derivedFrom":[subQ1,subQ0]});Q56=makeQuery(id+"F0.imprint","IMPRINT",FACE,{"disambiguationData":[TD([[makeQuery(id+"F0.imprint","IMPRINT",EDGE,{"disambiguationData":[TD([[subQ2,-1.0]])],"derivedFrom":subQ1}),1.0]])]});}
            var Q57;
            {var subQ0=sQuery(id+"F0.wireOp",EDGE,"E10.0.24.0");var subQ1=sQuery(id+"F0.wireOp",EDGE,"E3.12.0.0");var subQ2=makeQuery(id+"F0.imprint","INTERSECT",VERTEX,{"derivedFrom":[subQ1,subQ0]});Q57=makeQuery(id+"F0.imprint","IMPRINT",FACE,{"disambiguationData":[TD([[makeQuery(id+"F0.imprint","IMPRINT",EDGE,{"disambiguationData":[TD([[subQ2,-1.0]])],"derivedFrom":subQ1}),1.0]])]});}
            var Q58;
            {var subQ0=sQuery(id+"F0.wireOp",EDGE,"E10.0.23.0");var subQ1=sQuery(id+"F0.wireOp",EDGE,"E3.12.0.0");var subQ2=makeQuery(id+"F0.imprint","INTERSECT",VERTEX,{"derivedFrom":[subQ1,subQ0]});Q58=makeQuery(id+"F0.imprint","IMPRINT",FACE,{"disambiguationData":[TD([[makeQuery(id+"F0.imprint","IMPRINT",EDGE,{"disambiguationData":[TD([[subQ2,-1.0]])],"derivedFrom":subQ1}),1.0]])]});}
            var Q59;
            {var subQ0=sQuery(id+"F0.wireOp",EDGE,"E10.0.23.0");var subQ1=sQuery(id+"F0.wireOp",EDGE,"E3.12.0.1");var subQ2=makeQuery(id+"F0.imprint","INTERSECT",VERTEX,{"derivedFrom":[subQ1,subQ0]});Q59=makeQuery(id+"F0.imprint","IMPRINT",FACE,{"disambiguationData":[TD([[makeQuery(id+"F0.imprint","IMPRINT",EDGE,{"disambiguationData":[TD([[subQ2,-1.0]])],"derivedFrom":subQ1}),1.0]])]});}
            var Q60;
            {var subQ0=sQuery(id+"F0.wireOp",EDGE,"E10.0.22.0");var subQ1=sQuery(id+"F0.wireOp",EDGE,"E3.12.0.0");var subQ2=makeQuery(id+"F0.imprint","INTERSECT",VERTEX,{"derivedFrom":[subQ1,subQ0]});Q60=makeQuery(id+"F0.imprint","IMPRINT",FACE,{"disambiguationData":[TD([[makeQuery(id+"F0.imprint","IMPRINT",EDGE,{"disambiguationData":[TD([[subQ2,-1.0]])],"derivedFrom":subQ1}),1.0]])]});}
            var Q61;
            {var subQ0=sQuery(id+"F0.wireOp",EDGE,"E10.0.22.0");var subQ1=sQuery(id+"F0.wireOp",EDGE,"E3.12.0.1");var subQ2=makeQuery(id+"F0.imprint","INTERSECT",VERTEX,{"derivedFrom":[subQ1,subQ0]});Q61=makeQuery(id+"F0.imprint","IMPRINT",FACE,{"disambiguationData":[TD([[makeQuery(id+"F0.imprint","IMPRINT",EDGE,{"disambiguationData":[TD([[subQ2,-1.0]])],"derivedFrom":subQ1}),1.0]])]});}
            var Q62;
            {var subQ0=sQuery(id+"F0.wireOp",EDGE,"E10.0.21.0");var subQ1=sQuery(id+"F0.wireOp",EDGE,"E3.12.0.0");var subQ2=makeQuery(id+"F0.imprint","INTERSECT",VERTEX,{"derivedFrom":[subQ1,subQ0]});Q62=makeQuery(id+"F0.imprint","IMPRINT",FACE,{"disambiguationData":[TD([[makeQuery(id+"F0.imprint","IMPRINT",EDGE,{"disambiguationData":[TD([[subQ2,-1.0]])],"derivedFrom":subQ1}),1.0]])]});}
            var Q63;
            {var subQ0=sQuery(id+"F0.wireOp",EDGE,"E10.0.21.0");var subQ1=sQuery(id+"F0.wireOp",EDGE,"E3.12.0.1");var subQ2=makeQuery(id+"F0.imprint","INTERSECT",VERTEX,{"derivedFrom":[subQ1,subQ0]});Q63=makeQuery(id+"F0.imprint","IMPRINT",FACE,{"disambiguationData":[TD([[makeQuery(id+"F0.imprint","IMPRINT",EDGE,{"disambiguationData":[TD([[subQ2,-1.0]])],"derivedFrom":subQ1}),1.0]])]});}
            var Q64;
            {var subQ0=sQuery(id+"F0.wireOp",EDGE,"E10.0.20.0");var subQ1=sQuery(id+"F0.wireOp",EDGE,"E3.12.0.0");var subQ2=makeQuery(id+"F0.imprint","INTERSECT",VERTEX,{"derivedFrom":[subQ1,subQ0]});Q64=makeQuery(id+"F0.imprint","IMPRINT",FACE,{"disambiguationData":[TD([[makeQuery(id+"F0.imprint","IMPRINT",EDGE,{"disambiguationData":[TD([[subQ2,-1.0]])],"derivedFrom":subQ1}),1.0]])]});}
            var Q65;
            {var subQ0=sQuery(id+"F0.wireOp",EDGE,"E10.0.20.0");var subQ1=sQuery(id+"F0.wireOp",EDGE,"E3.12.0.1");var subQ2=makeQuery(id+"F0.imprint","INTERSECT",VERTEX,{"derivedFrom":[subQ1,subQ0]});Q65=makeQuery(id+"F0.imprint","IMPRINT",FACE,{"disambiguationData":[TD([[makeQuery(id+"F0.imprint","IMPRINT",EDGE,{"disambiguationData":[TD([[subQ2,-1.0]])],"derivedFrom":subQ1}),1.0]])]});}
            var Q66;
            {var subQ0=sQuery(id+"F0.wireOp",EDGE,"E10.0.19.0");var subQ1=sQuery(id+"F0.wireOp",EDGE,"E3.12.0.0");var subQ2=makeQuery(id+"F0.imprint","INTERSECT",VERTEX,{"derivedFrom":[subQ1,subQ0]});Q66=makeQuery(id+"F0.imprint","IMPRINT",FACE,{"disambiguationData":[TD([[makeQuery(id+"F0.imprint","IMPRINT",EDGE,{"disambiguationData":[TD([[subQ2,-1.0]])],"derivedFrom":subQ1}),1.0]])]});}
            var Q67;
            {var subQ0=sQuery(id+"F0.wireOp",EDGE,"E10.0.19.0");var subQ1=sQuery(id+"F0.wireOp",EDGE,"E3.12.0.1");var subQ2=makeQuery(id+"F0.imprint","INTERSECT",VERTEX,{"derivedFrom":[subQ1,subQ0]});Q67=makeQuery(id+"F0.imprint","IMPRINT",FACE,{"disambiguationData":[TD([[makeQuery(id+"F0.imprint","IMPRINT",EDGE,{"disambiguationData":[TD([[subQ2,-1.0]])],"derivedFrom":subQ1}),1.0]])]});}
            var Q68;
            {var subQ0=sQuery(id+"F0.wireOp",EDGE,"E10.0.10.0");var subQ1=sQuery(id+"F0.wireOp",EDGE,"E3.15.0.0");var subQ2=makeQuery(id+"F0.imprint","INTERSECT",VERTEX,{"derivedFrom":[subQ1,subQ0]});Q68=makeQuery(id+"F0.imprint","IMPRINT",FACE,{"disambiguationData":[TD([[makeQuery(id+"F0.imprint","IMPRINT",EDGE,{"disambiguationData":[TD([[subQ2,-1.0]])],"derivedFrom":subQ1}),1.0]])]});}
            var Q69;
            {var subQ0=sQuery(id+"F0.wireOp",EDGE,"E10.0.10.0");var subQ1=sQuery(id+"F0.wireOp",EDGE,"E3.15.0.1");var subQ2=makeQuery(id+"F0.imprint","INTERSECT",VERTEX,{"derivedFrom":[subQ1,subQ0]});Q69=makeQuery(id+"F0.imprint","IMPRINT",FACE,{"disambiguationData":[TD([[makeQuery(id+"F0.imprint","IMPRINT",EDGE,{"disambiguationData":[TD([[subQ2,-1.0]])],"derivedFrom":subQ1}),1.0]])]});}
            var Q70;
            {var subQ0=sQuery(id+"F0.wireOp",EDGE,"E10.0.10.0");var subQ1=sQuery(id+"F0.wireOp",EDGE,"E3.16.0.0");var subQ2=makeQuery(id+"F0.imprint","INTERSECT",VERTEX,{"derivedFrom":[subQ1,subQ0]});Q70=makeQuery(id+"F0.imprint","IMPRINT",FACE,{"disambiguationData":[TD([[makeQuery(id+"F0.imprint","IMPRINT",EDGE,{"disambiguationData":[TD([[subQ2,-1.0]])],"derivedFrom":subQ1}),1.0]])]});}
            var Q71;
            {var subQ0=sQuery(id+"F0.wireOp",EDGE,"E10.0.10.0");var subQ1=sQuery(id+"F0.wireOp",EDGE,"E3.16.0.1");var subQ2=makeQuery(id+"F0.imprint","INTERSECT",VERTEX,{"derivedFrom":[subQ1,subQ0]});Q71=makeQuery(id+"F0.imprint","IMPRINT",FACE,{"disambiguationData":[TD([[makeQuery(id+"F0.imprint","IMPRINT",EDGE,{"disambiguationData":[TD([[subQ2,-1.0]])],"derivedFrom":subQ1}),1.0]])]});}
            var Q72;
            {var subQ0=sQuery(id+"F0.wireOp",EDGE,"E10.0.10.0");var subQ1=sQuery(id+"F0.wireOp",EDGE,"E3.17.0.0");var subQ2=makeQuery(id+"F0.imprint","INTERSECT",VERTEX,{"derivedFrom":[subQ1,subQ0]});Q72=makeQuery(id+"F0.imprint","IMPRINT",FACE,{"disambiguationData":[TD([[makeQuery(id+"F0.imprint","IMPRINT",EDGE,{"disambiguationData":[TD([[subQ2,-1.0]])],"derivedFrom":subQ1}),1.0]])]});}
            var Q73;
            {var subQ0=sQuery(id+"F0.wireOp",EDGE,"E10.3.10.0");var subQ1=sQuery(id+"F0.wireOp",EDGE,"E3.17.0.0");var subQ2=makeQuery(id+"F0.imprint","INTERSECT",VERTEX,{"derivedFrom":[subQ1,subQ0]});Q73=makeQuery(id+"F0.imprint","IMPRINT",FACE,{"disambiguationData":[TD([[makeQuery(id+"F0.imprint","IMPRINT",EDGE,{"disambiguationData":[TD([[subQ2,-1.0]])],"derivedFrom":subQ1}),1.0]])]});}
            var Q74;
            {var subQ0=sQuery(id+"F0.wireOp",EDGE,"E10.0.11.0");var subQ1=sQuery(id+"F0.wireOp",EDGE,"E3.17.0.0");var subQ2=makeQuery(id+"F0.imprint","INTERSECT",VERTEX,{"derivedFrom":[subQ1,subQ0]});Q74=makeQuery(id+"F0.imprint","IMPRINT",FACE,{"disambiguationData":[TD([[makeQuery(id+"F0.imprint","IMPRINT",EDGE,{"disambiguationData":[TD([[subQ2,-1.0]])],"derivedFrom":subQ1}),1.0]])]});}
            var Q75;
            {var subQ0=sQuery(id+"F0.wireOp",EDGE,"E10.3.11.0");var subQ1=sQuery(id+"F0.wireOp",EDGE,"E3.17.0.0");var subQ2=makeQuery(id+"F0.imprint","INTERSECT",VERTEX,{"derivedFrom":[subQ1,subQ0]});Q75=makeQuery(id+"F0.imprint","IMPRINT",FACE,{"disambiguationData":[TD([[makeQuery(id+"F0.imprint","IMPRINT",EDGE,{"disambiguationData":[TD([[subQ2,-1.0]])],"derivedFrom":subQ1}),1.0]])]});}
            var Q76;
            {var subQ0=sQuery(id+"F0.wireOp",EDGE,"E10.0.12.0");var subQ1=sQuery(id+"F0.wireOp",EDGE,"E3.17.0.0");var subQ2=makeQuery(id+"F0.imprint","INTERSECT",VERTEX,{"derivedFrom":[subQ1,subQ0]});Q76=makeQuery(id+"F0.imprint","IMPRINT",FACE,{"disambiguationData":[TD([[makeQuery(id+"F0.imprint","IMPRINT",EDGE,{"disambiguationData":[TD([[subQ2,-1.0]])],"derivedFrom":subQ1}),1.0]])]});}
            var Q77;
            {var subQ0=sQuery(id+"F0.wireOp",EDGE,"E10.3.12.0");var subQ1=sQuery(id+"F0.wireOp",EDGE,"E3.17.0.0");var subQ2=makeQuery(id+"F0.imprint","INTERSECT",VERTEX,{"derivedFrom":[subQ1,subQ0]});Q77=makeQuery(id+"F0.imprint","IMPRINT",FACE,{"disambiguationData":[TD([[makeQuery(id+"F0.imprint","IMPRINT",EDGE,{"disambiguationData":[TD([[subQ2,-1.0]])],"derivedFrom":subQ1}),1.0]])]});}
            var Q78;
            {var subQ0=sQuery(id+"F0.wireOp",EDGE,"E10.0.13.0");var subQ1=sQuery(id+"F0.wireOp",EDGE,"E3.17.0.0");var subQ2=makeQuery(id+"F0.imprint","INTERSECT",VERTEX,{"derivedFrom":[subQ1,subQ0]});Q78=makeQuery(id+"F0.imprint","IMPRINT",FACE,{"disambiguationData":[TD([[makeQuery(id+"F0.imprint","IMPRINT",EDGE,{"disambiguationData":[TD([[subQ2,-1.0]])],"derivedFrom":subQ1}),1.0]])]});}
            var Q79;
            {var subQ0=sQuery(id+"F0.wireOp",EDGE,"E10.3.13.0");var subQ1=sQuery(id+"F0.wireOp",EDGE,"E3.17.0.0");var subQ2=makeQuery(id+"F0.imprint","INTERSECT",VERTEX,{"derivedFrom":[subQ1,subQ0]});Q79=makeQuery(id+"F0.imprint","IMPRINT",FACE,{"disambiguationData":[TD([[makeQuery(id+"F0.imprint","IMPRINT",EDGE,{"disambiguationData":[TD([[subQ2,-1.0]])],"derivedFrom":subQ1}),1.0]])]});}
            var Q80;
            {var subQ0=sQuery(id+"F0.wireOp",EDGE,"E10.0.14.0");var subQ1=sQuery(id+"F0.wireOp",EDGE,"E3.17.0.0");var subQ2=makeQuery(id+"F0.imprint","INTERSECT",VERTEX,{"derivedFrom":[subQ1,subQ0]});Q80=makeQuery(id+"F0.imprint","IMPRINT",FACE,{"disambiguationData":[TD([[makeQuery(id+"F0.imprint","IMPRINT",EDGE,{"disambiguationData":[TD([[subQ2,-1.0]])],"derivedFrom":subQ1}),1.0]])]});}
            var Q81;
            {var subQ0=sQuery(id+"F0.wireOp",EDGE,"E10.3.14.0");var subQ1=sQuery(id+"F0.wireOp",EDGE,"E3.17.0.0");var subQ2=makeQuery(id+"F0.imprint","INTERSECT",VERTEX,{"derivedFrom":[subQ1,subQ0]});Q81=makeQuery(id+"F0.imprint","IMPRINT",FACE,{"disambiguationData":[TD([[makeQuery(id+"F0.imprint","IMPRINT",EDGE,{"disambiguationData":[TD([[subQ2,-1.0]])],"derivedFrom":subQ1}),1.0]])]});}
            var Q82;
            {var subQ0=sQuery(id+"F0.wireOp",EDGE,"E10.0.15.0");var subQ1=sQuery(id+"F0.wireOp",EDGE,"E3.17.0.0");var subQ2=makeQuery(id+"F0.imprint","INTERSECT",VERTEX,{"derivedFrom":[subQ1,subQ0]});Q82=makeQuery(id+"F0.imprint","IMPRINT",FACE,{"disambiguationData":[TD([[makeQuery(id+"F0.imprint","IMPRINT",EDGE,{"disambiguationData":[TD([[subQ2,-1.0]])],"derivedFrom":subQ1}),1.0]])]});}
            var Q83;
            {var subQ0=sQuery(id+"F0.wireOp",EDGE,"E10.3.15.0");var subQ1=sQuery(id+"F0.wireOp",EDGE,"E3.17.0.0");var subQ2=makeQuery(id+"F0.imprint","INTERSECT",VERTEX,{"derivedFrom":[subQ1,subQ0]});Q83=makeQuery(id+"F0.imprint","IMPRINT",FACE,{"disambiguationData":[TD([[makeQuery(id+"F0.imprint","IMPRINT",EDGE,{"disambiguationData":[TD([[subQ2,-1.0]])],"derivedFrom":subQ1}),1.0]])]});}
            var Q84;
            {var subQ0=sQuery(id+"F0.wireOp",EDGE,"E10.0.16.0");var subQ1=sQuery(id+"F0.wireOp",EDGE,"E3.17.0.0");var subQ2=makeQuery(id+"F0.imprint","INTERSECT",VERTEX,{"derivedFrom":[subQ1,subQ0]});Q84=makeQuery(id+"F0.imprint","IMPRINT",FACE,{"disambiguationData":[TD([[makeQuery(id+"F0.imprint","IMPRINT",EDGE,{"disambiguationData":[TD([[subQ2,-1.0]])],"derivedFrom":subQ1}),1.0]])]});}
            var Q85;
            {var subQ0=sQuery(id+"F0.wireOp",EDGE,"E10.0.24.0");var subQ1=sQuery(id+"F0.wireOp",EDGE,"E3.15.0.0");var subQ2=makeQuery(id+"F0.imprint","INTERSECT",VERTEX,{"derivedFrom":[subQ1,subQ0]});Q85=makeQuery(id+"F0.imprint","IMPRINT",FACE,{"disambiguationData":[TD([[makeQuery(id+"F0.imprint","IMPRINT",EDGE,{"disambiguationData":[TD([[subQ2,-1.0]])],"derivedFrom":subQ1}),1.0]])]});}
            var Q86;
            {var subQ0=sQuery(id+"F0.wireOp",EDGE,"E10.0.24.0");var subQ1=sQuery(id+"F0.wireOp",EDGE,"E3.14.0.1");var subQ2=makeQuery(id+"F0.imprint","INTERSECT",VERTEX,{"derivedFrom":[subQ1,subQ0]});Q86=makeQuery(id+"F0.imprint","IMPRINT",FACE,{"disambiguationData":[TD([[makeQuery(id+"F0.imprint","IMPRINT",EDGE,{"disambiguationData":[TD([[subQ2,-1.0]])],"derivedFrom":subQ1}),1.0]])]});}
            var Q87;
            {var subQ0=sQuery(id+"F0.wireOp",EDGE,"E10.0.24.0");var subQ1=sQuery(id+"F0.wireOp",EDGE,"E3.14.0.0");var subQ2=makeQuery(id+"F0.imprint","INTERSECT",VERTEX,{"derivedFrom":[subQ1,subQ0]});Q87=makeQuery(id+"F0.imprint","IMPRINT",FACE,{"disambiguationData":[TD([[makeQuery(id+"F0.imprint","IMPRINT",EDGE,{"disambiguationData":[TD([[subQ2,-1.0]])],"derivedFrom":subQ1}),1.0]])]});}
            var Q88;
            {var subQ0=sQuery(id+"F0.wireOp",EDGE,"E10.3.23.0");var subQ1=sQuery(id+"F0.wireOp",EDGE,"E3.14.0.0");var subQ2=makeQuery(id+"F0.imprint","INTERSECT",VERTEX,{"derivedFrom":[subQ1,subQ0]});Q88=makeQuery(id+"F0.imprint","IMPRINT",FACE,{"disambiguationData":[TD([[makeQuery(id+"F0.imprint","IMPRINT",EDGE,{"disambiguationData":[TD([[subQ2,-1.0]])],"derivedFrom":subQ1}),1.0]])]});}
            var Q89;
            {var subQ0=sQuery(id+"F0.wireOp",EDGE,"E10.0.23.0");var subQ1=sQuery(id+"F0.wireOp",EDGE,"E3.14.0.0");var subQ2=makeQuery(id+"F0.imprint","INTERSECT",VERTEX,{"derivedFrom":[subQ1,subQ0]});Q89=makeQuery(id+"F0.imprint","IMPRINT",FACE,{"disambiguationData":[TD([[makeQuery(id+"F0.imprint","IMPRINT",EDGE,{"disambiguationData":[TD([[subQ2,-1.0]])],"derivedFrom":subQ1}),1.0]])]});}
            var Q90;
            {var subQ0=sQuery(id+"F0.wireOp",EDGE,"E10.3.22.0");var subQ1=sQuery(id+"F0.wireOp",EDGE,"E3.14.0.0");var subQ2=makeQuery(id+"F0.imprint","INTERSECT",VERTEX,{"derivedFrom":[subQ1,subQ0]});Q90=makeQuery(id+"F0.imprint","IMPRINT",FACE,{"disambiguationData":[TD([[makeQuery(id+"F0.imprint","IMPRINT",EDGE,{"disambiguationData":[TD([[subQ2,-1.0]])],"derivedFrom":subQ1}),1.0]])]});}
            var Q91;
            {var subQ0=sQuery(id+"F0.wireOp",EDGE,"E10.0.22.0");var subQ1=sQuery(id+"F0.wireOp",EDGE,"E3.14.0.0");var subQ2=makeQuery(id+"F0.imprint","INTERSECT",VERTEX,{"derivedFrom":[subQ1,subQ0]});Q91=makeQuery(id+"F0.imprint","IMPRINT",FACE,{"disambiguationData":[TD([[makeQuery(id+"F0.imprint","IMPRINT",EDGE,{"disambiguationData":[TD([[subQ2,-1.0]])],"derivedFrom":subQ1}),1.0]])]});}
            var Q92;
            {var subQ0=sQuery(id+"F0.wireOp",EDGE,"E10.3.21.0");var subQ1=sQuery(id+"F0.wireOp",EDGE,"E3.14.0.0");var subQ2=makeQuery(id+"F0.imprint","INTERSECT",VERTEX,{"derivedFrom":[subQ1,subQ0]});Q92=makeQuery(id+"F0.imprint","IMPRINT",FACE,{"disambiguationData":[TD([[makeQuery(id+"F0.imprint","IMPRINT",EDGE,{"disambiguationData":[TD([[subQ2,-1.0]])],"derivedFrom":subQ1}),1.0]])]});}
            var Q93;
            {var subQ0=sQuery(id+"F0.wireOp",EDGE,"E10.0.21.0");var subQ1=sQuery(id+"F0.wireOp",EDGE,"E3.14.0.0");var subQ2=makeQuery(id+"F0.imprint","INTERSECT",VERTEX,{"derivedFrom":[subQ1,subQ0]});Q93=makeQuery(id+"F0.imprint","IMPRINT",FACE,{"disambiguationData":[TD([[makeQuery(id+"F0.imprint","IMPRINT",EDGE,{"disambiguationData":[TD([[subQ2,-1.0]])],"derivedFrom":subQ1}),1.0]])]});}
            var Q94;
            {var subQ0=sQuery(id+"F0.wireOp",EDGE,"E10.3.20.0");var subQ1=sQuery(id+"F0.wireOp",EDGE,"E3.14.0.0");var subQ2=makeQuery(id+"F0.imprint","INTERSECT",VERTEX,{"derivedFrom":[subQ1,subQ0]});Q94=makeQuery(id+"F0.imprint","IMPRINT",FACE,{"disambiguationData":[TD([[makeQuery(id+"F0.imprint","IMPRINT",EDGE,{"disambiguationData":[TD([[subQ2,-1.0]])],"derivedFrom":subQ1}),1.0]])]});}
            var Q95;
            {var subQ0=sQuery(id+"F0.wireOp",EDGE,"E10.0.20.0");var subQ1=sQuery(id+"F0.wireOp",EDGE,"E3.14.0.0");var subQ2=makeQuery(id+"F0.imprint","INTERSECT",VERTEX,{"derivedFrom":[subQ1,subQ0]});Q95=makeQuery(id+"F0.imprint","IMPRINT",FACE,{"disambiguationData":[TD([[makeQuery(id+"F0.imprint","IMPRINT",EDGE,{"disambiguationData":[TD([[subQ2,-1.0]])],"derivedFrom":subQ1}),1.0]])]});}
            var Q96;
            {var subQ0=sQuery(id+"F0.wireOp",EDGE,"E10.3.19.0");var subQ1=sQuery(id+"F0.wireOp",EDGE,"E3.14.0.0");var subQ2=makeQuery(id+"F0.imprint","INTERSECT",VERTEX,{"derivedFrom":[subQ1,subQ0]});Q96=makeQuery(id+"F0.imprint","IMPRINT",FACE,{"disambiguationData":[TD([[makeQuery(id+"F0.imprint","IMPRINT",EDGE,{"disambiguationData":[TD([[subQ2,-1.0]])],"derivedFrom":subQ1}),1.0]])]});}
            var Q97;
            {var subQ0=sQuery(id+"F0.wireOp",EDGE,"E10.0.19.0");var subQ1=sQuery(id+"F0.wireOp",EDGE,"E3.14.0.0");var subQ2=makeQuery(id+"F0.imprint","INTERSECT",VERTEX,{"derivedFrom":[subQ1,subQ0]});Q97=makeQuery(id+"F0.imprint","IMPRINT",FACE,{"disambiguationData":[TD([[makeQuery(id+"F0.imprint","IMPRINT",EDGE,{"disambiguationData":[TD([[subQ2,-1.0]])],"derivedFrom":subQ1}),1.0]])]});}
            var Q98;
            {var subQ0=sQuery(id+"F0.wireOp",EDGE,"E10.3.18.0");var subQ1=sQuery(id+"F0.wireOp",EDGE,"E3.14.0.0");var subQ2=makeQuery(id+"F0.imprint","INTERSECT",VERTEX,{"derivedFrom":[subQ1,subQ0]});Q98=makeQuery(id+"F0.imprint","IMPRINT",FACE,{"disambiguationData":[TD([[makeQuery(id+"F0.imprint","IMPRINT",EDGE,{"disambiguationData":[TD([[subQ2,-1.0]])],"derivedFrom":subQ1}),1.0]])]});}
            var Q99;
            {var subQ0=sQuery(id+"F0.wireOp",EDGE,"E10.0.18.0");var subQ1=sQuery(id+"F0.wireOp",EDGE,"E3.14.0.0");var subQ2=makeQuery(id+"F0.imprint","INTERSECT",VERTEX,{"derivedFrom":[subQ1,subQ0]});Q99=makeQuery(id+"F0.imprint","IMPRINT",FACE,{"disambiguationData":[TD([[makeQuery(id+"F0.imprint","IMPRINT",EDGE,{"disambiguationData":[TD([[subQ2,-1.0]])],"derivedFrom":subQ1}),1.0]])]});}
            var Q100;
            {var subQ0=sQuery(id+"F0.wireOp",EDGE,"E10.3.17.0");var subQ1=sQuery(id+"F0.wireOp",EDGE,"E3.14.0.0");var subQ2=makeQuery(id+"F0.imprint","INTERSECT",VERTEX,{"derivedFrom":[subQ1,subQ0]});Q100=makeQuery(id+"F0.imprint","IMPRINT",FACE,{"disambiguationData":[TD([[makeQuery(id+"F0.imprint","IMPRINT",EDGE,{"disambiguationData":[TD([[subQ2,-1.0]])],"derivedFrom":subQ1}),1.0]])]});}
            var Q101;
            {var subQ0=sQuery(id+"F0.wireOp",EDGE,"E10.0.17.0");var subQ1=sQuery(id+"F0.wireOp",EDGE,"E3.14.0.0");var subQ2=makeQuery(id+"F0.imprint","INTERSECT",VERTEX,{"derivedFrom":[subQ1,subQ0]});Q101=makeQuery(id+"F0.imprint","IMPRINT",FACE,{"disambiguationData":[TD([[makeQuery(id+"F0.imprint","IMPRINT",EDGE,{"disambiguationData":[TD([[subQ2,-1.0]])],"derivedFrom":subQ1}),1.0]])]});}
            var Q102;
            {var subQ0=sQuery(id+"F0.wireOp",EDGE,"E10.0.16.0");var subQ1=sQuery(id+"F0.wireOp",EDGE,"E3.14.0.0");var subQ2=makeQuery(id+"F0.imprint","INTERSECT",VERTEX,{"derivedFrom":[subQ1,subQ0]});Q102=makeQuery(id+"F0.imprint","IMPRINT",FACE,{"disambiguationData":[TD([[makeQuery(id+"F0.imprint","IMPRINT",EDGE,{"disambiguationData":[TD([[subQ2,-1.0]])],"derivedFrom":subQ1}),1.0]])]});}
            var Q103;
            {var subQ0=sQuery(id+"F0.wireOp",EDGE,"E10.3.15.0");var subQ1=sQuery(id+"F0.wireOp",EDGE,"E3.14.0.0");var subQ2=makeQuery(id+"F0.imprint","INTERSECT",VERTEX,{"derivedFrom":[subQ1,subQ0]});Q103=makeQuery(id+"F0.imprint","IMPRINT",FACE,{"disambiguationData":[TD([[makeQuery(id+"F0.imprint","IMPRINT",EDGE,{"disambiguationData":[TD([[subQ2,-1.0]])],"derivedFrom":subQ1}),1.0]])]});}
            var Q104;
            {var subQ0=sQuery(id+"F0.wireOp",EDGE,"E10.0.15.0");var subQ1=sQuery(id+"F0.wireOp",EDGE,"E3.14.0.0");var subQ2=makeQuery(id+"F0.imprint","INTERSECT",VERTEX,{"derivedFrom":[subQ1,subQ0]});Q104=makeQuery(id+"F0.imprint","IMPRINT",FACE,{"disambiguationData":[TD([[makeQuery(id+"F0.imprint","IMPRINT",EDGE,{"disambiguationData":[TD([[subQ2,-1.0]])],"derivedFrom":subQ1}),1.0]])]});}
            var Q105;
            {var subQ0=sQuery(id+"F0.wireOp",EDGE,"E10.3.14.0");var subQ1=sQuery(id+"F0.wireOp",EDGE,"E3.14.0.0");var subQ2=makeQuery(id+"F0.imprint","INTERSECT",VERTEX,{"derivedFrom":[subQ1,subQ0]});Q105=makeQuery(id+"F0.imprint","IMPRINT",FACE,{"disambiguationData":[TD([[makeQuery(id+"F0.imprint","IMPRINT",EDGE,{"disambiguationData":[TD([[subQ2,-1.0]])],"derivedFrom":subQ1}),1.0]])]});}
            var Q106;
            {var subQ0=sQuery(id+"F0.wireOp",EDGE,"E10.0.14.0");var subQ1=sQuery(id+"F0.wireOp",EDGE,"E3.14.0.0");var subQ2=makeQuery(id+"F0.imprint","INTERSECT",VERTEX,{"derivedFrom":[subQ1,subQ0]});Q106=makeQuery(id+"F0.imprint","IMPRINT",FACE,{"disambiguationData":[TD([[makeQuery(id+"F0.imprint","IMPRINT",EDGE,{"disambiguationData":[TD([[subQ2,-1.0]])],"derivedFrom":subQ1}),1.0]])]});}
            var Q107;
            {var subQ0=sQuery(id+"F0.wireOp",EDGE,"E10.3.13.0");var subQ1=sQuery(id+"F0.wireOp",EDGE,"E3.14.0.0");var subQ2=makeQuery(id+"F0.imprint","INTERSECT",VERTEX,{"derivedFrom":[subQ1,subQ0]});Q107=makeQuery(id+"F0.imprint","IMPRINT",FACE,{"disambiguationData":[TD([[makeQuery(id+"F0.imprint","IMPRINT",EDGE,{"disambiguationData":[TD([[subQ2,-1.0]])],"derivedFrom":subQ1}),1.0]])]});}
            var Q108;
            {var subQ0=sQuery(id+"F0.wireOp",EDGE,"E10.0.13.0");var subQ1=sQuery(id+"F0.wireOp",EDGE,"E3.14.0.0");var subQ2=makeQuery(id+"F0.imprint","INTERSECT",VERTEX,{"derivedFrom":[subQ1,subQ0]});Q108=makeQuery(id+"F0.imprint","IMPRINT",FACE,{"disambiguationData":[TD([[makeQuery(id+"F0.imprint","IMPRINT",EDGE,{"disambiguationData":[TD([[subQ2,-1.0]])],"derivedFrom":subQ1}),1.0]])]});}
            var Q109;
            {var subQ0=sQuery(id+"F0.wireOp",EDGE,"E10.3.12.0");var subQ1=sQuery(id+"F0.wireOp",EDGE,"E3.14.0.0");var subQ2=makeQuery(id+"F0.imprint","INTERSECT",VERTEX,{"derivedFrom":[subQ1,subQ0]});Q109=makeQuery(id+"F0.imprint","IMPRINT",FACE,{"disambiguationData":[TD([[makeQuery(id+"F0.imprint","IMPRINT",EDGE,{"disambiguationData":[TD([[subQ2,-1.0]])],"derivedFrom":subQ1}),1.0]])]});}
            var Q110;
            {var subQ0=sQuery(id+"F0.wireOp",EDGE,"E10.0.12.0");var subQ1=sQuery(id+"F0.wireOp",EDGE,"E3.14.0.0");var subQ2=makeQuery(id+"F0.imprint","INTERSECT",VERTEX,{"derivedFrom":[subQ1,subQ0]});Q110=makeQuery(id+"F0.imprint","IMPRINT",FACE,{"disambiguationData":[TD([[makeQuery(id+"F0.imprint","IMPRINT",EDGE,{"disambiguationData":[TD([[subQ2,-1.0]])],"derivedFrom":subQ1}),1.0]])]});}
            var Q111;
            {var subQ0=sQuery(id+"F0.wireOp",EDGE,"E10.3.11.0");var subQ1=sQuery(id+"F0.wireOp",EDGE,"E3.14.0.0");var subQ2=makeQuery(id+"F0.imprint","INTERSECT",VERTEX,{"derivedFrom":[subQ1,subQ0]});Q111=makeQuery(id+"F0.imprint","IMPRINT",FACE,{"disambiguationData":[TD([[makeQuery(id+"F0.imprint","IMPRINT",EDGE,{"disambiguationData":[TD([[subQ2,-1.0]])],"derivedFrom":subQ1}),1.0]])]});}
            var Q112;
            {var subQ0=sQuery(id+"F0.wireOp",EDGE,"E10.0.11.0");var subQ1=sQuery(id+"F0.wireOp",EDGE,"E3.14.0.0");var subQ2=makeQuery(id+"F0.imprint","INTERSECT",VERTEX,{"derivedFrom":[subQ1,subQ0]});Q112=makeQuery(id+"F0.imprint","IMPRINT",FACE,{"disambiguationData":[TD([[makeQuery(id+"F0.imprint","IMPRINT",EDGE,{"disambiguationData":[TD([[subQ2,-1.0]])],"derivedFrom":subQ1}),1.0]])]});}
            var Q113;
            {var subQ0=sQuery(id+"F0.wireOp",EDGE,"E10.3.10.0");var subQ1=sQuery(id+"F0.wireOp",EDGE,"E3.14.0.0");var subQ2=makeQuery(id+"F0.imprint","INTERSECT",VERTEX,{"derivedFrom":[subQ1,subQ0]});Q113=makeQuery(id+"F0.imprint","IMPRINT",FACE,{"disambiguationData":[TD([[makeQuery(id+"F0.imprint","IMPRINT",EDGE,{"disambiguationData":[TD([[subQ2,-1.0]])],"derivedFrom":subQ1}),1.0]])]});}
            var Q114;
            {var subQ0=sQuery(id+"F0.wireOp",EDGE,"E10.0.10.0");var subQ1=sQuery(id+"F0.wireOp",EDGE,"E3.14.0.0");var subQ2=makeQuery(id+"F0.imprint","INTERSECT",VERTEX,{"derivedFrom":[subQ1,subQ0]});Q114=makeQuery(id+"F0.imprint","IMPRINT",FACE,{"disambiguationData":[TD([[makeQuery(id+"F0.imprint","IMPRINT",EDGE,{"disambiguationData":[TD([[subQ2,-1.0]])],"derivedFrom":subQ1}),1.0]])]});}
            var Q115;
            {var subQ0=sQuery(id+"F0.wireOp",EDGE,"E10.0.10.0");var subQ1=sQuery(id+"F0.wireOp",EDGE,"E3.14.0.1");var subQ2=makeQuery(id+"F0.imprint","INTERSECT",VERTEX,{"derivedFrom":[subQ1,subQ0]});Q115=makeQuery(id+"F0.imprint","IMPRINT",FACE,{"disambiguationData":[TD([[makeQuery(id+"F0.imprint","IMPRINT",EDGE,{"disambiguationData":[TD([[subQ2,-1.0]])],"derivedFrom":subQ1}),1.0]])]});}
            var Q116;
            {var subQ0=sQuery(id+"F0.wireOp",EDGE,"E10.0.11.0");var subQ1=sQuery(id+"F0.wireOp",EDGE,"E3.14.0.1");var subQ2=makeQuery(id+"F0.imprint","INTERSECT",VERTEX,{"derivedFrom":[subQ1,subQ0]});Q116=makeQuery(id+"F0.imprint","IMPRINT",FACE,{"disambiguationData":[TD([[makeQuery(id+"F0.imprint","IMPRINT",EDGE,{"disambiguationData":[TD([[subQ2,-1.0]])],"derivedFrom":subQ1}),1.0]])]});}
            var Q117;
            {var subQ0=sQuery(id+"F0.wireOp",EDGE,"E10.0.11.0");var subQ1=sQuery(id+"F0.wireOp",EDGE,"E3.15.0.0");var subQ2=makeQuery(id+"F0.imprint","INTERSECT",VERTEX,{"derivedFrom":[subQ1,subQ0]});Q117=makeQuery(id+"F0.imprint","IMPRINT",FACE,{"disambiguationData":[TD([[makeQuery(id+"F0.imprint","IMPRINT",EDGE,{"disambiguationData":[TD([[subQ2,-1.0]])],"derivedFrom":subQ1}),1.0]])]});}
            var Q118;
            {var subQ0=sQuery(id+"F0.wireOp",EDGE,"E10.0.11.0");var subQ1=sQuery(id+"F0.wireOp",EDGE,"E3.15.0.1");var subQ2=makeQuery(id+"F0.imprint","INTERSECT",VERTEX,{"derivedFrom":[subQ1,subQ0]});Q118=makeQuery(id+"F0.imprint","IMPRINT",FACE,{"disambiguationData":[TD([[makeQuery(id+"F0.imprint","IMPRINT",EDGE,{"disambiguationData":[TD([[subQ2,-1.0]])],"derivedFrom":subQ1}),1.0]])]});}
            var Q119;
            {var subQ0=sQuery(id+"F0.wireOp",EDGE,"E10.0.11.0");var subQ1=sQuery(id+"F0.wireOp",EDGE,"E3.16.0.0");var subQ2=makeQuery(id+"F0.imprint","INTERSECT",VERTEX,{"derivedFrom":[subQ1,subQ0]});Q119=makeQuery(id+"F0.imprint","IMPRINT",FACE,{"disambiguationData":[TD([[makeQuery(id+"F0.imprint","IMPRINT",EDGE,{"disambiguationData":[TD([[subQ2,-1.0]])],"derivedFrom":subQ1}),1.0]])]});}
            var Q120;
            {var subQ0=sQuery(id+"F0.wireOp",EDGE,"E10.0.11.0");var subQ1=sQuery(id+"F0.wireOp",EDGE,"E3.16.0.1");var subQ2=makeQuery(id+"F0.imprint","INTERSECT",VERTEX,{"derivedFrom":[subQ1,subQ0]});Q120=makeQuery(id+"F0.imprint","IMPRINT",FACE,{"disambiguationData":[TD([[makeQuery(id+"F0.imprint","IMPRINT",EDGE,{"disambiguationData":[TD([[subQ2,-1.0]])],"derivedFrom":subQ1}),1.0]])]});}
            var Q121;
            {var subQ0=sQuery(id+"F0.wireOp",EDGE,"E10.0.12.0");var subQ1=sQuery(id+"F0.wireOp",EDGE,"E3.14.0.1");var subQ2=makeQuery(id+"F0.imprint","INTERSECT",VERTEX,{"derivedFrom":[subQ1,subQ0]});Q121=makeQuery(id+"F0.imprint","IMPRINT",FACE,{"disambiguationData":[TD([[makeQuery(id+"F0.imprint","IMPRINT",EDGE,{"disambiguationData":[TD([[subQ2,-1.0]])],"derivedFrom":subQ1}),1.0]])]});}
            var Q122;
            {var subQ0=sQuery(id+"F0.wireOp",EDGE,"E10.0.12.0");var subQ1=sQuery(id+"F0.wireOp",EDGE,"E3.15.0.0");var subQ2=makeQuery(id+"F0.imprint","INTERSECT",VERTEX,{"derivedFrom":[subQ1,subQ0]});Q122=makeQuery(id+"F0.imprint","IMPRINT",FACE,{"disambiguationData":[TD([[makeQuery(id+"F0.imprint","IMPRINT",EDGE,{"disambiguationData":[TD([[subQ2,-1.0]])],"derivedFrom":subQ1}),1.0]])]});}
            var Q123;
            {var subQ0=sQuery(id+"F0.wireOp",EDGE,"E10.0.12.0");var subQ1=sQuery(id+"F0.wireOp",EDGE,"E3.15.0.1");var subQ2=makeQuery(id+"F0.imprint","INTERSECT",VERTEX,{"derivedFrom":[subQ1,subQ0]});Q123=makeQuery(id+"F0.imprint","IMPRINT",FACE,{"disambiguationData":[TD([[makeQuery(id+"F0.imprint","IMPRINT",EDGE,{"disambiguationData":[TD([[subQ2,-1.0]])],"derivedFrom":subQ1}),1.0]])]});}
            var Q124;
            {var subQ0=sQuery(id+"F0.wireOp",EDGE,"E10.0.12.0");var subQ1=sQuery(id+"F0.wireOp",EDGE,"E3.16.0.0");var subQ2=makeQuery(id+"F0.imprint","INTERSECT",VERTEX,{"derivedFrom":[subQ1,subQ0]});Q124=makeQuery(id+"F0.imprint","IMPRINT",FACE,{"disambiguationData":[TD([[makeQuery(id+"F0.imprint","IMPRINT",EDGE,{"disambiguationData":[TD([[subQ2,-1.0]])],"derivedFrom":subQ1}),1.0]])]});}
            var Q125;
            {var subQ0=sQuery(id+"F0.wireOp",EDGE,"E10.0.12.0");var subQ1=sQuery(id+"F0.wireOp",EDGE,"E3.16.0.1");var subQ2=makeQuery(id+"F0.imprint","INTERSECT",VERTEX,{"derivedFrom":[subQ1,subQ0]});Q125=makeQuery(id+"F0.imprint","IMPRINT",FACE,{"disambiguationData":[TD([[makeQuery(id+"F0.imprint","IMPRINT",EDGE,{"disambiguationData":[TD([[subQ2,-1.0]])],"derivedFrom":subQ1}),1.0]])]});}
            var Q126;
            {var subQ0=sQuery(id+"F0.wireOp",EDGE,"E10.0.13.0");var subQ1=sQuery(id+"F0.wireOp",EDGE,"E3.14.0.1");var subQ2=makeQuery(id+"F0.imprint","INTERSECT",VERTEX,{"derivedFrom":[subQ1,subQ0]});Q126=makeQuery(id+"F0.imprint","IMPRINT",FACE,{"disambiguationData":[TD([[makeQuery(id+"F0.imprint","IMPRINT",EDGE,{"disambiguationData":[TD([[subQ2,-1.0]])],"derivedFrom":subQ1}),1.0]])]});}
            var Q127;
            {var subQ0=sQuery(id+"F0.wireOp",EDGE,"E10.0.13.0");var subQ1=sQuery(id+"F0.wireOp",EDGE,"E3.15.0.0");var subQ2=makeQuery(id+"F0.imprint","INTERSECT",VERTEX,{"derivedFrom":[subQ1,subQ0]});Q127=makeQuery(id+"F0.imprint","IMPRINT",FACE,{"disambiguationData":[TD([[makeQuery(id+"F0.imprint","IMPRINT",EDGE,{"disambiguationData":[TD([[subQ2,-1.0]])],"derivedFrom":subQ1}),1.0]])]});}
            var Q128;
            {var subQ0=sQuery(id+"F0.wireOp",EDGE,"E10.0.13.0");var subQ1=sQuery(id+"F0.wireOp",EDGE,"E3.15.0.1");var subQ2=makeQuery(id+"F0.imprint","INTERSECT",VERTEX,{"derivedFrom":[subQ1,subQ0]});Q128=makeQuery(id+"F0.imprint","IMPRINT",FACE,{"disambiguationData":[TD([[makeQuery(id+"F0.imprint","IMPRINT",EDGE,{"disambiguationData":[TD([[subQ2,-1.0]])],"derivedFrom":subQ1}),1.0]])]});}
            var Q129;
            {var subQ0=sQuery(id+"F0.wireOp",EDGE,"E10.0.13.0");var subQ1=sQuery(id+"F0.wireOp",EDGE,"E3.16.0.0");var subQ2=makeQuery(id+"F0.imprint","INTERSECT",VERTEX,{"derivedFrom":[subQ1,subQ0]});Q129=makeQuery(id+"F0.imprint","IMPRINT",FACE,{"disambiguationData":[TD([[makeQuery(id+"F0.imprint","IMPRINT",EDGE,{"disambiguationData":[TD([[subQ2,-1.0]])],"derivedFrom":subQ1}),1.0]])]});}
            var Q130;
            {var subQ0=sQuery(id+"F0.wireOp",EDGE,"E10.0.13.0");var subQ1=sQuery(id+"F0.wireOp",EDGE,"E3.16.0.1");var subQ2=makeQuery(id+"F0.imprint","INTERSECT",VERTEX,{"derivedFrom":[subQ1,subQ0]});Q130=makeQuery(id+"F0.imprint","IMPRINT",FACE,{"disambiguationData":[TD([[makeQuery(id+"F0.imprint","IMPRINT",EDGE,{"disambiguationData":[TD([[subQ2,-1.0]])],"derivedFrom":subQ1}),1.0]])]});}
            var Q131;
            {var subQ0=sQuery(id+"F0.wireOp",EDGE,"E10.0.14.0");var subQ1=sQuery(id+"F0.wireOp",EDGE,"E3.14.0.1");var subQ2=makeQuery(id+"F0.imprint","INTERSECT",VERTEX,{"derivedFrom":[subQ1,subQ0]});Q131=makeQuery(id+"F0.imprint","IMPRINT",FACE,{"disambiguationData":[TD([[makeQuery(id+"F0.imprint","IMPRINT",EDGE,{"disambiguationData":[TD([[subQ2,-1.0]])],"derivedFrom":subQ1}),1.0]])]});}
            var Q132;
            {var subQ0=sQuery(id+"F0.wireOp",EDGE,"E10.0.14.0");var subQ1=sQuery(id+"F0.wireOp",EDGE,"E3.15.0.0");var subQ2=makeQuery(id+"F0.imprint","INTERSECT",VERTEX,{"derivedFrom":[subQ1,subQ0]});Q132=makeQuery(id+"F0.imprint","IMPRINT",FACE,{"disambiguationData":[TD([[makeQuery(id+"F0.imprint","IMPRINT",EDGE,{"disambiguationData":[TD([[subQ2,-1.0]])],"derivedFrom":subQ1}),1.0]])]});}
            var Q133;
            {var subQ0=sQuery(id+"F0.wireOp",EDGE,"E10.0.14.0");var subQ1=sQuery(id+"F0.wireOp",EDGE,"E3.15.0.1");var subQ2=makeQuery(id+"F0.imprint","INTERSECT",VERTEX,{"derivedFrom":[subQ1,subQ0]});Q133=makeQuery(id+"F0.imprint","IMPRINT",FACE,{"disambiguationData":[TD([[makeQuery(id+"F0.imprint","IMPRINT",EDGE,{"disambiguationData":[TD([[subQ2,-1.0]])],"derivedFrom":subQ1}),1.0]])]});}
            var Q134;
            {var subQ0=sQuery(id+"F0.wireOp",EDGE,"E10.0.14.0");var subQ1=sQuery(id+"F0.wireOp",EDGE,"E3.16.0.0");var subQ2=makeQuery(id+"F0.imprint","INTERSECT",VERTEX,{"derivedFrom":[subQ1,subQ0]});Q134=makeQuery(id+"F0.imprint","IMPRINT",FACE,{"disambiguationData":[TD([[makeQuery(id+"F0.imprint","IMPRINT",EDGE,{"disambiguationData":[TD([[subQ2,-1.0]])],"derivedFrom":subQ1}),1.0]])]});}
            var Q135;
            {var subQ0=sQuery(id+"F0.wireOp",EDGE,"E10.0.14.0");var subQ1=sQuery(id+"F0.wireOp",EDGE,"E3.16.0.1");var subQ2=makeQuery(id+"F0.imprint","INTERSECT",VERTEX,{"derivedFrom":[subQ1,subQ0]});Q135=makeQuery(id+"F0.imprint","IMPRINT",FACE,{"disambiguationData":[TD([[makeQuery(id+"F0.imprint","IMPRINT",EDGE,{"disambiguationData":[TD([[subQ2,-1.0]])],"derivedFrom":subQ1}),1.0]])]});}
            var Q136;
            {var subQ0=sQuery(id+"F0.wireOp",EDGE,"E10.0.15.0");var subQ1=sQuery(id+"F0.wireOp",EDGE,"E3.14.0.1");var subQ2=makeQuery(id+"F0.imprint","INTERSECT",VERTEX,{"derivedFrom":[subQ1,subQ0]});Q136=makeQuery(id+"F0.imprint","IMPRINT",FACE,{"disambiguationData":[TD([[makeQuery(id+"F0.imprint","IMPRINT",EDGE,{"disambiguationData":[TD([[subQ2,-1.0]])],"derivedFrom":subQ1}),1.0]])]});}
            var Q137;
            {var subQ0=sQuery(id+"F0.wireOp",EDGE,"E10.0.15.0");var subQ1=sQuery(id+"F0.wireOp",EDGE,"E3.15.0.0");var subQ2=makeQuery(id+"F0.imprint","INTERSECT",VERTEX,{"derivedFrom":[subQ1,subQ0]});Q137=makeQuery(id+"F0.imprint","IMPRINT",FACE,{"disambiguationData":[TD([[makeQuery(id+"F0.imprint","IMPRINT",EDGE,{"disambiguationData":[TD([[subQ2,-1.0]])],"derivedFrom":subQ1}),1.0]])]});}
            var Q138;
            {var subQ0=sQuery(id+"F0.wireOp",EDGE,"E10.0.15.0");var subQ1=sQuery(id+"F0.wireOp",EDGE,"E3.15.0.1");var subQ2=makeQuery(id+"F0.imprint","INTERSECT",VERTEX,{"derivedFrom":[subQ1,subQ0]});Q138=makeQuery(id+"F0.imprint","IMPRINT",FACE,{"disambiguationData":[TD([[makeQuery(id+"F0.imprint","IMPRINT",EDGE,{"disambiguationData":[TD([[subQ2,-1.0]])],"derivedFrom":subQ1}),1.0]])]});}
            var Q139;
            {var subQ0=sQuery(id+"F0.wireOp",EDGE,"E10.0.15.0");var subQ1=sQuery(id+"F0.wireOp",EDGE,"E3.16.0.0");var subQ2=makeQuery(id+"F0.imprint","INTERSECT",VERTEX,{"derivedFrom":[subQ1,subQ0]});Q139=makeQuery(id+"F0.imprint","IMPRINT",FACE,{"disambiguationData":[TD([[makeQuery(id+"F0.imprint","IMPRINT",EDGE,{"disambiguationData":[TD([[subQ2,-1.0]])],"derivedFrom":subQ1}),1.0]])]});}
            var Q140;
            {var subQ0=sQuery(id+"F0.wireOp",EDGE,"E10.0.15.0");var subQ1=sQuery(id+"F0.wireOp",EDGE,"E3.16.0.1");var subQ2=makeQuery(id+"F0.imprint","INTERSECT",VERTEX,{"derivedFrom":[subQ1,subQ0]});Q140=makeQuery(id+"F0.imprint","IMPRINT",FACE,{"disambiguationData":[TD([[makeQuery(id+"F0.imprint","IMPRINT",EDGE,{"disambiguationData":[TD([[subQ2,-1.0]])],"derivedFrom":subQ1}),1.0]])]});}
            var Q141;
            {var subQ0=sQuery(id+"F0.wireOp",EDGE,"E10.0.16.0");var subQ1=sQuery(id+"F0.wireOp",EDGE,"E3.14.0.1");var subQ2=makeQuery(id+"F0.imprint","INTERSECT",VERTEX,{"derivedFrom":[subQ1,subQ0]});Q141=makeQuery(id+"F0.imprint","IMPRINT",FACE,{"disambiguationData":[TD([[makeQuery(id+"F0.imprint","IMPRINT",EDGE,{"disambiguationData":[TD([[subQ2,-1.0]])],"derivedFrom":subQ1}),1.0]])]});}
            var Q142;
            {var subQ0=sQuery(id+"F0.wireOp",EDGE,"E10.0.16.0");var subQ1=sQuery(id+"F0.wireOp",EDGE,"E3.15.0.0");var subQ2=makeQuery(id+"F0.imprint","INTERSECT",VERTEX,{"derivedFrom":[subQ1,subQ0]});Q142=makeQuery(id+"F0.imprint","IMPRINT",FACE,{"disambiguationData":[TD([[makeQuery(id+"F0.imprint","IMPRINT",EDGE,{"disambiguationData":[TD([[subQ2,-1.0]])],"derivedFrom":subQ1}),1.0]])]});}
            var Q143;
            {var subQ0=sQuery(id+"F0.wireOp",EDGE,"E10.0.16.0");var subQ1=sQuery(id+"F0.wireOp",EDGE,"E3.15.0.1");var subQ2=makeQuery(id+"F0.imprint","INTERSECT",VERTEX,{"derivedFrom":[subQ1,subQ0]});Q143=makeQuery(id+"F0.imprint","IMPRINT",FACE,{"disambiguationData":[TD([[makeQuery(id+"F0.imprint","IMPRINT",EDGE,{"disambiguationData":[TD([[subQ2,-1.0]])],"derivedFrom":subQ1}),1.0]])]});}
            var Q144;
            {var subQ0=sQuery(id+"F0.wireOp",EDGE,"E10.0.16.0");var subQ1=sQuery(id+"F0.wireOp",EDGE,"E3.16.0.0");var subQ2=makeQuery(id+"F0.imprint","INTERSECT",VERTEX,{"derivedFrom":[subQ1,subQ0]});Q144=makeQuery(id+"F0.imprint","IMPRINT",FACE,{"disambiguationData":[TD([[makeQuery(id+"F0.imprint","IMPRINT",EDGE,{"disambiguationData":[TD([[subQ2,-1.0]])],"derivedFrom":subQ1}),1.0]])]});}
            var Q145;
            {var subQ0=sQuery(id+"F0.wireOp",EDGE,"E10.0.16.0");var subQ1=sQuery(id+"F0.wireOp",EDGE,"E3.16.0.1");var subQ2=makeQuery(id+"F0.imprint","INTERSECT",VERTEX,{"derivedFrom":[subQ1,subQ0]});Q145=makeQuery(id+"F0.imprint","IMPRINT",FACE,{"disambiguationData":[TD([[makeQuery(id+"F0.imprint","IMPRINT",EDGE,{"disambiguationData":[TD([[subQ2,-1.0]])],"derivedFrom":subQ1}),1.0]])]});}
            var Q146;
            {var subQ0=sQuery(id+"F0.wireOp",EDGE,"E10.0.17.0");var subQ1=sQuery(id+"F0.wireOp",EDGE,"E3.14.0.1");var subQ2=makeQuery(id+"F0.imprint","INTERSECT",VERTEX,{"derivedFrom":[subQ1,subQ0]});Q146=makeQuery(id+"F0.imprint","IMPRINT",FACE,{"disambiguationData":[TD([[makeQuery(id+"F0.imprint","IMPRINT",EDGE,{"disambiguationData":[TD([[subQ2,-1.0]])],"derivedFrom":subQ1}),1.0]])]});}
            var Q147;
            {var subQ0=sQuery(id+"F0.wireOp",EDGE,"E10.0.17.0");var subQ1=sQuery(id+"F0.wireOp",EDGE,"E3.15.0.0");var subQ2=makeQuery(id+"F0.imprint","INTERSECT",VERTEX,{"derivedFrom":[subQ1,subQ0]});Q147=makeQuery(id+"F0.imprint","IMPRINT",FACE,{"disambiguationData":[TD([[makeQuery(id+"F0.imprint","IMPRINT",EDGE,{"disambiguationData":[TD([[subQ2,-1.0]])],"derivedFrom":subQ1}),1.0]])]});}
            var Q148;
            {var subQ0=sQuery(id+"F0.wireOp",EDGE,"E10.0.18.0");var subQ1=sQuery(id+"F0.wireOp",EDGE,"E3.14.0.1");var subQ2=makeQuery(id+"F0.imprint","INTERSECT",VERTEX,{"derivedFrom":[subQ1,subQ0]});Q148=makeQuery(id+"F0.imprint","IMPRINT",FACE,{"disambiguationData":[TD([[makeQuery(id+"F0.imprint","IMPRINT",EDGE,{"disambiguationData":[TD([[subQ2,-1.0]])],"derivedFrom":subQ1}),1.0]])]});}
            var Q149;
            {var subQ0=sQuery(id+"F0.wireOp",EDGE,"E10.0.18.0");var subQ1=sQuery(id+"F0.wireOp",EDGE,"E3.15.0.0");var subQ2=makeQuery(id+"F0.imprint","INTERSECT",VERTEX,{"derivedFrom":[subQ1,subQ0]});Q149=makeQuery(id+"F0.imprint","IMPRINT",FACE,{"disambiguationData":[TD([[makeQuery(id+"F0.imprint","IMPRINT",EDGE,{"disambiguationData":[TD([[subQ2,-1.0]])],"derivedFrom":subQ1}),1.0]])]});}
            var Q150;
            {var subQ0=sQuery(id+"F0.wireOp",EDGE,"E10.0.19.0");var subQ1=sQuery(id+"F0.wireOp",EDGE,"E3.14.0.1");var subQ2=makeQuery(id+"F0.imprint","INTERSECT",VERTEX,{"derivedFrom":[subQ1,subQ0]});Q150=makeQuery(id+"F0.imprint","IMPRINT",FACE,{"disambiguationData":[TD([[makeQuery(id+"F0.imprint","IMPRINT",EDGE,{"disambiguationData":[TD([[subQ2,-1.0]])],"derivedFrom":subQ1}),1.0]])]});}
            var Q151;
            {var subQ0=sQuery(id+"F0.wireOp",EDGE,"E10.0.19.0");var subQ1=sQuery(id+"F0.wireOp",EDGE,"E3.15.0.0");var subQ2=makeQuery(id+"F0.imprint","INTERSECT",VERTEX,{"derivedFrom":[subQ1,subQ0]});Q151=makeQuery(id+"F0.imprint","IMPRINT",FACE,{"disambiguationData":[TD([[makeQuery(id+"F0.imprint","IMPRINT",EDGE,{"disambiguationData":[TD([[subQ2,-1.0]])],"derivedFrom":subQ1}),1.0]])]});}
            var Q152;
            {var subQ0=sQuery(id+"F0.wireOp",EDGE,"E10.0.19.0");var subQ1=sQuery(id+"F0.wireOp",EDGE,"E3.15.0.1");var subQ2=makeQuery(id+"F0.imprint","INTERSECT",VERTEX,{"derivedFrom":[subQ1,subQ0]});Q152=makeQuery(id+"F0.imprint","IMPRINT",FACE,{"disambiguationData":[TD([[makeQuery(id+"F0.imprint","IMPRINT",EDGE,{"disambiguationData":[TD([[subQ2,-1.0]])],"derivedFrom":subQ1}),1.0]])]});}
            var Q153;
            {var subQ0=sQuery(id+"F0.wireOp",EDGE,"E10.0.19.0");var subQ1=sQuery(id+"F0.wireOp",EDGE,"E3.16.0.0");var subQ2=makeQuery(id+"F0.imprint","INTERSECT",VERTEX,{"derivedFrom":[subQ1,subQ0]});Q153=makeQuery(id+"F0.imprint","IMPRINT",FACE,{"disambiguationData":[TD([[makeQuery(id+"F0.imprint","IMPRINT",EDGE,{"disambiguationData":[TD([[subQ2,-1.0]])],"derivedFrom":subQ1}),1.0]])]});}
            var Q154;
            {var subQ0=sQuery(id+"F0.wireOp",EDGE,"E10.0.20.0");var subQ1=sQuery(id+"F0.wireOp",EDGE,"E3.14.0.1");var subQ2=makeQuery(id+"F0.imprint","INTERSECT",VERTEX,{"derivedFrom":[subQ1,subQ0]});Q154=makeQuery(id+"F0.imprint","IMPRINT",FACE,{"disambiguationData":[TD([[makeQuery(id+"F0.imprint","IMPRINT",EDGE,{"disambiguationData":[TD([[subQ2,-1.0]])],"derivedFrom":subQ1}),1.0]])]});}
            var Q155;
            {var subQ0=sQuery(id+"F0.wireOp",EDGE,"E10.0.20.0");var subQ1=sQuery(id+"F0.wireOp",EDGE,"E3.15.0.0");var subQ2=makeQuery(id+"F0.imprint","INTERSECT",VERTEX,{"derivedFrom":[subQ1,subQ0]});Q155=makeQuery(id+"F0.imprint","IMPRINT",FACE,{"disambiguationData":[TD([[makeQuery(id+"F0.imprint","IMPRINT",EDGE,{"disambiguationData":[TD([[subQ2,-1.0]])],"derivedFrom":subQ1}),1.0]])]});}
            var Q156;
            {var subQ0=sQuery(id+"F0.wireOp",EDGE,"E10.0.20.0");var subQ1=sQuery(id+"F0.wireOp",EDGE,"E3.15.0.1");var subQ2=makeQuery(id+"F0.imprint","INTERSECT",VERTEX,{"derivedFrom":[subQ1,subQ0]});Q156=makeQuery(id+"F0.imprint","IMPRINT",FACE,{"disambiguationData":[TD([[makeQuery(id+"F0.imprint","IMPRINT",EDGE,{"disambiguationData":[TD([[subQ2,-1.0]])],"derivedFrom":subQ1}),1.0]])]});}
            var Q157;
            {var subQ0=sQuery(id+"F0.wireOp",EDGE,"E10.0.20.0");var subQ1=sQuery(id+"F0.wireOp",EDGE,"E3.16.0.0");var subQ2=makeQuery(id+"F0.imprint","INTERSECT",VERTEX,{"derivedFrom":[subQ1,subQ0]});Q157=makeQuery(id+"F0.imprint","IMPRINT",FACE,{"disambiguationData":[TD([[makeQuery(id+"F0.imprint","IMPRINT",EDGE,{"disambiguationData":[TD([[subQ2,-1.0]])],"derivedFrom":subQ1}),1.0]])]});}
            var Q158;
            {var subQ0=sQuery(id+"F0.wireOp",EDGE,"E10.0.21.0");var subQ1=sQuery(id+"F0.wireOp",EDGE,"E3.14.0.1");var subQ2=makeQuery(id+"F0.imprint","INTERSECT",VERTEX,{"derivedFrom":[subQ1,subQ0]});Q158=makeQuery(id+"F0.imprint","IMPRINT",FACE,{"disambiguationData":[TD([[makeQuery(id+"F0.imprint","IMPRINT",EDGE,{"disambiguationData":[TD([[subQ2,-1.0]])],"derivedFrom":subQ1}),1.0]])]});}
            var Q159;
            {var subQ0=sQuery(id+"F0.wireOp",EDGE,"E10.0.21.0");var subQ1=sQuery(id+"F0.wireOp",EDGE,"E3.15.0.0");var subQ2=makeQuery(id+"F0.imprint","INTERSECT",VERTEX,{"derivedFrom":[subQ1,subQ0]});Q159=makeQuery(id+"F0.imprint","IMPRINT",FACE,{"disambiguationData":[TD([[makeQuery(id+"F0.imprint","IMPRINT",EDGE,{"disambiguationData":[TD([[subQ2,-1.0]])],"derivedFrom":subQ1}),1.0]])]});}
            var Q160;
            {var subQ0=sQuery(id+"F0.wireOp",EDGE,"E10.0.21.0");var subQ1=sQuery(id+"F0.wireOp",EDGE,"E3.15.0.1");var subQ2=makeQuery(id+"F0.imprint","INTERSECT",VERTEX,{"derivedFrom":[subQ1,subQ0]});Q160=makeQuery(id+"F0.imprint","IMPRINT",FACE,{"disambiguationData":[TD([[makeQuery(id+"F0.imprint","IMPRINT",EDGE,{"disambiguationData":[TD([[subQ2,-1.0]])],"derivedFrom":subQ1}),1.0]])]});}
            var Q161;
            {var subQ0=sQuery(id+"F0.wireOp",EDGE,"E10.0.21.0");var subQ1=sQuery(id+"F0.wireOp",EDGE,"E3.16.0.0");var subQ2=makeQuery(id+"F0.imprint","INTERSECT",VERTEX,{"derivedFrom":[subQ1,subQ0]});Q161=makeQuery(id+"F0.imprint","IMPRINT",FACE,{"disambiguationData":[TD([[makeQuery(id+"F0.imprint","IMPRINT",EDGE,{"disambiguationData":[TD([[subQ2,-1.0]])],"derivedFrom":subQ1}),1.0]])]});}
            var Q162;
            {var subQ0=sQuery(id+"F0.wireOp",EDGE,"E10.0.22.0");var subQ1=sQuery(id+"F0.wireOp",EDGE,"E3.14.0.1");var subQ2=makeQuery(id+"F0.imprint","INTERSECT",VERTEX,{"derivedFrom":[subQ1,subQ0]});Q162=makeQuery(id+"F0.imprint","IMPRINT",FACE,{"disambiguationData":[TD([[makeQuery(id+"F0.imprint","IMPRINT",EDGE,{"disambiguationData":[TD([[subQ2,-1.0]])],"derivedFrom":subQ1}),1.0]])]});}
            var Q163;
            {var subQ0=sQuery(id+"F0.wireOp",EDGE,"E10.0.22.0");var subQ1=sQuery(id+"F0.wireOp",EDGE,"E3.15.0.0");var subQ2=makeQuery(id+"F0.imprint","INTERSECT",VERTEX,{"derivedFrom":[subQ1,subQ0]});Q163=makeQuery(id+"F0.imprint","IMPRINT",FACE,{"disambiguationData":[TD([[makeQuery(id+"F0.imprint","IMPRINT",EDGE,{"disambiguationData":[TD([[subQ2,-1.0]])],"derivedFrom":subQ1}),1.0]])]});}
            var Q164;
            {var subQ0=sQuery(id+"F0.wireOp",EDGE,"E10.0.22.0");var subQ1=sQuery(id+"F0.wireOp",EDGE,"E3.15.0.1");var subQ2=makeQuery(id+"F0.imprint","INTERSECT",VERTEX,{"derivedFrom":[subQ1,subQ0]});Q164=makeQuery(id+"F0.imprint","IMPRINT",FACE,{"disambiguationData":[TD([[makeQuery(id+"F0.imprint","IMPRINT",EDGE,{"disambiguationData":[TD([[subQ2,-1.0]])],"derivedFrom":subQ1}),1.0]])]});}
            var Q165;
            {var subQ0=sQuery(id+"F0.wireOp",EDGE,"E10.0.22.0");var subQ1=sQuery(id+"F0.wireOp",EDGE,"E3.16.0.0");var subQ2=makeQuery(id+"F0.imprint","INTERSECT",VERTEX,{"derivedFrom":[subQ1,subQ0]});Q165=makeQuery(id+"F0.imprint","IMPRINT",FACE,{"disambiguationData":[TD([[makeQuery(id+"F0.imprint","IMPRINT",EDGE,{"disambiguationData":[TD([[subQ2,-1.0]])],"derivedFrom":subQ1}),1.0]])]});}
            var Q166;
            {var subQ0=sQuery(id+"F0.wireOp",EDGE,"E10.0.23.0");var subQ1=sQuery(id+"F0.wireOp",EDGE,"E3.14.0.1");var subQ2=makeQuery(id+"F0.imprint","INTERSECT",VERTEX,{"derivedFrom":[subQ1,subQ0]});Q166=makeQuery(id+"F0.imprint","IMPRINT",FACE,{"disambiguationData":[TD([[makeQuery(id+"F0.imprint","IMPRINT",EDGE,{"disambiguationData":[TD([[subQ2,-1.0]])],"derivedFrom":subQ1}),1.0]])]});}
            var Q167;
            {var subQ0=sQuery(id+"F0.wireOp",EDGE,"E10.0.23.0");var subQ1=sQuery(id+"F0.wireOp",EDGE,"E3.15.0.0");var subQ2=makeQuery(id+"F0.imprint","INTERSECT",VERTEX,{"derivedFrom":[subQ1,subQ0]});Q167=makeQuery(id+"F0.imprint","IMPRINT",FACE,{"disambiguationData":[TD([[makeQuery(id+"F0.imprint","IMPRINT",EDGE,{"disambiguationData":[TD([[subQ2,-1.0]])],"derivedFrom":subQ1}),1.0]])]});}
            var Q168;
            {var subQ0=sQuery(id+"F0.wireOp",EDGE,"E10.0.10.0");var subQ1=sQuery(id+"F0.wireOp",EDGE,"E3.18.0.0");var subQ2=makeQuery(id+"F0.imprint","INTERSECT",VERTEX,{"derivedFrom":[subQ1,subQ0]});Q168=makeQuery(id+"F0.imprint","IMPRINT",FACE,{"disambiguationData":[TD([[makeQuery(id+"F0.imprint","IMPRINT",EDGE,{"disambiguationData":[TD([[subQ2,-1.0]])],"derivedFrom":subQ1}),1.0]])]});}
            var Q169;
            {var subQ0=sQuery(id+"F0.wireOp",EDGE,"E10.0.10.0");var subQ1=sQuery(id+"F0.wireOp",EDGE,"E3.18.0.1");var subQ2=makeQuery(id+"F0.imprint","INTERSECT",VERTEX,{"derivedFrom":[subQ1,subQ0]});Q169=makeQuery(id+"F0.imprint","IMPRINT",FACE,{"disambiguationData":[TD([[makeQuery(id+"F0.imprint","IMPRINT",EDGE,{"disambiguationData":[TD([[subQ2,-1.0]])],"derivedFrom":subQ1}),1.0]])]});}
            var Q170;
            {var subQ0=sQuery(id+"F0.wireOp",EDGE,"E10.0.10.0");var subQ1=sQuery(id+"F0.wireOp",EDGE,"E3.19.0.0");var subQ2=makeQuery(id+"F0.imprint","INTERSECT",VERTEX,{"derivedFrom":[subQ1,subQ0]});Q170=makeQuery(id+"F0.imprint","IMPRINT",FACE,{"disambiguationData":[TD([[makeQuery(id+"F0.imprint","IMPRINT",EDGE,{"disambiguationData":[TD([[subQ2,-1.0]])],"derivedFrom":subQ1}),1.0]])]});}
            var Q171;
            {var subQ0=sQuery(id+"F0.wireOp",EDGE,"E10.0.10.0");var subQ1=sQuery(id+"F0.wireOp",EDGE,"E3.19.0.1");var subQ2=makeQuery(id+"F0.imprint","INTERSECT",VERTEX,{"derivedFrom":[subQ1,subQ0]});Q171=makeQuery(id+"F0.imprint","IMPRINT",FACE,{"disambiguationData":[TD([[makeQuery(id+"F0.imprint","IMPRINT",EDGE,{"disambiguationData":[TD([[subQ2,-1.0]])],"derivedFrom":subQ1}),1.0]])]});}
            var Q172;
            {var subQ0=sQuery(id+"F0.wireOp",EDGE,"E10.0.10.0");var subQ1=sQuery(id+"F0.wireOp",EDGE,"E3.20.0.0");var subQ2=makeQuery(id+"F0.imprint","INTERSECT",VERTEX,{"derivedFrom":[subQ1,subQ0]});Q172=makeQuery(id+"F0.imprint","IMPRINT",FACE,{"disambiguationData":[TD([[makeQuery(id+"F0.imprint","IMPRINT",EDGE,{"disambiguationData":[TD([[subQ2,-1.0]])],"derivedFrom":subQ1}),1.0]])]});}
            var Q173;
            {var subQ0=sQuery(id+"F0.wireOp",EDGE,"E10.3.10.0");var subQ1=sQuery(id+"F0.wireOp",EDGE,"E3.20.0.0");var subQ2=makeQuery(id+"F0.imprint","INTERSECT",VERTEX,{"derivedFrom":[subQ1,subQ0]});Q173=makeQuery(id+"F0.imprint","IMPRINT",FACE,{"disambiguationData":[TD([[makeQuery(id+"F0.imprint","IMPRINT",EDGE,{"disambiguationData":[TD([[subQ2,-1.0]])],"derivedFrom":subQ1}),1.0]])]});}
            var Q174;
            {var subQ0=sQuery(id+"F0.wireOp",EDGE,"E10.0.11.0");var subQ1=sQuery(id+"F0.wireOp",EDGE,"E3.20.0.0");var subQ2=makeQuery(id+"F0.imprint","INTERSECT",VERTEX,{"derivedFrom":[subQ1,subQ0]});Q174=makeQuery(id+"F0.imprint","IMPRINT",FACE,{"disambiguationData":[TD([[makeQuery(id+"F0.imprint","IMPRINT",EDGE,{"disambiguationData":[TD([[subQ2,-1.0]])],"derivedFrom":subQ1}),1.0]])]});}
            var Q175;
            {var subQ0=sQuery(id+"F0.wireOp",EDGE,"E10.0.12.0");var subQ1=sQuery(id+"F0.wireOp",EDGE,"E3.20.0.0");var subQ2=makeQuery(id+"F0.imprint","INTERSECT",VERTEX,{"derivedFrom":[subQ1,subQ0]});Q175=makeQuery(id+"F0.imprint","IMPRINT",FACE,{"disambiguationData":[TD([[makeQuery(id+"F0.imprint","IMPRINT",EDGE,{"disambiguationData":[TD([[subQ2,-1.0]])],"derivedFrom":subQ1}),1.0]])]});}
            var Q176;
            {var subQ0=sQuery(id+"F0.wireOp",EDGE,"E10.3.12.0");var subQ1=sQuery(id+"F0.wireOp",EDGE,"E3.20.0.0");var subQ2=makeQuery(id+"F0.imprint","INTERSECT",VERTEX,{"derivedFrom":[subQ1,subQ0]});Q176=makeQuery(id+"F0.imprint","IMPRINT",FACE,{"disambiguationData":[TD([[makeQuery(id+"F0.imprint","IMPRINT",EDGE,{"disambiguationData":[TD([[subQ2,-1.0]])],"derivedFrom":subQ1}),1.0]])]});}
            var Q177;
            {var subQ0=sQuery(id+"F0.wireOp",EDGE,"E10.0.13.0");var subQ1=sQuery(id+"F0.wireOp",EDGE,"E3.20.0.0");var subQ2=makeQuery(id+"F0.imprint","INTERSECT",VERTEX,{"derivedFrom":[subQ1,subQ0]});Q177=makeQuery(id+"F0.imprint","IMPRINT",FACE,{"disambiguationData":[TD([[makeQuery(id+"F0.imprint","IMPRINT",EDGE,{"disambiguationData":[TD([[subQ2,-1.0]])],"derivedFrom":subQ1}),1.0]])]});}
            var Q178;
            {var subQ0=sQuery(id+"F0.wireOp",EDGE,"E10.3.11.0");var subQ1=sQuery(id+"F0.wireOp",EDGE,"E3.20.0.0");var subQ2=makeQuery(id+"F0.imprint","INTERSECT",VERTEX,{"derivedFrom":[subQ1,subQ0]});Q178=makeQuery(id+"F0.imprint","IMPRINT",FACE,{"disambiguationData":[TD([[makeQuery(id+"F0.imprint","IMPRINT",EDGE,{"disambiguationData":[TD([[subQ2,-1.0]])],"derivedFrom":subQ1}),1.0]])]});}
            var Q179;
            {var subQ0=sQuery(id+"F0.wireOp",EDGE,"E10.3.13.0");var subQ1=sQuery(id+"F0.wireOp",EDGE,"E3.20.0.0");var subQ2=makeQuery(id+"F0.imprint","INTERSECT",VERTEX,{"derivedFrom":[subQ1,subQ0]});Q179=makeQuery(id+"F0.imprint","IMPRINT",FACE,{"disambiguationData":[TD([[makeQuery(id+"F0.imprint","IMPRINT",EDGE,{"disambiguationData":[TD([[subQ2,-1.0]])],"derivedFrom":subQ1}),1.0]])]});}
            var Q180;
            {var subQ0=sQuery(id+"F0.wireOp",EDGE,"E10.0.14.0");var subQ1=sQuery(id+"F0.wireOp",EDGE,"E3.20.0.0");var subQ2=makeQuery(id+"F0.imprint","INTERSECT",VERTEX,{"derivedFrom":[subQ1,subQ0]});Q180=makeQuery(id+"F0.imprint","IMPRINT",FACE,{"disambiguationData":[TD([[makeQuery(id+"F0.imprint","IMPRINT",EDGE,{"disambiguationData":[TD([[subQ2,-1.0]])],"derivedFrom":subQ1}),1.0]])]});}
            var Q181;
            {var subQ0=sQuery(id+"F0.wireOp",EDGE,"E10.3.14.0");var subQ1=sQuery(id+"F0.wireOp",EDGE,"E3.20.0.0");var subQ2=makeQuery(id+"F0.imprint","INTERSECT",VERTEX,{"derivedFrom":[subQ1,subQ0]});Q181=makeQuery(id+"F0.imprint","IMPRINT",FACE,{"disambiguationData":[TD([[makeQuery(id+"F0.imprint","IMPRINT",EDGE,{"disambiguationData":[TD([[subQ2,-1.0]])],"derivedFrom":subQ1}),1.0]])]});}
            var Q182;
            {var subQ0=sQuery(id+"F0.wireOp",EDGE,"E10.0.15.0");var subQ1=sQuery(id+"F0.wireOp",EDGE,"E3.20.0.0");var subQ2=makeQuery(id+"F0.imprint","INTERSECT",VERTEX,{"derivedFrom":[subQ1,subQ0]});Q182=makeQuery(id+"F0.imprint","IMPRINT",FACE,{"disambiguationData":[TD([[makeQuery(id+"F0.imprint","IMPRINT",EDGE,{"disambiguationData":[TD([[subQ2,-1.0]])],"derivedFrom":subQ1}),1.0]])]});}
            var Q183;
            {var subQ0=sQuery(id+"F0.wireOp",EDGE,"E10.3.15.0");var subQ1=sQuery(id+"F0.wireOp",EDGE,"E3.20.0.0");var subQ2=makeQuery(id+"F0.imprint","INTERSECT",VERTEX,{"derivedFrom":[subQ1,subQ0]});Q183=makeQuery(id+"F0.imprint","IMPRINT",FACE,{"disambiguationData":[TD([[makeQuery(id+"F0.imprint","IMPRINT",EDGE,{"disambiguationData":[TD([[subQ2,-1.0]])],"derivedFrom":subQ1}),1.0]])]});}
            var Q184;
            {var subQ0=sQuery(id+"F0.wireOp",EDGE,"E10.0.16.0");var subQ1=sQuery(id+"F0.wireOp",EDGE,"E3.20.0.0");var subQ2=makeQuery(id+"F0.imprint","INTERSECT",VERTEX,{"derivedFrom":[subQ1,subQ0]});Q184=makeQuery(id+"F0.imprint","IMPRINT",FACE,{"disambiguationData":[TD([[makeQuery(id+"F0.imprint","IMPRINT",EDGE,{"disambiguationData":[TD([[subQ2,-1.0]])],"derivedFrom":subQ1}),1.0]])]});}
            var Q185;
            {var subQ0=sQuery(id+"F0.wireOp",EDGE,"E10.0.16.0");var subQ1=sQuery(id+"F0.wireOp",EDGE,"E3.18.0.0");var subQ2=makeQuery(id+"F0.imprint","INTERSECT",VERTEX,{"derivedFrom":[subQ1,subQ0]});Q185=makeQuery(id+"F0.imprint","IMPRINT",FACE,{"disambiguationData":[TD([[makeQuery(id+"F0.imprint","IMPRINT",EDGE,{"disambiguationData":[TD([[subQ2,-1.0]])],"derivedFrom":subQ1}),1.0]])]});}
            var Q186;
            {var subQ0=sQuery(id+"F0.wireOp",EDGE,"E10.3.15.0");var subQ1=sQuery(id+"F0.wireOp",EDGE,"E3.18.0.0");var subQ2=makeQuery(id+"F0.imprint","INTERSECT",VERTEX,{"derivedFrom":[subQ1,subQ0]});Q186=makeQuery(id+"F0.imprint","IMPRINT",FACE,{"disambiguationData":[TD([[makeQuery(id+"F0.imprint","IMPRINT",EDGE,{"disambiguationData":[TD([[subQ2,-1.0]])],"derivedFrom":subQ1}),1.0]])]});}
            var Q187;
            {var subQ0=sQuery(id+"F0.wireOp",EDGE,"E10.0.15.0");var subQ1=sQuery(id+"F0.wireOp",EDGE,"E3.18.0.0");var subQ2=makeQuery(id+"F0.imprint","INTERSECT",VERTEX,{"derivedFrom":[subQ1,subQ0]});Q187=makeQuery(id+"F0.imprint","IMPRINT",FACE,{"disambiguationData":[TD([[makeQuery(id+"F0.imprint","IMPRINT",EDGE,{"disambiguationData":[TD([[subQ2,-1.0]])],"derivedFrom":subQ1}),1.0]])]});}
            var Q188;
            {var subQ0=sQuery(id+"F0.wireOp",EDGE,"E10.3.14.0");var subQ1=sQuery(id+"F0.wireOp",EDGE,"E3.18.0.0");var subQ2=makeQuery(id+"F0.imprint","INTERSECT",VERTEX,{"derivedFrom":[subQ1,subQ0]});Q188=makeQuery(id+"F0.imprint","IMPRINT",FACE,{"disambiguationData":[TD([[makeQuery(id+"F0.imprint","IMPRINT",EDGE,{"disambiguationData":[TD([[subQ2,-1.0]])],"derivedFrom":subQ1}),1.0]])]});}
            var Q189;
            {var subQ0=sQuery(id+"F0.wireOp",EDGE,"E10.0.14.0");var subQ1=sQuery(id+"F0.wireOp",EDGE,"E3.18.0.0");var subQ2=makeQuery(id+"F0.imprint","INTERSECT",VERTEX,{"derivedFrom":[subQ1,subQ0]});Q189=makeQuery(id+"F0.imprint","IMPRINT",FACE,{"disambiguationData":[TD([[makeQuery(id+"F0.imprint","IMPRINT",EDGE,{"disambiguationData":[TD([[subQ2,-1.0]])],"derivedFrom":subQ1}),1.0]])]});}
            var Q190;
            {var subQ0=sQuery(id+"F0.wireOp",EDGE,"E10.3.13.0");var subQ1=sQuery(id+"F0.wireOp",EDGE,"E3.18.0.0");var subQ2=makeQuery(id+"F0.imprint","INTERSECT",VERTEX,{"derivedFrom":[subQ1,subQ0]});Q190=makeQuery(id+"F0.imprint","IMPRINT",FACE,{"disambiguationData":[TD([[makeQuery(id+"F0.imprint","IMPRINT",EDGE,{"disambiguationData":[TD([[subQ2,-1.0]])],"derivedFrom":subQ1}),1.0]])]});}
            var Q191;
            {var subQ0=sQuery(id+"F0.wireOp",EDGE,"E10.0.13.0");var subQ1=sQuery(id+"F0.wireOp",EDGE,"E3.18.0.0");var subQ2=makeQuery(id+"F0.imprint","INTERSECT",VERTEX,{"derivedFrom":[subQ1,subQ0]});Q191=makeQuery(id+"F0.imprint","IMPRINT",FACE,{"disambiguationData":[TD([[makeQuery(id+"F0.imprint","IMPRINT",EDGE,{"disambiguationData":[TD([[subQ2,-1.0]])],"derivedFrom":subQ1}),1.0]])]});}
            var Q192;
            {var subQ0=sQuery(id+"F0.wireOp",EDGE,"E10.3.12.0");var subQ1=sQuery(id+"F0.wireOp",EDGE,"E3.18.0.0");var subQ2=makeQuery(id+"F0.imprint","INTERSECT",VERTEX,{"derivedFrom":[subQ1,subQ0]});Q192=makeQuery(id+"F0.imprint","IMPRINT",FACE,{"disambiguationData":[TD([[makeQuery(id+"F0.imprint","IMPRINT",EDGE,{"disambiguationData":[TD([[subQ2,-1.0]])],"derivedFrom":subQ1}),1.0]])]});}
            var Q193;
            {var subQ0=sQuery(id+"F0.wireOp",EDGE,"E10.0.12.0");var subQ1=sQuery(id+"F0.wireOp",EDGE,"E3.18.0.0");var subQ2=makeQuery(id+"F0.imprint","INTERSECT",VERTEX,{"derivedFrom":[subQ1,subQ0]});Q193=makeQuery(id+"F0.imprint","IMPRINT",FACE,{"disambiguationData":[TD([[makeQuery(id+"F0.imprint","IMPRINT",EDGE,{"disambiguationData":[TD([[subQ2,-1.0]])],"derivedFrom":subQ1}),1.0]])]});}
            var Q194;
            {var subQ0=sQuery(id+"F0.wireOp",EDGE,"E10.3.11.0");var subQ1=sQuery(id+"F0.wireOp",EDGE,"E3.18.0.0");var subQ2=makeQuery(id+"F0.imprint","INTERSECT",VERTEX,{"derivedFrom":[subQ1,subQ0]});Q194=makeQuery(id+"F0.imprint","IMPRINT",FACE,{"disambiguationData":[TD([[makeQuery(id+"F0.imprint","IMPRINT",EDGE,{"disambiguationData":[TD([[subQ2,-1.0]])],"derivedFrom":subQ1}),1.0]])]});}
            var Q195;
            {var subQ0=sQuery(id+"F0.wireOp",EDGE,"E10.0.11.0");var subQ1=sQuery(id+"F0.wireOp",EDGE,"E3.18.0.0");var subQ2=makeQuery(id+"F0.imprint","INTERSECT",VERTEX,{"derivedFrom":[subQ1,subQ0]});Q195=makeQuery(id+"F0.imprint","IMPRINT",FACE,{"disambiguationData":[TD([[makeQuery(id+"F0.imprint","IMPRINT",EDGE,{"disambiguationData":[TD([[subQ2,-1.0]])],"derivedFrom":subQ1}),1.0]])]});}
            var Q196;
            {var subQ0=sQuery(id+"F0.wireOp",EDGE,"E10.3.10.0");var subQ1=sQuery(id+"F0.wireOp",EDGE,"E3.18.0.0");var subQ2=makeQuery(id+"F0.imprint","INTERSECT",VERTEX,{"derivedFrom":[subQ1,subQ0]});Q196=makeQuery(id+"F0.imprint","IMPRINT",FACE,{"disambiguationData":[TD([[makeQuery(id+"F0.imprint","IMPRINT",EDGE,{"disambiguationData":[TD([[subQ2,-1.0]])],"derivedFrom":subQ1}),1.0]])]});}
            var Q197;
            {var subQ0=sQuery(id+"F0.wireOp",EDGE,"E10.0.11.0");var subQ1=sQuery(id+"F0.wireOp",EDGE,"E3.18.0.1");var subQ2=makeQuery(id+"F0.imprint","INTERSECT",VERTEX,{"derivedFrom":[subQ1,subQ0]});Q197=makeQuery(id+"F0.imprint","IMPRINT",FACE,{"disambiguationData":[TD([[makeQuery(id+"F0.imprint","IMPRINT",EDGE,{"disambiguationData":[TD([[subQ2,-1.0]])],"derivedFrom":subQ1}),1.0]])]});}
            var Q198;
            {var subQ0=sQuery(id+"F0.wireOp",EDGE,"E10.0.11.0");var subQ1=sQuery(id+"F0.wireOp",EDGE,"E3.19.0.0");var subQ2=makeQuery(id+"F0.imprint","INTERSECT",VERTEX,{"derivedFrom":[subQ1,subQ0]});Q198=makeQuery(id+"F0.imprint","IMPRINT",FACE,{"disambiguationData":[TD([[makeQuery(id+"F0.imprint","IMPRINT",EDGE,{"disambiguationData":[TD([[subQ2,-1.0]])],"derivedFrom":subQ1}),1.0]])]});}
            var Q199;
            {var subQ0=sQuery(id+"F0.wireOp",EDGE,"E10.0.11.0");var subQ1=sQuery(id+"F0.wireOp",EDGE,"E3.19.0.1");var subQ2=makeQuery(id+"F0.imprint","INTERSECT",VERTEX,{"derivedFrom":[subQ1,subQ0]});Q199=makeQuery(id+"F0.imprint","IMPRINT",FACE,{"disambiguationData":[TD([[makeQuery(id+"F0.imprint","IMPRINT",EDGE,{"disambiguationData":[TD([[subQ2,-1.0]])],"derivedFrom":subQ1}),1.0]])]});}
            var Q200;
            {var subQ0=sQuery(id+"F0.wireOp",EDGE,"E10.0.12.0");var subQ1=sQuery(id+"F0.wireOp",EDGE,"E3.18.0.1");var subQ2=makeQuery(id+"F0.imprint","INTERSECT",VERTEX,{"derivedFrom":[subQ1,subQ0]});Q200=makeQuery(id+"F0.imprint","IMPRINT",FACE,{"disambiguationData":[TD([[makeQuery(id+"F0.imprint","IMPRINT",EDGE,{"disambiguationData":[TD([[subQ2,-1.0]])],"derivedFrom":subQ1}),1.0]])]});}
            var Q201;
            {var subQ0=sQuery(id+"F0.wireOp",EDGE,"E10.0.12.0");var subQ1=sQuery(id+"F0.wireOp",EDGE,"E3.19.0.0");var subQ2=makeQuery(id+"F0.imprint","INTERSECT",VERTEX,{"derivedFrom":[subQ1,subQ0]});Q201=makeQuery(id+"F0.imprint","IMPRINT",FACE,{"disambiguationData":[TD([[makeQuery(id+"F0.imprint","IMPRINT",EDGE,{"disambiguationData":[TD([[subQ2,-1.0]])],"derivedFrom":subQ1}),1.0]])]});}
            var Q202;
            {var subQ0=sQuery(id+"F0.wireOp",EDGE,"E10.0.12.0");var subQ1=sQuery(id+"F0.wireOp",EDGE,"E3.19.0.1");var subQ2=makeQuery(id+"F0.imprint","INTERSECT",VERTEX,{"derivedFrom":[subQ1,subQ0]});Q202=makeQuery(id+"F0.imprint","IMPRINT",FACE,{"disambiguationData":[TD([[makeQuery(id+"F0.imprint","IMPRINT",EDGE,{"disambiguationData":[TD([[subQ2,-1.0]])],"derivedFrom":subQ1}),1.0]])]});}
            var Q203;
            {var subQ0=sQuery(id+"F0.wireOp",EDGE,"E10.0.13.0");var subQ1=sQuery(id+"F0.wireOp",EDGE,"E3.18.0.1");var subQ2=makeQuery(id+"F0.imprint","INTERSECT",VERTEX,{"derivedFrom":[subQ1,subQ0]});Q203=makeQuery(id+"F0.imprint","IMPRINT",FACE,{"disambiguationData":[TD([[makeQuery(id+"F0.imprint","IMPRINT",EDGE,{"disambiguationData":[TD([[subQ2,-1.0]])],"derivedFrom":subQ1}),1.0]])]});}
            var Q204;
            {var subQ0=sQuery(id+"F0.wireOp",EDGE,"E10.0.13.0");var subQ1=sQuery(id+"F0.wireOp",EDGE,"E3.19.0.0");var subQ2=makeQuery(id+"F0.imprint","INTERSECT",VERTEX,{"derivedFrom":[subQ1,subQ0]});Q204=makeQuery(id+"F0.imprint","IMPRINT",FACE,{"disambiguationData":[TD([[makeQuery(id+"F0.imprint","IMPRINT",EDGE,{"disambiguationData":[TD([[subQ2,-1.0]])],"derivedFrom":subQ1}),1.0]])]});}
            var Q205;
            {var subQ0=sQuery(id+"F0.wireOp",EDGE,"E10.0.13.0");var subQ1=sQuery(id+"F0.wireOp",EDGE,"E3.19.0.1");var subQ2=makeQuery(id+"F0.imprint","INTERSECT",VERTEX,{"derivedFrom":[subQ1,subQ0]});Q205=makeQuery(id+"F0.imprint","IMPRINT",FACE,{"disambiguationData":[TD([[makeQuery(id+"F0.imprint","IMPRINT",EDGE,{"disambiguationData":[TD([[subQ2,-1.0]])],"derivedFrom":subQ1}),1.0]])]});}
            var Q206;
            {var subQ0=sQuery(id+"F0.wireOp",EDGE,"E10.0.14.0");var subQ1=sQuery(id+"F0.wireOp",EDGE,"E3.18.0.1");var subQ2=makeQuery(id+"F0.imprint","INTERSECT",VERTEX,{"derivedFrom":[subQ1,subQ0]});Q206=makeQuery(id+"F0.imprint","IMPRINT",FACE,{"disambiguationData":[TD([[makeQuery(id+"F0.imprint","IMPRINT",EDGE,{"disambiguationData":[TD([[subQ2,-1.0]])],"derivedFrom":subQ1}),1.0]])]});}
            var Q207;
            {var subQ0=sQuery(id+"F0.wireOp",EDGE,"E10.0.14.0");var subQ1=sQuery(id+"F0.wireOp",EDGE,"E3.19.0.0");var subQ2=makeQuery(id+"F0.imprint","INTERSECT",VERTEX,{"derivedFrom":[subQ1,subQ0]});Q207=makeQuery(id+"F0.imprint","IMPRINT",FACE,{"disambiguationData":[TD([[makeQuery(id+"F0.imprint","IMPRINT",EDGE,{"disambiguationData":[TD([[subQ2,-1.0]])],"derivedFrom":subQ1}),1.0]])]});}
            var Q208;
            {var subQ0=sQuery(id+"F0.wireOp",EDGE,"E10.0.14.0");var subQ1=sQuery(id+"F0.wireOp",EDGE,"E3.19.0.1");var subQ2=makeQuery(id+"F0.imprint","INTERSECT",VERTEX,{"derivedFrom":[subQ1,subQ0]});Q208=makeQuery(id+"F0.imprint","IMPRINT",FACE,{"disambiguationData":[TD([[makeQuery(id+"F0.imprint","IMPRINT",EDGE,{"disambiguationData":[TD([[subQ2,-1.0]])],"derivedFrom":subQ1}),1.0]])]});}
            var Q209;
            {var subQ0=sQuery(id+"F0.wireOp",EDGE,"E10.0.15.0");var subQ1=sQuery(id+"F0.wireOp",EDGE,"E3.18.0.1");var subQ2=makeQuery(id+"F0.imprint","INTERSECT",VERTEX,{"derivedFrom":[subQ1,subQ0]});Q209=makeQuery(id+"F0.imprint","IMPRINT",FACE,{"disambiguationData":[TD([[makeQuery(id+"F0.imprint","IMPRINT",EDGE,{"disambiguationData":[TD([[subQ2,-1.0]])],"derivedFrom":subQ1}),1.0]])]});}
            var Q210;
            {var subQ0=sQuery(id+"F0.wireOp",EDGE,"E10.0.15.0");var subQ1=sQuery(id+"F0.wireOp",EDGE,"E3.19.0.0");var subQ2=makeQuery(id+"F0.imprint","INTERSECT",VERTEX,{"derivedFrom":[subQ1,subQ0]});Q210=makeQuery(id+"F0.imprint","IMPRINT",FACE,{"disambiguationData":[TD([[makeQuery(id+"F0.imprint","IMPRINT",EDGE,{"disambiguationData":[TD([[subQ2,-1.0]])],"derivedFrom":subQ1}),1.0]])]});}
            var Q211;
            {var subQ0=sQuery(id+"F0.wireOp",EDGE,"E10.0.15.0");var subQ1=sQuery(id+"F0.wireOp",EDGE,"E3.19.0.1");var subQ2=makeQuery(id+"F0.imprint","INTERSECT",VERTEX,{"derivedFrom":[subQ1,subQ0]});Q211=makeQuery(id+"F0.imprint","IMPRINT",FACE,{"disambiguationData":[TD([[makeQuery(id+"F0.imprint","IMPRINT",EDGE,{"disambiguationData":[TD([[subQ2,-1.0]])],"derivedFrom":subQ1}),1.0]])]});}
            var Q212;
            {var subQ0=sQuery(id+"F0.wireOp",EDGE,"E10.0.16.0");var subQ1=sQuery(id+"F0.wireOp",EDGE,"E3.18.0.1");var subQ2=makeQuery(id+"F0.imprint","INTERSECT",VERTEX,{"derivedFrom":[subQ1,subQ0]});Q212=makeQuery(id+"F0.imprint","IMPRINT",FACE,{"disambiguationData":[TD([[makeQuery(id+"F0.imprint","IMPRINT",EDGE,{"disambiguationData":[TD([[subQ2,-1.0]])],"derivedFrom":subQ1}),1.0]])]});}
            var Q213;
            {var subQ0=sQuery(id+"F0.wireOp",EDGE,"E10.0.16.0");var subQ1=sQuery(id+"F0.wireOp",EDGE,"E3.19.0.0");var subQ2=makeQuery(id+"F0.imprint","INTERSECT",VERTEX,{"derivedFrom":[subQ1,subQ0]});Q213=makeQuery(id+"F0.imprint","IMPRINT",FACE,{"disambiguationData":[TD([[makeQuery(id+"F0.imprint","IMPRINT",EDGE,{"disambiguationData":[TD([[subQ2,-1.0]])],"derivedFrom":subQ1}),1.0]])]});}
            var Q214;
            {var subQ0=sQuery(id+"F0.wireOp",EDGE,"E10.0.16.0");var subQ1=sQuery(id+"F0.wireOp",EDGE,"E3.19.0.1");var subQ2=makeQuery(id+"F0.imprint","INTERSECT",VERTEX,{"derivedFrom":[subQ1,subQ0]});Q214=makeQuery(id+"F0.imprint","IMPRINT",FACE,{"disambiguationData":[TD([[makeQuery(id+"F0.imprint","IMPRINT",EDGE,{"disambiguationData":[TD([[subQ2,-1.0]])],"derivedFrom":subQ1}),1.0]])]});}
            var Q215;
            Q215=makeQuery(id+"F3.imprint","IMPRINT",FACE,{"disambiguationData":[TD([[makeQuery(id+"F3.imprint","IMPRINT",EDGE,{"derivedFrom":sQuery(id+"F3.wireOp",EDGE,"qhSCD0ZE-64rT-pPx1-dnGC-cia2z83dFbbt.bottom")}),-1.0]])]});
            var Q216;
            {var subQ0=sQuery(id+"F0.wireOp",EDGE,"E10.3.18.0");var subQ1=sQuery(id+"F0.wireOp",EDGE,"E3.12.0.0");var subQ2=makeQuery(id+"F0.imprint","INTERSECT",VERTEX,{"derivedFrom":[subQ1,subQ0]});Q216=makeQuery(id+"F0.imprint","IMPRINT",FACE,{"disambiguationData":[TD([[makeQuery(id+"F0.imprint","IMPRINT",EDGE,{"disambiguationData":[TD([[subQ2,-1.0]])],"derivedFrom":subQ1}),1.0]])]});}
            var Q217;
            {var subQ0=sQuery(id+"F0.wireOp",EDGE,"E10.3.19.0");var subQ1=sQuery(id+"F0.wireOp",EDGE,"E3.12.0.0");var subQ2=makeQuery(id+"F0.imprint","INTERSECT",VERTEX,{"derivedFrom":[subQ1,subQ0]});Q217=makeQuery(id+"F0.imprint","IMPRINT",FACE,{"disambiguationData":[TD([[makeQuery(id+"F0.imprint","IMPRINT",EDGE,{"disambiguationData":[TD([[subQ2,-1.0]])],"derivedFrom":subQ1}),1.0]])]});}
            var Q218;
            {var subQ0=sQuery(id+"F0.wireOp",EDGE,"E10.3.20.0");var subQ1=sQuery(id+"F0.wireOp",EDGE,"E3.12.0.0");var subQ2=makeQuery(id+"F0.imprint","INTERSECT",VERTEX,{"derivedFrom":[subQ1,subQ0]});Q218=makeQuery(id+"F0.imprint","IMPRINT",FACE,{"disambiguationData":[TD([[makeQuery(id+"F0.imprint","IMPRINT",EDGE,{"disambiguationData":[TD([[subQ2,-1.0]])],"derivedFrom":subQ1}),1.0]])]});}
            var Q219;
            {var subQ0=sQuery(id+"F0.wireOp",EDGE,"E10.3.21.0");var subQ1=sQuery(id+"F0.wireOp",EDGE,"E3.12.0.0");var subQ2=makeQuery(id+"F0.imprint","INTERSECT",VERTEX,{"derivedFrom":[subQ1,subQ0]});Q219=makeQuery(id+"F0.imprint","IMPRINT",FACE,{"disambiguationData":[TD([[makeQuery(id+"F0.imprint","IMPRINT",EDGE,{"disambiguationData":[TD([[subQ2,-1.0]])],"derivedFrom":subQ1}),1.0]])]});}
            var Q220;
            {var subQ0=sQuery(id+"F0.wireOp",EDGE,"E10.3.22.0");var subQ1=sQuery(id+"F0.wireOp",EDGE,"E3.12.0.0");var subQ2=makeQuery(id+"F0.imprint","INTERSECT",VERTEX,{"derivedFrom":[subQ1,subQ0]});Q220=makeQuery(id+"F0.imprint","IMPRINT",FACE,{"disambiguationData":[TD([[makeQuery(id+"F0.imprint","IMPRINT",EDGE,{"disambiguationData":[TD([[subQ2,-1.0]])],"derivedFrom":subQ1}),1.0]])]});}
            var Q221;
            {var subQ0=sQuery(id+"F0.wireOp",EDGE,"E10.3.23.0");var subQ1=sQuery(id+"F0.wireOp",EDGE,"E3.12.0.0");var subQ2=makeQuery(id+"F0.imprint","INTERSECT",VERTEX,{"derivedFrom":[subQ1,subQ0]});Q221=makeQuery(id+"F0.imprint","IMPRINT",FACE,{"disambiguationData":[TD([[makeQuery(id+"F0.imprint","IMPRINT",EDGE,{"disambiguationData":[TD([[subQ2,-1.0]])],"derivedFrom":subQ1}),1.0]])]});}
            var Q222;
            {var subQ0=sQuery(id+"F0.wireOp",EDGE,"E10.3.15.0");var subQ1=sQuery(id+"F0.wireOp",EDGE,"E3.12.0.0");var subQ2=makeQuery(id+"F0.imprint","INTERSECT",VERTEX,{"derivedFrom":[subQ1,subQ0]});Q222=makeQuery(id+"F0.imprint","IMPRINT",FACE,{"disambiguationData":[TD([[makeQuery(id+"F0.imprint","IMPRINT",EDGE,{"disambiguationData":[TD([[subQ2,-1.0]])],"derivedFrom":subQ1}),1.0]])]});}
            var Q223;
            {var subQ0=sQuery(id+"F0.wireOp",EDGE,"E10.3.14.0");var subQ1=sQuery(id+"F0.wireOp",EDGE,"E3.12.0.0");var subQ2=makeQuery(id+"F0.imprint","INTERSECT",VERTEX,{"derivedFrom":[subQ1,subQ0]});Q223=makeQuery(id+"F0.imprint","IMPRINT",FACE,{"disambiguationData":[TD([[makeQuery(id+"F0.imprint","IMPRINT",EDGE,{"disambiguationData":[TD([[subQ2,-1.0]])],"derivedFrom":subQ1}),1.0]])]});}
            var Q224;
            {var subQ0=sQuery(id+"F0.wireOp",EDGE,"E10.3.13.0");var subQ1=sQuery(id+"F0.wireOp",EDGE,"E3.12.0.0");var subQ2=makeQuery(id+"F0.imprint","INTERSECT",VERTEX,{"derivedFrom":[subQ1,subQ0]});Q224=makeQuery(id+"F0.imprint","IMPRINT",FACE,{"disambiguationData":[TD([[makeQuery(id+"F0.imprint","IMPRINT",EDGE,{"disambiguationData":[TD([[subQ2,-1.0]])],"derivedFrom":subQ1}),1.0]])]});}
            var Q225;
            {var subQ0=sQuery(id+"F0.wireOp",EDGE,"E10.3.12.0");var subQ1=sQuery(id+"F0.wireOp",EDGE,"E3.12.0.0");var subQ2=makeQuery(id+"F0.imprint","INTERSECT",VERTEX,{"derivedFrom":[subQ1,subQ0]});Q225=makeQuery(id+"F0.imprint","IMPRINT",FACE,{"disambiguationData":[TD([[makeQuery(id+"F0.imprint","IMPRINT",EDGE,{"disambiguationData":[TD([[subQ2,-1.0]])],"derivedFrom":subQ1}),1.0]])]});}
            var Q226;
            {var subQ0=sQuery(id+"F0.wireOp",EDGE,"E10.3.11.0");var subQ1=sQuery(id+"F0.wireOp",EDGE,"E3.12.0.0");var subQ2=makeQuery(id+"F0.imprint","INTERSECT",VERTEX,{"derivedFrom":[subQ1,subQ0]});Q226=makeQuery(id+"F0.imprint","IMPRINT",FACE,{"disambiguationData":[TD([[makeQuery(id+"F0.imprint","IMPRINT",EDGE,{"disambiguationData":[TD([[subQ2,-1.0]])],"derivedFrom":subQ1}),1.0]])]});}
            var Q227;
            {var subQ0=sQuery(id+"F0.wireOp",EDGE,"E10.3.23.0");var subQ1=sQuery(id+"F0.wireOp",EDGE,"E3.15.0.0");var subQ2=makeQuery(id+"F0.imprint","INTERSECT",VERTEX,{"derivedFrom":[subQ1,subQ0]});Q227=makeQuery(id+"F0.imprint","IMPRINT",FACE,{"disambiguationData":[TD([[makeQuery(id+"F0.imprint","IMPRINT",EDGE,{"disambiguationData":[TD([[subQ2,-1.0]])],"derivedFrom":subQ1}),1.0]])]});}
            var Q228;
            {var subQ0=sQuery(id+"F0.wireOp",EDGE,"E10.3.22.0");var subQ1=sQuery(id+"F0.wireOp",EDGE,"E3.15.0.0");var subQ2=makeQuery(id+"F0.imprint","INTERSECT",VERTEX,{"derivedFrom":[subQ1,subQ0]});Q228=makeQuery(id+"F0.imprint","IMPRINT",FACE,{"disambiguationData":[TD([[makeQuery(id+"F0.imprint","IMPRINT",EDGE,{"disambiguationData":[TD([[subQ2,-1.0]])],"derivedFrom":subQ1}),1.0]])]});}
            var Q229;
            {var subQ0=sQuery(id+"F0.wireOp",EDGE,"E10.3.21.0");var subQ1=sQuery(id+"F0.wireOp",EDGE,"E3.16.0.0");var subQ2=makeQuery(id+"F0.imprint","INTERSECT",VERTEX,{"derivedFrom":[subQ1,subQ0]});Q229=makeQuery(id+"F0.imprint","IMPRINT",FACE,{"disambiguationData":[TD([[makeQuery(id+"F0.imprint","IMPRINT",EDGE,{"disambiguationData":[TD([[subQ2,-1.0]])],"derivedFrom":subQ1}),1.0]])]});}
            var Q230;
            {var subQ0=sQuery(id+"F0.wireOp",EDGE,"E10.3.20.0");var subQ1=sQuery(id+"F0.wireOp",EDGE,"E3.16.0.0");var subQ2=makeQuery(id+"F0.imprint","INTERSECT",VERTEX,{"derivedFrom":[subQ1,subQ0]});Q230=makeQuery(id+"F0.imprint","IMPRINT",FACE,{"disambiguationData":[TD([[makeQuery(id+"F0.imprint","IMPRINT",EDGE,{"disambiguationData":[TD([[subQ2,-1.0]])],"derivedFrom":subQ1}),1.0]])]});}
            var Q231;
            {var subQ0=sQuery(id+"F0.wireOp",EDGE,"E10.3.19.0");var subQ1=sQuery(id+"F0.wireOp",EDGE,"E3.16.0.0");var subQ2=makeQuery(id+"F0.imprint","INTERSECT",VERTEX,{"derivedFrom":[subQ1,subQ0]});Q231=makeQuery(id+"F0.imprint","IMPRINT",FACE,{"disambiguationData":[TD([[makeQuery(id+"F0.imprint","IMPRINT",EDGE,{"disambiguationData":[TD([[subQ2,-1.0]])],"derivedFrom":subQ1}),1.0]])]});}
            var Q232;
            {var subQ0=sQuery(id+"F0.wireOp",EDGE,"E10.3.17.0");var subQ1=sQuery(id+"F0.wireOp",EDGE,"E3.15.0.0");var subQ2=makeQuery(id+"F0.imprint","INTERSECT",VERTEX,{"derivedFrom":[subQ1,subQ0]});Q232=makeQuery(id+"F0.imprint","IMPRINT",FACE,{"disambiguationData":[TD([[makeQuery(id+"F0.imprint","IMPRINT",EDGE,{"disambiguationData":[TD([[subQ2,-1.0]])],"derivedFrom":subQ1}),1.0]])]});}
            var Q233;
            {var subQ0=sQuery(id+"F0.wireOp",EDGE,"E10.3.18.0");var subQ1=sQuery(id+"F0.wireOp",EDGE,"E3.15.0.0");var subQ2=makeQuery(id+"F0.imprint","INTERSECT",VERTEX,{"derivedFrom":[subQ1,subQ0]});Q233=makeQuery(id+"F0.imprint","IMPRINT",FACE,{"disambiguationData":[TD([[makeQuery(id+"F0.imprint","IMPRINT",EDGE,{"disambiguationData":[TD([[subQ2,-1.0]])],"derivedFrom":subQ1}),1.0]])]});}
            extrude(context, id + "F1", {"entities" : qUnion([Q0, Q1, Q2, Q3, Q4, Q5, Q6, Q7, Q8, Q9, Q10, Q11, Q12, Q13, Q14, Q15, Q16, Q17, Q18, Q19, Q20, Q21, Q22, Q23, Q24, Q25, Q26, Q27, Q28, Q29, Q30, Q31, Q32, Q33, Q34, Q35, Q36, Q37, Q38, Q39, Q40, Q41, Q42, Q43, Q44, Q45, Q46, Q47, Q48, Q49, Q50, Q51, Q52, Q53, Q54, Q55, Q56, Q57, Q58, Q59, Q60, Q61, Q62, Q63, Q64, Q65, Q66, Q67, Q68, Q69, Q70, Q71, Q72, Q73, Q74, Q75, Q76, Q77, Q78, Q79, Q80, Q81, Q82, Q83, Q84, Q85, Q86, Q87, Q88, Q89, Q90, Q91, Q92, Q93, Q94, Q95, Q96, Q97, Q98, Q99, Q100, Q101, Q102, Q103, Q104, Q105, Q106, Q107, Q108, Q109, Q110, Q111, Q112, Q113, Q114, Q115, Q116, Q117, Q118, Q119, Q120, Q121, Q122, Q123, Q124, Q125, Q126, Q127, Q128, Q129, Q130, Q131, Q132, Q133, Q134, Q135, Q136, Q137, Q138, Q139, Q140, Q141, Q142, Q143, Q144, Q145, Q146, Q147, Q148, Q149, Q150, Q151, Q152, Q153, Q154, Q155, Q156, Q157, Q158, Q159, Q160, Q161, Q162, Q163, Q164, Q165, Q166, Q167, Q168, Q169, Q170, Q171, Q172, Q173, Q174, Q175, Q176, Q177, Q178, Q179, Q180, Q181, Q182, Q183, Q184, Q185, Q186, Q187, Q188, Q189, Q190, Q191, Q192, Q193, Q194, Q195, Q196, Q197, Q198, Q199, Q200, Q201, Q202, Q203, Q204, Q205, Q206, Q207, Q208, Q209, Q210, Q211, Q212, Q213, Q214, Q215, Q216, Q217, Q218, Q219, Q220, Q221, Q222, Q223, Q224, Q225, Q226, Q227, Q228, Q229, Q230, Q231, Q232, Q233]), "depth" : .1 * mm, "offsetDistance" : 25.4 * mm});
        }
        {
            var Q0;
            Q0=makeQuery(id+"F0.imprint","IMPRINT",FACE,{"disambiguationData":[TD([[makeQuery(id+"F0.imprint","IMPRINT",EDGE,{"derivedFrom":sQuery(id+"F0.wireOp",EDGE,"E18.24.28.0")}),1.0]])]});
            var Q1;
            Q1=makeQuery(id+"F0.imprint","IMPRINT",FACE,{"disambiguationData":[TD([[makeQuery(id+"F0.imprint","IMPRINT",EDGE,{"derivedFrom":sQuery(id+"F0.wireOp",EDGE,"E18.24.27.0")}),1.0]])]});
            var Q2;
            Q2=makeQuery(id+"F0.imprint","IMPRINT",FACE,{"disambiguationData":[TD([[makeQuery(id+"F0.imprint","IMPRINT",EDGE,{"derivedFrom":sQuery(id+"F0.wireOp",EDGE,"E18.24.26.0")}),1.0]])]});
            var Q3;
            Q3=makeQuery(id+"F0.imprint","IMPRINT",FACE,{"disambiguationData":[TD([[makeQuery(id+"F0.imprint","IMPRINT",EDGE,{"derivedFrom":sQuery(id+"F0.wireOp",EDGE,"E18.24.25.0")}),1.0]])]});
            var Q4;
            Q4=makeQuery(id+"F0.imprint","IMPRINT",FACE,{"disambiguationData":[TD([[makeQuery(id+"F0.imprint","IMPRINT",EDGE,{"derivedFrom":sQuery(id+"F0.wireOp",EDGE,"E18.24.24.0")}),1.0]])]});
            var Q5;
            Q5=makeQuery(id+"F0.imprint","IMPRINT",FACE,{"disambiguationData":[TD([[makeQuery(id+"F0.imprint","IMPRINT",EDGE,{"derivedFrom":sQuery(id+"F0.wireOp",EDGE,"E18.24.23.0")}),1.0]])]});
            var Q6;
            Q6=makeQuery(id+"F0.imprint","IMPRINT",FACE,{"disambiguationData":[TD([[makeQuery(id+"F0.imprint","IMPRINT",EDGE,{"derivedFrom":sQuery(id+"F0.wireOp",EDGE,"E18.24.22.0")}),1.0]])]});
            var Q7;
            Q7=makeQuery(id+"F0.imprint","IMPRINT",FACE,{"disambiguationData":[TD([[makeQuery(id+"F0.imprint","IMPRINT",EDGE,{"derivedFrom":sQuery(id+"F0.wireOp",EDGE,"E18.24.21.0")}),1.0]])]});
            var Q8;
            Q8=makeQuery(id+"F0.imprint","IMPRINT",FACE,{"disambiguationData":[TD([[makeQuery(id+"F0.imprint","IMPRINT",EDGE,{"derivedFrom":sQuery(id+"F0.wireOp",EDGE,"E18.22.28.0")}),1.0]])]});
            var Q9;
            Q9=makeQuery(id+"F0.imprint","IMPRINT",FACE,{"disambiguationData":[TD([[makeQuery(id+"F0.imprint","IMPRINT",EDGE,{"derivedFrom":sQuery(id+"F0.wireOp",EDGE,"E18.28.28.0")}),1.0]])]});
            var Q10;
            Q10=makeQuery(id+"F0.imprint","IMPRINT",FACE,{"disambiguationData":[TD([[makeQuery(id+"F0.imprint","IMPRINT",EDGE,{"derivedFrom":sQuery(id+"F0.wireOp",EDGE,"E18.32.28.0")}),1.0]])]});
            var Q11;
            Q11=makeQuery(id+"F0.imprint","IMPRINT",FACE,{"disambiguationData":[TD([[makeQuery(id+"F0.imprint","IMPRINT",EDGE,{"derivedFrom":sQuery(id+"F0.wireOp",EDGE,"E18.32.27.0")}),1.0]])]});
            var Q12;
            Q12=makeQuery(id+"F0.imprint","IMPRINT",FACE,{"disambiguationData":[TD([[makeQuery(id+"F0.imprint","IMPRINT",EDGE,{"derivedFrom":sQuery(id+"F0.wireOp",EDGE,"E18.28.27.0")}),1.0]])]});
            var Q13;
            Q13=makeQuery(id+"F0.imprint","IMPRINT",FACE,{"disambiguationData":[TD([[makeQuery(id+"F0.imprint","IMPRINT",EDGE,{"derivedFrom":sQuery(id+"F0.wireOp",EDGE,"E18.28.26.0")}),1.0]])]});
            var Q14;
            Q14=makeQuery(id+"F0.imprint","IMPRINT",FACE,{"disambiguationData":[TD([[makeQuery(id+"F0.imprint","IMPRINT",EDGE,{"derivedFrom":sQuery(id+"F0.wireOp",EDGE,"E18.32.26.0")}),1.0]])]});
            var Q15;
            Q15=makeQuery(id+"F0.imprint","IMPRINT",FACE,{"disambiguationData":[TD([[makeQuery(id+"F0.imprint","IMPRINT",EDGE,{"derivedFrom":sQuery(id+"F0.wireOp",EDGE,"E18.22.22.0")}),1.0]])]});
            var Q16;
            Q16=makeQuery(id+"F0.imprint","IMPRINT",FACE,{"disambiguationData":[TD([[makeQuery(id+"F0.imprint","IMPRINT",EDGE,{"derivedFrom":sQuery(id+"F0.wireOp",EDGE,"E18.22.21.0")}),1.0]])]});
            var Q17;
            Q17=makeQuery(id+"F0.imprint","IMPRINT",FACE,{"disambiguationData":[TD([[makeQuery(id+"F0.imprint","IMPRINT",EDGE,{"derivedFrom":sQuery(id+"F0.wireOp",EDGE,"E18.24.20.0")}),1.0]])]});
            var Q18;
            Q18=makeQuery(id+"F0.imprint","IMPRINT",FACE,{"disambiguationData":[TD([[makeQuery(id+"F0.imprint","IMPRINT",EDGE,{"derivedFrom":sQuery(id+"F0.wireOp",EDGE,"E18.24.19.0")}),1.0]])]});
            var Q19;
            Q19=makeQuery(id+"F0.imprint","IMPRINT",FACE,{"disambiguationData":[TD([[makeQuery(id+"F0.imprint","IMPRINT",EDGE,{"derivedFrom":sQuery(id+"F0.wireOp",EDGE,"E18.24.18.0")}),1.0]])]});
            var Q20;
            Q20=makeQuery(id+"F0.imprint","IMPRINT",FACE,{"disambiguationData":[TD([[makeQuery(id+"F0.imprint","IMPRINT",EDGE,{"derivedFrom":sQuery(id+"F0.wireOp",EDGE,"E18.24.17.0")}),1.0]])]});
            var Q21;
            Q21=makeQuery(id+"F0.imprint","IMPRINT",FACE,{"disambiguationData":[TD([[makeQuery(id+"F0.imprint","IMPRINT",EDGE,{"derivedFrom":sQuery(id+"F0.wireOp",EDGE,"E18.24.16.0")}),1.0]])]});
            var Q22;
            Q22=makeQuery(id+"F0.imprint","IMPRINT",FACE,{"disambiguationData":[TD([[makeQuery(id+"F0.imprint","IMPRINT",EDGE,{"derivedFrom":sQuery(id+"F0.wireOp",EDGE,"E18.24.15.0")}),1.0]])]});
            var Q23;
            Q23=makeQuery(id+"F0.imprint","IMPRINT",FACE,{"disambiguationData":[TD([[makeQuery(id+"F0.imprint","IMPRINT",EDGE,{"derivedFrom":sQuery(id+"F0.wireOp",EDGE,"E18.28.15.0")}),1.0]])]});
            var Q24;
            Q24=makeQuery(id+"F0.imprint","IMPRINT",FACE,{"disambiguationData":[TD([[makeQuery(id+"F0.imprint","IMPRINT",EDGE,{"derivedFrom":sQuery(id+"F0.wireOp",EDGE,"E18.32.15.0")}),1.0]])]});
            var Q25;
            Q25=makeQuery(id+"F0.imprint","IMPRINT",FACE,{"disambiguationData":[TD([[makeQuery(id+"F0.imprint","IMPRINT",EDGE,{"derivedFrom":sQuery(id+"F0.wireOp",EDGE,"E18.28.16.0")}),1.0]])]});
            var Q26;
            Q26=makeQuery(id+"F0.imprint","IMPRINT",FACE,{"disambiguationData":[TD([[makeQuery(id+"F0.imprint","IMPRINT",EDGE,{"derivedFrom":sQuery(id+"F0.wireOp",EDGE,"E18.28.17.0")}),1.0]])]});
            var Q27;
            Q27=makeQuery(id+"F0.imprint","IMPRINT",FACE,{"disambiguationData":[TD([[makeQuery(id+"F0.imprint","IMPRINT",EDGE,{"derivedFrom":sQuery(id+"F0.wireOp",EDGE,"E18.28.18.0")}),1.0]])]});
            var Q28;
            Q28=makeQuery(id+"F0.imprint","IMPRINT",FACE,{"disambiguationData":[TD([[makeQuery(id+"F0.imprint","IMPRINT",EDGE,{"derivedFrom":sQuery(id+"F0.wireOp",EDGE,"E18.28.19.0")}),1.0]])]});
            var Q29;
            Q29=makeQuery(id+"F0.imprint","IMPRINT",FACE,{"disambiguationData":[TD([[makeQuery(id+"F0.imprint","IMPRINT",EDGE,{"derivedFrom":sQuery(id+"F0.wireOp",EDGE,"E18.28.20.0")}),1.0]])]});
            var Q30;
            Q30=makeQuery(id+"F0.imprint","IMPRINT",FACE,{"disambiguationData":[TD([[makeQuery(id+"F0.imprint","IMPRINT",EDGE,{"derivedFrom":sQuery(id+"F0.wireOp",EDGE,"E18.32.21.0")}),1.0]])]});
            var Q31;
            Q31=makeQuery(id+"F0.imprint","IMPRINT",FACE,{"disambiguationData":[TD([[makeQuery(id+"F0.imprint","IMPRINT",EDGE,{"derivedFrom":sQuery(id+"F0.wireOp",EDGE,"E18.28.21.0")}),1.0]])]});
            var Q32;
            Q32=makeQuery(id+"F0.imprint","IMPRINT",FACE,{"disambiguationData":[TD([[makeQuery(id+"F0.imprint","IMPRINT",EDGE,{"derivedFrom":sQuery(id+"F0.wireOp",EDGE,"E18.28.22.0")}),1.0]])]});
            var Q33;
            Q33=makeQuery(id+"F0.imprint","IMPRINT",FACE,{"disambiguationData":[TD([[makeQuery(id+"F0.imprint","IMPRINT",EDGE,{"derivedFrom":sQuery(id+"F0.wireOp",EDGE,"E18.32.22.0")}),1.0]])]});
            var Q34;
            Q34=makeQuery(id+"F0.imprint","IMPRINT",FACE,{"disambiguationData":[TD([[makeQuery(id+"F0.imprint","IMPRINT",EDGE,{"derivedFrom":sQuery(id+"F0.wireOp",EDGE,"E18.28.24.0")}),1.0]])]});
            var Q35;
            Q35=makeQuery(id+"F0.imprint","IMPRINT",FACE,{"disambiguationData":[TD([[makeQuery(id+"F0.imprint","IMPRINT",EDGE,{"derivedFrom":sQuery(id+"F0.wireOp",EDGE,"E18.28.23.0")}),1.0]])]});
            var Q36;
            Q36=makeQuery(id+"F0.imprint","IMPRINT",FACE,{"disambiguationData":[TD([[makeQuery(id+"F0.imprint","IMPRINT",EDGE,{"derivedFrom":sQuery(id+"F0.wireOp",EDGE,"E18.32.23.0")}),1.0]])]});
            var Q37;
            Q37=makeQuery(id+"F0.imprint","IMPRINT",FACE,{"disambiguationData":[TD([[makeQuery(id+"F0.imprint","IMPRINT",EDGE,{"derivedFrom":sQuery(id+"F0.wireOp",EDGE,"E18.32.24.0")}),1.0]])]});
            var Q38;
            Q38=makeQuery(id+"F0.imprint","IMPRINT",FACE,{"disambiguationData":[TD([[makeQuery(id+"F0.imprint","IMPRINT",EDGE,{"derivedFrom":sQuery(id+"F0.wireOp",EDGE,"E18.32.25.0")}),1.0]])]});
            var Q39;
            Q39=makeQuery(id+"F0.imprint","IMPRINT",FACE,{"disambiguationData":[TD([[makeQuery(id+"F0.imprint","IMPRINT",EDGE,{"derivedFrom":sQuery(id+"F0.wireOp",EDGE,"E18.28.25.0")}),1.0]])]});
            var Q40;
            Q40=makeQuery(id+"F0.imprint","IMPRINT",FACE,{"disambiguationData":[TD([[makeQuery(id+"F0.imprint","IMPRINT",EDGE,{"derivedFrom":sQuery(id+"F0.wireOp",EDGE,"E18.36.28.0")}),1.0]])]});
            var Q41;
            Q41=makeQuery(id+"F0.imprint","IMPRINT",FACE,{"disambiguationData":[TD([[makeQuery(id+"F0.imprint","IMPRINT",EDGE,{"derivedFrom":sQuery(id+"F0.wireOp",EDGE,"E18.38.28.0")}),1.0]])]});
            var Q42;
            Q42=makeQuery(id+"F0.imprint","IMPRINT",FACE,{"disambiguationData":[TD([[makeQuery(id+"F0.imprint","IMPRINT",EDGE,{"derivedFrom":sQuery(id+"F0.wireOp",EDGE,"E18.36.27.0")}),1.0]])]});
            var Q43;
            Q43=makeQuery(id+"F0.imprint","IMPRINT",FACE,{"disambiguationData":[TD([[makeQuery(id+"F0.imprint","IMPRINT",EDGE,{"derivedFrom":sQuery(id+"F0.wireOp",EDGE,"E18.38.27.0")}),1.0]])]});
            var Q44;
            Q44=makeQuery(id+"F0.imprint","IMPRINT",FACE,{"disambiguationData":[TD([[makeQuery(id+"F0.imprint","IMPRINT",EDGE,{"derivedFrom":sQuery(id+"F0.wireOp",EDGE,"E18.36.26.0")}),1.0]])]});
            var Q45;
            Q45=makeQuery(id+"F0.imprint","IMPRINT",FACE,{"disambiguationData":[TD([[makeQuery(id+"F0.imprint","IMPRINT",EDGE,{"derivedFrom":sQuery(id+"F0.wireOp",EDGE,"E18.38.26.0")}),1.0]])]});
            var Q46;
            Q46=makeQuery(id+"F0.imprint","IMPRINT",FACE,{"disambiguationData":[TD([[makeQuery(id+"F0.imprint","IMPRINT",EDGE,{"derivedFrom":sQuery(id+"F0.wireOp",EDGE,"E18.36.25.0")}),1.0]])]});
            var Q47;
            Q47=makeQuery(id+"F0.imprint","IMPRINT",FACE,{"disambiguationData":[TD([[makeQuery(id+"F0.imprint","IMPRINT",EDGE,{"derivedFrom":sQuery(id+"F0.wireOp",EDGE,"E18.38.25.0")}),1.0]])]});
            var Q48;
            Q48=makeQuery(id+"F0.imprint","IMPRINT",FACE,{"disambiguationData":[TD([[makeQuery(id+"F0.imprint","IMPRINT",EDGE,{"derivedFrom":sQuery(id+"F0.wireOp",EDGE,"E18.36.24.0")}),1.0]])]});
            var Q49;
            Q49=makeQuery(id+"F0.imprint","IMPRINT",FACE,{"disambiguationData":[TD([[makeQuery(id+"F0.imprint","IMPRINT",EDGE,{"derivedFrom":sQuery(id+"F0.wireOp",EDGE,"E18.38.24.0")}),1.0]])]});
            var Q50;
            Q50=makeQuery(id+"F0.imprint","IMPRINT",FACE,{"disambiguationData":[TD([[makeQuery(id+"F0.imprint","IMPRINT",EDGE,{"derivedFrom":sQuery(id+"F0.wireOp",EDGE,"E18.36.23.0")}),1.0]])]});
            var Q51;
            Q51=makeQuery(id+"F0.imprint","IMPRINT",FACE,{"disambiguationData":[TD([[makeQuery(id+"F0.imprint","IMPRINT",EDGE,{"derivedFrom":sQuery(id+"F0.wireOp",EDGE,"E18.38.23.0")}),1.0]])]});
            var Q52;
            Q52=makeQuery(id+"F0.imprint","IMPRINT",FACE,{"disambiguationData":[TD([[makeQuery(id+"F0.imprint","IMPRINT",EDGE,{"derivedFrom":sQuery(id+"F0.wireOp",EDGE,"E18.36.22.0")}),1.0]])]});
            var Q53;
            Q53=makeQuery(id+"F0.imprint","IMPRINT",FACE,{"disambiguationData":[TD([[makeQuery(id+"F0.imprint","IMPRINT",EDGE,{"derivedFrom":sQuery(id+"F0.wireOp",EDGE,"E18.36.21.0")}),1.0]])]});
            var Q54;
            Q54=makeQuery(id+"F0.imprint","IMPRINT",FACE,{"disambiguationData":[TD([[makeQuery(id+"F0.imprint","IMPRINT",EDGE,{"derivedFrom":sQuery(id+"F0.wireOp",EDGE,"E18.40.28.0")}),1.0]])]});
            var Q55;
            Q55=makeQuery(id+"F0.imprint","IMPRINT",FACE,{"disambiguationData":[TD([[makeQuery(id+"F0.imprint","IMPRINT",EDGE,{"derivedFrom":sQuery(id+"F0.wireOp",EDGE,"E18.40.27.0")}),1.0]])]});
            var Q56;
            Q56=makeQuery(id+"F0.imprint","IMPRINT",FACE,{"disambiguationData":[TD([[makeQuery(id+"F0.imprint","IMPRINT",EDGE,{"derivedFrom":sQuery(id+"F0.wireOp",EDGE,"E18.40.26.0")}),1.0]])]});
            var Q57;
            Q57=makeQuery(id+"F0.imprint","IMPRINT",FACE,{"disambiguationData":[TD([[makeQuery(id+"F0.imprint","IMPRINT",EDGE,{"derivedFrom":sQuery(id+"F0.wireOp",EDGE,"E18.40.25.0")}),1.0]])]});
            var Q58;
            Q58=makeQuery(id+"F0.imprint","IMPRINT",FACE,{"disambiguationData":[TD([[makeQuery(id+"F0.imprint","IMPRINT",EDGE,{"derivedFrom":sQuery(id+"F0.wireOp",EDGE,"E18.40.24.0")}),1.0]])]});
            var Q59;
            Q59=makeQuery(id+"F0.imprint","IMPRINT",FACE,{"disambiguationData":[TD([[makeQuery(id+"F0.imprint","IMPRINT",EDGE,{"derivedFrom":sQuery(id+"F0.wireOp",EDGE,"E18.40.23.0")}),1.0]])]});
            extrude(context, id + "F2", {"entities" : qUnion([Q0, Q1, Q2, Q3, Q4, Q5, Q6, Q7, Q8, Q9, Q10, Q11, Q12, Q13, Q14, Q15, Q16, Q17, Q18, Q19, Q20, Q21, Q22, Q23, Q24, Q25, Q26, Q27, Q28, Q29, Q30, Q31, Q32, Q33, Q34, Q35, Q36, Q37, Q38, Q39, Q40, Q41, Q42, Q43, Q44, Q45, Q46, Q47, Q48, Q49, Q50, Q51, Q52, Q53, Q54, Q55, Q56, Q57, Q58, Q59]), "depth" : .1 * mm, "offsetDistance" : 25.4 * mm});
        }
    });
